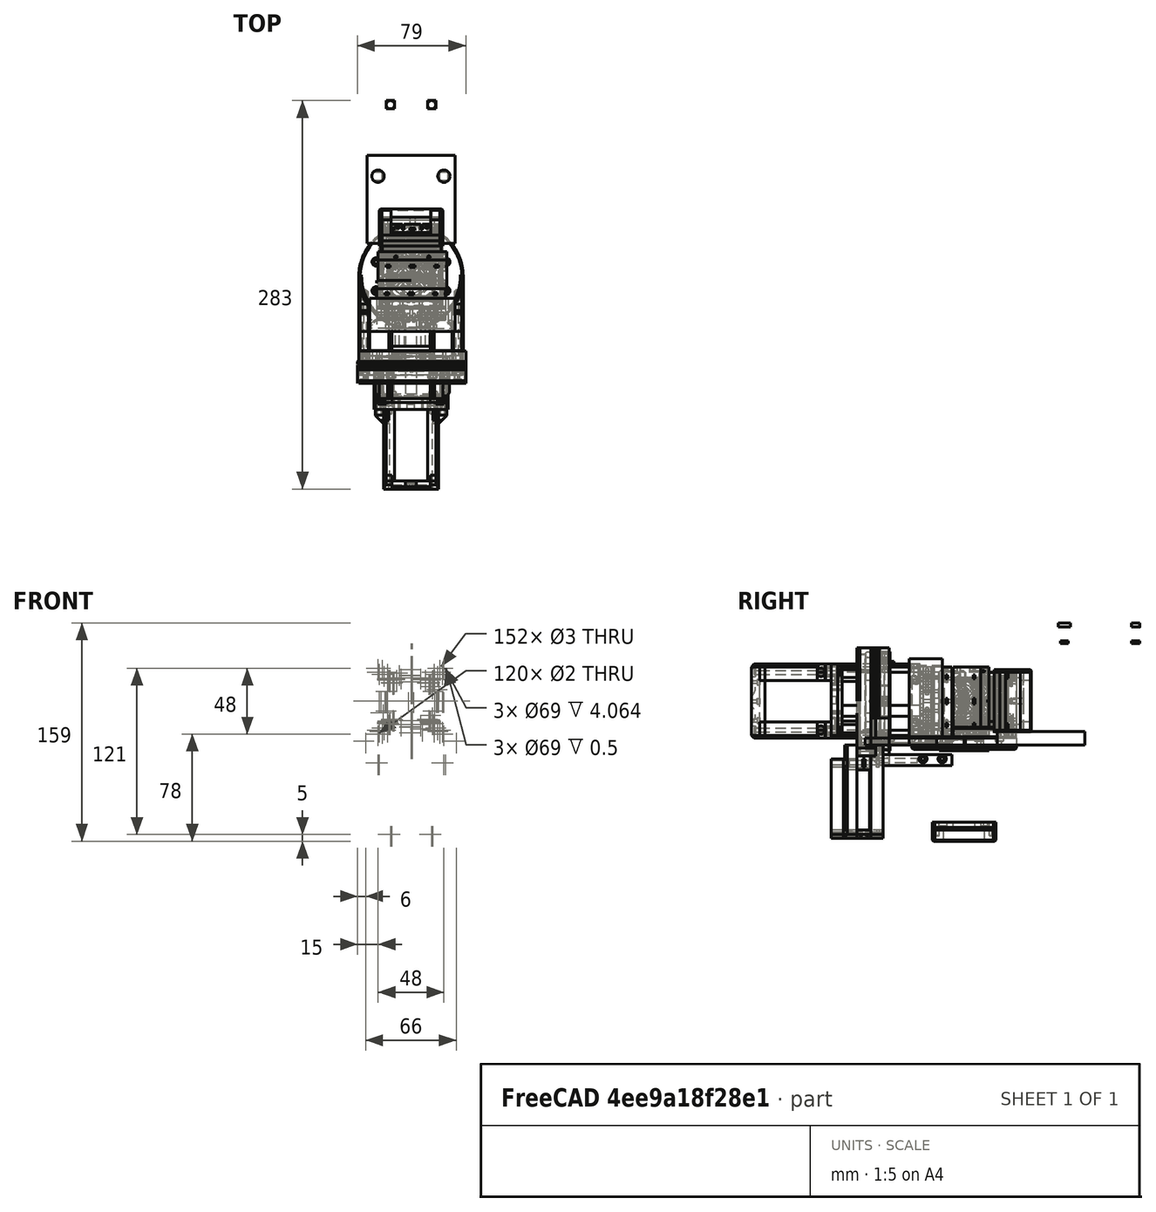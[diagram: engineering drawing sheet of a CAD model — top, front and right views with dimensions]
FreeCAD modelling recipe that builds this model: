
FCSTD DOCUMENT  (FreeCAD 0.19R24276 (Git))
Label: G-mini_056
License: All rights reserved
LicenseURL: http://en.wikipedia.org/wiki/All_rights_reserved
objects: Part::Cylinder×670, Part::Box×316, Part::Compound×305, Part::Cut×299, Part::Chamfer×105, Part::FeaturePython×44, Mesh::Feature×28, Part::Torus×9, Part::Common×4
note: 1752 computed .brp shape members not serialized (recipe doc carries the construction recipe); baked Part::Feature solids carry a one-line shape summary decoded from their .brp

FEATURE [Part::Cylinder] Cylinder2608  label="Válec2578"
  Angle = 360
  AttacherType = Attacher::AttachEngine3D
  Height = 3
  Placement = pos=(1.1e-14,-27.5,19) rot=(0,0,1;3.14159rad)
  Radius = 3
FEATURE [Part::Cylinder] Cylinder2607  label="Válec2577"
  Angle = 360
  AttacherType = Attacher::AttachEngine3D
  Height = 3
  Placement = pos=(-19.4454,-19.4454,19) rot=(0,0,1;2.35619rad)
  Radius = 3
FEATURE [Part::Cylinder] Cylinder2613  label="Válec2583"
  Angle = 360
  AttacherType = Attacher::AttachEngine3D
  Height = 20
  Placement = pos=(-19.4454,19.4454,19) rot=(0,0,1;0.785398rad)
  Radius = 1.5
FEATURE [Part::Cylinder] Cylinder2615  label="Válec2585"
  Angle = 360
  AttacherType = Attacher::AttachEngine3D
  Height = 20
  Placement = pos=(-19.4454,-19.4454,19) rot=(0,0,1;2.35619rad)
  Radius = 1.5
FEATURE [Part::Cylinder] Cylinder2617  label="Válec2587"
  Angle = 360
  AttacherType = Attacher::AttachEngine3D
  Height = 20
  Placement = pos=(19.4454,-19.4454,19) rot=(0,0,1;3.92699rad)
  Radius = 1.5
FEATURE [Part::Cylinder] Cylinder2605  label="Válec2575"
  Angle = 360
  AttacherType = Attacher::AttachEngine3D
  Height = 3
  Placement = pos=(-19.4454,19.4454,19) rot=(0,0,1;0.785398rad)
  Radius = 3
FEATURE [Part::Cylinder] Cylinder2606  label="Válec2576"
  Angle = 360
  AttacherType = Attacher::AttachEngine3D
  Height = 3
  Placement = pos=(-27.5,-4e-15,19) rot=(0,0,1;1.5708rad)
  Radius = 3
FEATURE [Part::Cylinder] Cylinder2609  label="Válec2579"
  Angle = 360
  AttacherType = Attacher::AttachEngine3D
  Height = 3
  Placement = pos=(19.4454,-19.4454,19) rot=(0,0,1;3.92699rad)
  Radius = 3
FEATURE [Part::Cylinder] Cylinder2610  label="Válec2580"
  Angle = 360
  AttacherType = Attacher::AttachEngine3D
  Height = 3
  Placement = pos=(27.5,1.2e-14,19) rot=(0,0,-1;1.5708rad)
  Radius = 3
FEATURE [Part::Cylinder] Cylinder2611  label="Válec2581"
  Angle = 360
  AttacherType = Attacher::AttachEngine3D
  Height = 3
  Placement = pos=(19.4454,19.4454,19) rot=(0,0,-1;0.785398rad)
  Radius = 3
FEATURE [Part::Cylinder] Cylinder2614  label="Válec2584"
  Angle = 360
  AttacherType = Attacher::AttachEngine3D
  Height = 20
  Placement = pos=(-27.5,-4e-15,19) rot=(0,0,1;1.5708rad)
  Radius = 1.5
FEATURE [Part::Cylinder] Cylinder2616  label="Válec2586"
  Angle = 360
  AttacherType = Attacher::AttachEngine3D
  Height = 20
  Placement = pos=(1.1e-14,-27.5,19) rot=(0,0,1;3.14159rad)
  Radius = 1.5
FEATURE [Part::Cylinder] Cylinder2031  label="Válec2031"
  Angle = 360
  AttacherType = Attacher::AttachEngine3D
  Height = 30
  Placement = pos=(51,-30,0) rot=(0,0,1;0rad)
  Radius = 1.5
FEATURE [Part::Cylinder] Cylinder2014  label="Válec2014"
  Angle = 360
  AttacherType = Attacher::AttachEngine3D
  Height = 3
  Placement = pos=(0,27.5,19) rot=(0,0,1;0rad)
  Radius = 3
FEATURE [Part::Compound] Compound901
  Links = -> [Cylinder2014,Cylinder2605,Cylinder2606,Cylinder2607,Cylinder2608,Cylinder2609,Cylinder2610,Cylinder2611]
  Placement = pos=(0,0,-19) rot=(0,0,1;0rad)
FEATURE [Part::Cylinder] Cylinder2619  label="Válec2589"
  Angle = 360
  AttacherType = Attacher::AttachEngine3D
  Height = 20
  Placement = pos=(19.4454,19.4454,19) rot=(0,0,-1;0.785398rad)
  Radius = 1.5
FEATURE [Part::Cylinder] Cylinder2618  label="Válec2588"
  Angle = 360
  AttacherType = Attacher::AttachEngine3D
  Height = 20
  Placement = pos=(27.5,1.2e-14,19) rot=(0,0,-1;1.5708rad)
  Radius = 1.5
FEATURE [Part::Cylinder] Cylinder2016  label="Válec2016"
  Angle = 360
  AttacherType = Attacher::AttachEngine3D
  Height = 6
  Radius = 38
FEATURE [Part::Cut] Cut623
  Base = -> Cylinder2016
  Tool = -> Compound901
FEATURE [Part::Cylinder] Cylinder2023  label="Válec2023"
  Angle = 360
  AttacherType = Attacher::AttachEngine3D
  Height = 20
  Placement = pos=(0,27.5,19) rot=(0,0,1;0rad)
  Radius = 1.5
FEATURE [Part::Compound] Compound902
  Links = -> [Cylinder2023,Cylinder2613,Cylinder2614,Cylinder2615,Cylinder2616,Cylinder2617,Cylinder2618,Cylinder2619]
  Placement = pos=(0,0,-23) rot=(0,0,1;0rad)
FEATURE [Part::Cut] Cut624
  Base = -> Cut623
  Tool = -> Compound902
FEATURE [Part::Box] Box790  label="Krychle789"
  AttacherType = Attacher::AttachEngine3D
  Height = 80
  Length = 12
  Placement = pos=(-6,26,-48) rot=(0,0,1;0rad)
  Width = 7
FEATURE [Part::Compound] Compound1160
  Links = -> [Box790]
  Placement = pos=(80,-8,10) rot=(0.57735,-0.57735,0.57735;2.0944rad)
FEATURE [Part::Cylinder] Cylinder2035  label="Válec2035"
  Angle = 360
  AttacherType = Attacher::AttachEngine3D
  Height = 30
  Placement = pos=(51,16,0) rot=(0,0,1;0rad)
  Radius = 1.5
FEATURE [Part::Cylinder] Cylinder2033  label="Válec2033"
  Angle = 360
  AttacherType = Attacher::AttachEngine3D
  Height = 11
  Placement = pos=(44,0,10) rot=(0,1,0;1.5708rad)
  Radius = 38
FEATURE [Part::Common] Common005
  Base = -> Compound1160
  Tool = -> Cylinder2033
FEATURE [Part::Box] Box796  label="Krychle795"
  AttacherType = Attacher::AttachEngine3D
  Height = 2
  Length = 8
  Placement = pos=(48,-33,7) rot=(0,0,1;0rad)
  Width = 6
FEATURE [Part::Box] Box793  label="Krychle792"
  AttacherType = Attacher::AttachEngine3D
  Height = 2
  Length = 8
  Placement = pos=(48,-3,11) rot=(0,0,1;0rad)
  Width = 6
FEATURE [Part::Cylinder] Cylinder2030  label="Válec2030"
  Angle = 360
  AttacherType = Attacher::AttachEngine3D
  Height = 5
  Placement = pos=(0,0,1) rot=(0,0,1;0rad)
  Radius = 14
FEATURE [Part::Cut] Cut625
  Base = -> Cut624
  Tool = -> Cylinder2030
FEATURE [Part::Chamfer] Chamfer117
  Base = -> Cut625
  Edges = 1 edges r=1: [Edge3]
FEATURE [Part::Box] Box792  label="Krychle791"
  AttacherType = Attacher::AttachEngine3D
  Height = 2
  Length = 8
  Placement = pos=(48,-3,7) rot=(0,0,1;0rad)
  Width = 6
FEATURE [Part::Box] Box794  label="Krychle793"
  AttacherType = Attacher::AttachEngine3D
  Height = 2
  Length = 8
  Placement = pos=(48,27,11) rot=(0,0,1;0rad)
  Width = 6
FEATURE [Part::Cylinder] Cylinder2034  label="Válec2034"
  Angle = 360
  AttacherType = Attacher::AttachEngine3D
  Height = 30
  Placement = pos=(51,30,0) rot=(0,0,1;0rad)
  Radius = 1.5
FEATURE [Part::Box] Box795  label="Krychle794"
  AttacherType = Attacher::AttachEngine3D
  Height = 2
  Length = 8
  Placement = pos=(48,-33,11) rot=(0,0,1;0rad)
  Width = 6
FEATURE [Part::Box] Box798  label="Krychle797"
  AttacherType = Attacher::AttachEngine3D
  Height = 2
  Length = 8
  Placement = pos=(48,27,7) rot=(0,0,1;0rad)
  Width = 6
FEATURE [Part::Box] Box797  label="Krychle796"
  AttacherType = Attacher::AttachEngine3D
  Height = 2
  Length = 8
  Placement = pos=(48,27,11) rot=(0,0,1;0rad)
  Width = 6
FEATURE [Part::Compound] Compound1159
  Links = -> [Box797,Box798]
  Placement = pos=(0,-14,0) rot=(0,0,1;0rad)
FEATURE [Part::Cylinder] Cylinder2032  label="Válec2032"
  Angle = 360
  AttacherType = Attacher::AttachEngine3D
  Height = 30
  Placement = pos=(51,0,0) rot=(0,0,1;0rad)
  Radius = 1.5
FEATURE [Part::Compound] Compound905
  Links = -> [Cylinder2031,Cylinder2032,Cylinder2034,Cylinder2035]
FEATURE [Part::Box] Box789  label="Krychle788"
  AttacherType = Attacher::AttachEngine3D
  Height = 2
  Length = 8
  Placement = pos=(48,27,7) rot=(0,0,1;0rad)
  Width = 6
FEATURE [Part::Compound] Compound903
  Links = -> [Box792,Box793,Box795,Box796,Box794,Box789,Compound1159]
FEATURE [Part::Cut] Cut626
  Base = -> Common005
  Tool = -> Compound903
FEATURE [Part::Cut] Cut627
  Base = -> Cut626
  Placement = pos=(-9.24,-3.83,48) rot=(-0.19148,0.962637,0.19148;1.60885rad)
  Tool = -> Compound905
FEATURE [Part::FeaturePython] Tube114  # WARN: FeaturePython — macro-defined, semantics opaque (R4)
  AttacherType = Attacher::AttachEngine3D
  Height = 1
  InnerRadius = 12
  OuterRadius = 14
  Placement = pos=(0,0,1) rot=(0,0,1;0rad)
FEATURE [Part::Compound] Compound907  label="J-mini_wrist-side-rotator"
  Links = -> [Tube114,Cut627,Chamfer117]
  Placement = pos=(0,0,11) rot=(0.980785,0.19509,0;3.14159rad)
FEATURE [Part::Torus] Torus002  label="Anuloid002"
  Angle1 = -180
  Angle2 = 180
  Angle3 = 360
  AttacherType = Attacher::AttachEngine3D
  Placement = pos=(17,-98,10) rot=(1,0,0;1.5708rad)
  Radius1 = 34
  Radius2 = 2
FEATURE [Part::FeaturePython] Tube018  # WARN: FeaturePython — macro-defined, semantics opaque (R4)
  AttacherType = Attacher::AttachEngine3D
  Height = 11.5
  InnerRadius = 34.5
  OuterRadius = 39
  Placement = pos=(17,-92,10) rot=(1,0,0;1.5708rad)
FEATURE [Part::Cut] Cut317
  Base = -> Tube018
  Tool = -> Torus002
FEATURE [Part::Cylinder] Cylinder2201  label="Válec2201"
  Angle = 360
  AttacherType = Attacher::AttachEngine3D
  Height = 10
  Placement = pos=(17,-98,44) rot=(1,0,0;1.5708rad)
  Radius = 2
FEATURE [Part::Cut] Cut804
  Base = -> Cut317
  Placement = pos=(0,-2,0) rot=(0,0,1;0rad)
  Tool = -> Cylinder2201
FEATURE [Part::Box] Box846  label="Krychle845"
  AttacherType = Attacher::AttachEngine3D
  Height = 10
  Length = 8
  Placement = pos=(56,-151,-6) rot=(0,0,1;0rad)
  Width = 59
FEATURE [Part::Box] Box847  label="Krychle846"
  AttacherType = Attacher::AttachEngine3D
  Height = 9
  Length = 8
  Placement = pos=(56,-151,16) rot=(0,0,1;0rad)
  Width = 59
FEATURE [Part::Cylinder] Cylinder2207  label="Válec2207"
  Angle = 360
  AttacherType = Attacher::AttachEngine3D
  Height = 32
  Placement = pos=(59,-130,-6) rot=(0,0,1;0rad)
  Radius = 1.5
FEATURE [Part::Cylinder] Cylinder2208  label="Válec2208"
  Angle = 360
  AttacherType = Attacher::AttachEngine3D
  Height = 32
  Placement = pos=(59,-144,-6) rot=(0,0,1;0rad)
  Radius = 1.5
FEATURE [Part::Cylinder] Cylinder2209  label="Válec2209"
  Angle = 360
  AttacherType = Attacher::AttachEngine3D
  Height = 4
  Placement = pos=(59,-130,-8) rot=(0,0,1;0rad)
  Radius = 3
FEATURE [Part::Cylinder] Cylinder2210  label="Válec2210"
  Angle = 360
  AttacherType = Attacher::AttachEngine3D
  Height = 4
  Placement = pos=(59,-144,-8) rot=(0,0,1;0rad)
  Radius = 3
FEATURE [Part::Cylinder] Cylinder2211  label="Válec2211"
  Angle = 360
  AttacherType = Attacher::AttachEngine3D
  Height = 4
  Placement = pos=(59,-144,24) rot=(0,0,1;0rad)
  Radius = 3
FEATURE [Part::Cylinder] Cylinder2212  label="Válec2212"
  Angle = 360
  AttacherType = Attacher::AttachEngine3D
  Height = 4
  Placement = pos=(59,-130,24) rot=(0,0,1;0rad)
  Radius = 3
FEATURE [Part::Cylinder] Cylinder2213  label="Válec2213"
  Angle = 360
  AttacherType = Attacher::AttachEngine3D
  Height = 40
  Placement = pos=(60,-86,21) rot=(1,0,0;1.5708rad)
  Radius = 1.5
FEATURE [Part::Cylinder] Cylinder2221  label="Válec2221"
  Angle = 360
  AttacherType = Attacher::AttachEngine3D
  Height = 40
  Placement = pos=(60,-86,-1) rot=(1,0,0;1.5708rad)
  Radius = 1.5
FEATURE [Part::Cylinder] Cylinder2222  label="Válec2222"
  Angle = 360
  AttacherType = Attacher::AttachEngine3D
  Height = 6
  Placement = pos=(60,-86,21) rot=(1,0,0;1.5708rad)
  Radius = 3
FEATURE [Part::Cylinder] Cylinder2223  label="Válec2223"
  Angle = 360
  AttacherType = Attacher::AttachEngine3D
  Height = 6
  Placement = pos=(60,-86,-1) rot=(1,0,0;1.5708rad)
  Radius = 3
FEATURE [Part::Box] Box860  label="Krychle859"
  AttacherType = Attacher::AttachEngine3D
  Height = 10
  Length = 6
  Placement = pos=(50,-105.5,-6) rot=(0,0,1;0rad)
  Width = 13.5
FEATURE [Part::Box] Box861  label="Krychle860"
  AttacherType = Attacher::AttachEngine3D
  Height = 9
  Length = 6
  Placement = pos=(50,-105.5,16) rot=(0,0,1;0rad)
  Width = 13.5
FEATURE [Part::Box] Box866  label="Krychle865"
  AttacherType = Attacher::AttachEngine3D
  Height = 12
  Length = 11
  Placement = pos=(53,-105.5,4) rot=(0,0,1;0rad)
  Width = 13.5
FEATURE [Part::Cylinder] Cylinder2236  label="Válec2236"
  Angle = 360
  AttacherType = Attacher::AttachEngine3D
  Height = 16
  Placement = pos=(64,-92,10) rot=(1,0,0;1.5708rad)
  Radius = 6
FEATURE [Part::FeaturePython] Tube037  # WARN: FeaturePython — macro-defined, semantics opaque (R4)
  AttacherType = Attacher::AttachEngine3D
  Height = 0.5
  InnerRadius = 34.5
  OuterRadius = 39
  Placement = pos=(17,-93.5,10) rot=(1,0,0;1.5708rad)
FEATURE [Part::FeaturePython] Tube038  # WARN: FeaturePython — macro-defined, semantics opaque (R4)
  AttacherType = Attacher::AttachEngine3D
  Height = 1.5
  InnerRadius = 31
  OuterRadius = 39
  Placement = pos=(17,-92,10) rot=(1,0,0;1.5708rad)
FEATURE [Part::FeaturePython] Tube040  # WARN: FeaturePython — macro-defined, semantics opaque (R4)
  AttacherType = Attacher::AttachEngine3D
  Height = 13.5
  InnerRadius = 31
  OuterRadius = 39
  Placement = pos=(17,-92,10) rot=(1,0,0;1.5708rad)
FEATURE [Part::FeaturePython] Tube041  # WARN: FeaturePython — macro-defined, semantics opaque (R4)
  AttacherType = Attacher::AttachEngine3D
  Height = 13.5
  InnerRadius = 31
  OuterRadius = 39
  Placement = pos=(17,-92,10) rot=(1,0,0;1.5708rad)
FEATURE [Part::Compound] Compound991
  Links = -> [Cylinder2211,Cylinder2212]
FEATURE [Part::Compound] Compound992
  Links = -> [Cylinder2209,Cylinder2210]
FEATURE [Part::Compound] Compound993
  Links = -> [Cylinder2207,Cylinder2208]
FEATURE [Part::Compound] Compound996
  Links = -> [Tube038,Tube037]
FEATURE [Part::Compound] Compound1001
  Links = -> [Box861,Box860]
FEATURE [Part::Cut] Cut824
  Base = -> Compound1001
  Tool = -> Tube040
FEATURE [Part::Chamfer] Chamfer077
  Base = -> Box846
  Edges = 1 edges r=6: [Edge7]
FEATURE [Part::Chamfer] Chamfer078
  Base = -> Box847
  Edges = 1 edges r=6: [Edge7]
FEATURE [Part::Compound] Compound1002
  Links = -> [Cylinder2223,Cylinder2222]
  Placement = pos=(0,-6,0) rot=(0,0,1;0rad)
FEATURE [Part::Compound] Compound1003
  Links = -> [Chamfer078,Chamfer077]
FEATURE [Part::Cut] Cut825
  Base = -> Compound1003
  Tool = -> Compound1002
FEATURE [Part::Compound] Compound1004
  Links = -> [Cylinder2221,Cylinder2213]
FEATURE [Part::Cut] Cut826
  Base = -> Cut825
  Tool = -> Compound1004
FEATURE [Part::Cut] Cut827
  Base = -> Cut826
  Tool = -> Compound993
FEATURE [Part::Cut] Cut828
  Base = -> Cut827
  Tool = -> Compound992
FEATURE [Part::Cut] Cut829
  Base = -> Cut828
  Tool = -> Compound991
FEATURE [Part::Compound] Compound1005
  Links = -> [Cut804,Compound996]
FEATURE [Part::Compound] Compound1006  label="wrist_halo_outer3"
  Links = -> [Cut824,Cut829,Compound1005]
FEATURE [Part::Cut] Cut833
  Base = -> Box866
  Tool = -> Tube041
FEATURE [Part::Chamfer] Chamfer079
  Base = -> Cut833
  Edges = 1 edges r=6: [Edge10]
FEATURE [Part::Cut] Cut834
  Base = -> Chamfer079
  Tool = -> Cylinder2236
FEATURE [Part::Compound] Compound1017  label="Wrist_outer-halo"
  Links = -> [Compound1006,Cut834]
  Placement = pos=(11,-160,54) rot=(0.707107,0,-0.707107;3.14159rad)
FEATURE [Part::Cylinder] Cylinder2594  label="Válec2564"
  Angle = 360
  AttacherType = Attacher::AttachEngine3D
  Height = 20
  Placement = pos=(-19.4454,19.4454,10) rot=(0,0,1;0.785398rad)
  Radius = 1.5
FEATURE [Part::Cylinder] Cylinder2595  label="Válec2565"
  Angle = 360
  AttacherType = Attacher::AttachEngine3D
  Height = 3
  Radius = 38
FEATURE [Part::Cylinder] Cylinder2596  label="Válec2566"
  Angle = 360
  AttacherType = Attacher::AttachEngine3D
  Height = 34
  Placement = pos=(0,0,-21) rot=(0,0,1;0rad)
  Radius = 14
FEATURE [Part::Cut] Cut967
  Base = -> Cylinder2595
  Placement = pos=(0,0,10) rot=(0,0,1;0rad)
  Tool = -> Cylinder2596
FEATURE [Part::Chamfer] Chamfer116  label="J-mini_encoder-belt-ring_front004"
  Base = -> Cut967
  Edges = 1 edges r=1: [Edge3]
  Placement = pos=(0,0,-8) rot=(0,0,1;0rad)
FEATURE [Part::Cylinder] Cylinder2597  label="Válec2567"
  Angle = 360
  AttacherType = Attacher::AttachEngine3D
  Height = 20
  Placement = pos=(19.4454,19.4454,10) rot=(0,0,-1;0.785398rad)
  Radius = 1.5
FEATURE [Part::Cylinder] Cylinder2598  label="Válec2568"
  Angle = 360
  AttacherType = Attacher::AttachEngine3D
  Height = 20
  Placement = pos=(27.5,1.2e-14,10) rot=(0,0,-1;1.5708rad)
  Radius = 1.5
FEATURE [Part::Cylinder] Cylinder2599  label="Válec2569"
  Angle = 360
  AttacherType = Attacher::AttachEngine3D
  Height = 20
  Placement = pos=(1.1e-14,-27.5,10) rot=(0,0,1;3.14159rad)
  Radius = 1.5
FEATURE [Part::Cylinder] Cylinder2600  label="Válec2570"
  Angle = 360
  AttacherType = Attacher::AttachEngine3D
  Height = 20
  Placement = pos=(19.4454,-19.4454,10) rot=(0,0,1;3.92699rad)
  Radius = 1.5
FEATURE [Part::Cylinder] Cylinder2601  label="Válec2571"
  Angle = 360
  AttacherType = Attacher::AttachEngine3D
  Height = 20
  Placement = pos=(-19.4454,-19.4454,10) rot=(0,0,1;2.35619rad)
  Radius = 1.5
FEATURE [Part::Cylinder] Cylinder2602  label="Válec2572"
  Angle = 360
  AttacherType = Attacher::AttachEngine3D
  Height = 20
  Placement = pos=(-27.5,-4e-15,10) rot=(0,0,1;1.5708rad)
  Radius = 1.5
FEATURE [Part::Cylinder] Cylinder2603  label="Válec2573"
  Angle = 360
  AttacherType = Attacher::AttachEngine3D
  Height = 20
  Placement = pos=(0,27.5,10) rot=(0,0,1;0rad)
  Radius = 1.5
FEATURE [Part::Compound] Compound1158
  Links = -> [Cylinder2603,Cylinder2594,Cylinder2602,Cylinder2601,Cylinder2599,Cylinder2598,Cylinder2600,Cylinder2597]
  Placement = pos=(0,0,-16) rot=(0,0,1;0.392699rad)
FEATURE [Part::Cut] Cut968  label="J-mini_encoder-belt-ring_front003"
  Base = -> Chamfer116
  Tool = -> Compound1158
FEATURE [Part::FeaturePython] Tube113  # WARN: FeaturePython — macro-defined, semantics opaque (R4)
  AttacherType = Attacher::AttachEngine3D
  Height = 4
  InnerRadius = 14
  OuterRadius = 18
  Placement = pos=(0,0,1) rot=(0,0,1;0rad)
FEATURE [Part::Chamfer] Chamfer115
  Base = -> Tube113
  Edges = 1 edges r=1: [Edge5]
FEATURE [Part::Compound] Compound1157  label="J-mini_encoder-belt-ring_front"
  Links = -> [Cut968,Chamfer115]
FEATURE [Part::Box] Box868  label="Krychle867"
  AttacherType = Attacher::AttachEngine3D
  Height = 6
  Length = 2
  Placement = pos=(-1,-138,-2) rot=(0,0,1;0rad)
  Width = 6
FEATURE [Part::Box] Box869  label="Krychle868"
  AttacherType = Attacher::AttachEngine3D
  Height = 6
  Length = 2
  Placement = pos=(-1,-138,16) rot=(0,0,1;0rad)
  Width = 6
FEATURE [Part::Box] Box870  label="Krychle869"
  AttacherType = Attacher::AttachEngine3D
  Height = 6
  Length = 2
  Placement = pos=(33,-138,-2) rot=(0,0,1;0rad)
  Width = 6
FEATURE [Part::Box] Box871  label="Krychle870"
  AttacherType = Attacher::AttachEngine3D
  Height = 6
  Length = 2
  Placement = pos=(33,-138,16) rot=(0,0,1;0rad)
  Width = 6
FEATURE [Part::Cylinder] Cylinder2237  label="Válec2237"
  Angle = 360
  AttacherType = Attacher::AttachEngine3D
  Height = 3
  Placement = pos=(8.41904,-20.3253,34) rot=(0,0,1;3.53429rad)
  Radius = 3
FEATURE [Part::Cylinder] Cylinder2238  label="Válec2238"
  Angle = 360
  AttacherType = Attacher::AttachEngine3D
  Height = 60
  Placement = pos=(20.3253,8.41904,34) rot=(0,0,-1;1.1781rad)
  Radius = 1.5
FEATURE [Part::Cylinder] Cylinder2239  label="Válec2239"
  Angle = 360
  AttacherType = Attacher::AttachEngine3D
  Height = 6
  Placement = pos=(0,0,39) rot=(0,0,1;0rad)
  Radius = 30
FEATURE [Part::Cylinder] Cylinder2240  label="Válec2240"
  Angle = 360
  AttacherType = Attacher::AttachEngine3D
  Height = 60
  Placement = pos=(-8.41904,20.3253,34) rot=(0,0,1;0.392699rad)
  Radius = 1.5
FEATURE [Part::Cylinder] Cylinder2241  label="Válec2241"
  Angle = 360
  AttacherType = Attacher::AttachEngine3D
  Height = 3
  Placement = pos=(-20.3253,-8.41904,34) rot=(0,0,1;1.96349rad)
  Radius = 3
FEATURE [Part::Cylinder] Cylinder2242  label="Válec2242"
  Angle = 360
  AttacherType = Attacher::AttachEngine3D
  Height = 60
  Placement = pos=(-20.3253,-8.41904,34) rot=(0,0,1;1.96349rad)
  Radius = 1.5
FEATURE [Part::Cylinder] Cylinder2243  label="Válec2243"
  Angle = 360
  AttacherType = Attacher::AttachEngine3D
  Height = 3
  Placement = pos=(-8.41904,20.3253,34) rot=(0,0,1;0.392699rad)
  Radius = 3
FEATURE [Part::Cylinder] Cylinder2244  label="Válec2244"
  Angle = 360
  AttacherType = Attacher::AttachEngine3D
  Height = 60
  Placement = pos=(8.41904,-20.3253,34) rot=(0,0,1;3.53429rad)
  Radius = 1.5
FEATURE [Part::Box] Box872  label="Krychle871"
  AttacherType = Attacher::AttachEngine3D
  Height = 20
  Length = 10
  Placement = pos=(-35,-38.15,45) rot=(0,0,1;0rad)
  Width = 80
FEATURE [Part::Cylinder] Cylinder2245  label="Válec2245"
  Angle = 360
  AttacherType = Attacher::AttachEngine3D
  Height = 3
  Placement = pos=(20.3253,8.41904,34) rot=(0,0,-1;1.1781rad)
  Radius = 3
FEATURE [Part::Box] Box873  label="Krychle872"
  AttacherType = Attacher::AttachEngine3D
  Height = 20
  Length = 10
  Placement = pos=(25,-38.15,45) rot=(0,0,1;0rad)
  Width = 80
FEATURE [Part::Cylinder] Cylinder2246  label="Válec2246"
  Angle = 360
  AttacherType = Attacher::AttachEngine3D
  Height = 20
  Placement = pos=(0,0,37) rot=(0,0,1;0rad)
  Radius = 16
FEATURE [Part::Box] Box874  label="Krychle873"
  AttacherType = Attacher::AttachEngine3D
  Height = 32.2
  Length = 5.85
  Placement = pos=(-10,-138,-6.1) rot=(0,0,1;0rad)
  Width = 60
FEATURE [Part::Box] Box875  label="Krychle874"
  AttacherType = Attacher::AttachEngine3D
  Height = 32.2
  Length = 5.85
  Placement = pos=(38.15,-138,-6.1) rot=(0,0,1;0rad)
  Width = 60
FEATURE [Part::Cylinder] Cylinder2247  label="Válec2247"
  Angle = 360
  AttacherType = Attacher::AttachEngine3D
  Height = 16
  Placement = pos=(14,9,64) rot=(0,1,0;1.5708rad)
  Radius = 1.5
FEATURE [Part::Cylinder] Cylinder2248  label="Válec2248"
  Angle = 360
  AttacherType = Attacher::AttachEngine3D
  Height = 16
  Placement = pos=(14,-9,64) rot=(0,1,0;1.5708rad)
  Radius = 1.5
FEATURE [Part::Cylinder] Cylinder2249  label="Válec2249"
  Angle = 360
  AttacherType = Attacher::AttachEngine3D
  Height = 16
  Placement = pos=(-24,9,64) rot=(0,1,0;1.5708rad)
  Radius = 1.5
FEATURE [Part::Cylinder] Cylinder2250  label="Válec2250"
  Angle = 360
  AttacherType = Attacher::AttachEngine3D
  Height = 16
  Placement = pos=(-24,-9,64) rot=(0,1,0;1.5708rad)
  Radius = 1.5
FEATURE [Part::Compound] Compound1019
  Links = -> [Cylinder2240,Cylinder2242,Cylinder2244,Cylinder2238]
  Placement = pos=(0,0,0) rot=(0,0,1;0.392699rad)
FEATURE [Part::Compound] Compound1020
  Links = -> [Cylinder2243,Cylinder2241,Cylinder2237,Cylinder2245]
  Placement = pos=(0,0,8) rot=(0,0,1;0.392699rad)
FEATURE [Part::Compound] Compound1021
  Links = -> [Box872,Box873]
  Placement = pos=(0,0,-8) rot=(0,0,1;0rad)
FEATURE [Part::Compound] Compound1022
  Links = -> [Box874,Box875]
FEATURE [Part::Compound] Compound1023
  Links = -> [Box868,Box869,Box870,Box871]
FEATURE [Part::Compound] Compound1024
  Links = -> [Cylinder2249,Cylinder2250,Cylinder2247,Cylinder2248]
  Placement = pos=(14,-71,10) rot=(1,0,0;1.5708rad)
FEATURE [Part::Cut] Cut836
  Base = -> Cylinder2239
  Placement = pos=(0,0,3) rot=(0,0,1;0rad)
  Tool = -> Compound1020
FEATURE [Part::Cut] Cut837
  Base = -> Cut836
  Tool = -> Compound1019
FEATURE [Part::Cut] Cut835
  Base = -> Cut837
  Tool = -> Compound1021
FEATURE [Part::Cut] Cut838
  Base = -> Cut835
  Placement = pos=(17,-180,10) rot=(-1,0,0;1.5708rad)
  Tool = -> Cylinder2246
FEATURE [Part::Cut] Cut839
  Base = -> Cut838
  Tool = -> Compound1022
FEATURE [Part::Cut] Cut840  label="wrist_actuator_ring2"
  Base = -> Cut839
  Tool = -> Compound1023
FEATURE [Part::Cut] Cut841  label="Wrist_actuator-ring"
  Base = -> Cut840
  Placement = pos=(-10,-170,20) rot=(0.707107,0,0.707107;3.14159rad)
  Tool = -> Compound1024
FEATURE [Part::Cylinder] Cylinder473  label="Válec473"
  Angle = 360
  AttacherType = Attacher::AttachEngine3D
  Height = 3
  Placement = pos=(15.5,15.5,-54) rot=(0,0,1;0rad)
  Radius = 3
FEATURE [Part::Box] Box302  label="Krychle302"
  AttacherType = Attacher::AttachEngine3D
  Height = 8
  Length = 54
  Placement = pos=(-27,-26,-24) rot=(0,0,1;0rad)
  Width = 52
FEATURE [Part::Box] Box303  label="Krychle303"
  AttacherType = Attacher::AttachEngine3D
  Height = 2
  Length = 8
  Placement = pos=(-24.5,-22.5,-55) rot=(0,0,1;0rad)
  Width = 6
FEATURE [Part::Cylinder] Cylinder476  label="Válec476"
  Angle = 360
  AttacherType = Attacher::AttachEngine3D
  Height = 20
  Placement = pos=(21,23,-28) rot=(0,0,1;0rad)
  Radius = 1.5
FEATURE [Part::Cylinder] Cylinder477  label="Válec477"
  Angle = 360
  AttacherType = Attacher::AttachEngine3D
  Height = 3
  Placement = pos=(-15.5,15.5,-54) rot=(0,0,1;0rad)
  Radius = 3
FEATURE [Part::Cylinder] Cylinder478  label="Válec478"
  Angle = 360
  AttacherType = Attacher::AttachEngine3D
  Height = 3
  Placement = pos=(-15.5,-15.5,-54) rot=(0,0,1;0rad)
  Radius = 3
FEATURE [Part::Cylinder] Cylinder479  label="Válec479"
  Angle = 360
  AttacherType = Attacher::AttachEngine3D
  Height = 20
  Placement = pos=(15.5,-15.5,-68) rot=(0,0,1;0rad)
  Radius = 1.5
FEATURE [Part::Cylinder] Cylinder480  label="Válec480"
  Angle = 360
  AttacherType = Attacher::AttachEngine3D
  Height = 20
  Placement = pos=(10.48,15.75,-50) rot=(0,0,1;0rad)
  Radius = 1.5
FEATURE [Part::Cylinder] Cylinder481  label="Válec481"
  Angle = 360
  AttacherType = Attacher::AttachEngine3D
  Height = 20
  Placement = pos=(15.5,15.5,-68) rot=(0,0,1;0rad)
  Radius = 1.5
FEATURE [Part::Cylinder] Cylinder482  label="Válec482"
  Angle = 360
  AttacherType = Attacher::AttachEngine3D
  Height = 3
  Placement = pos=(15.5,-15.5,-54) rot=(0,0,1;0rad)
  Radius = 3
FEATURE [Part::Compound] Compound230
  Links = -> [Cylinder478,Cylinder482,Cylinder477,Cylinder473]
FEATURE [Part::Cylinder] Cylinder483  label="Válec483"
  Angle = 360
  AttacherType = Attacher::AttachEngine3D
  Height = 20
  Placement = pos=(-10.48,15.75,-50) rot=(0,0,1;0rad)
  Radius = 1.5
FEATURE [Part::Compound] Compound228
  Links = -> [Cylinder483,Cylinder480]
  Placement = pos=(0,0,-10) rot=(0,0,1;0rad)
FEATURE [Part::Box] Box307  label="Krychle307"
  AttacherType = Attacher::AttachEngine3D
  Height = 2
  Length = 8
  Placement = pos=(16.5,-22.5,-55) rot=(0,0,1;0rad)
  Width = 6
FEATURE [Part::Cylinder] Cylinder485  label="Válec485"
  Angle = 360
  AttacherType = Attacher::AttachEngine3D
  Height = 20
  Placement = pos=(-21,23,-28) rot=(0,0,1;0rad)
  Radius = 1.5
FEATURE [Part::Box] Box309  label="Krychle309"
  AttacherType = Attacher::AttachEngine3D
  Height = 2
  Length = 8
  Placement = pos=(16.5,16.5,-55) rot=(0,0,1;0rad)
  Width = 6
FEATURE [Part::Box] Box310  label="Krychle310"
  AttacherType = Attacher::AttachEngine3D
  Height = 2
  Length = 8
  Placement = pos=(-24.5,16.5,-55) rot=(0,0,1;0rad)
  Width = 6
FEATURE [Part::Compound] Compound227
  Links = -> [Box309,Box310,Box307,Box303]
  Placement = pos=(0,0,10) rot=(0,0,1;0rad)
FEATURE [Part::Cylinder] Cylinder486  label="Válec486"
  Angle = 360
  AttacherType = Attacher::AttachEngine3D
  Height = 20
  Placement = pos=(-15.5,-15.5,-68) rot=(0,0,1;0rad)
  Radius = 1.5
FEATURE [Part::Cylinder] Cylinder487  label="Válec487"
  Angle = 360
  AttacherType = Attacher::AttachEngine3D
  Height = 20
  Placement = pos=(21,-23,-28) rot=(0,0,1;0rad)
  Radius = 1.5
FEATURE [Part::Cylinder] Cylinder489  label="Válec489"
  Angle = 360
  AttacherType = Attacher::AttachEngine3D
  Height = 20
  Placement = pos=(-15.5,15.5,-68) rot=(0,0,1;0rad)
  Radius = 1.5
FEATURE [Part::Compound] Compound237
  Links = -> [Cylinder481,Cylinder489,Cylinder479,Cylinder486]
  Placement = pos=(0,0,4) rot=(0,0,1;0rad)
FEATURE [Part::Cylinder] Cylinder495  label="Válec495"
  Angle = 360
  AttacherType = Attacher::AttachEngine3D
  Height = 50
  Placement = pos=(0,0,-29) rot=(0,0,1;0rad)
  Radius = 8
FEATURE [Part::Cut] Cut280
  Base = -> Box302
  Tool = -> Cylinder495
FEATURE [Part::Cylinder] Cylinder496  label="Válec496"
  Angle = 360
  AttacherType = Attacher::AttachEngine3D
  Height = 20
  Placement = pos=(-21,-23,-28) rot=(0,0,1;0rad)
  Radius = 1.5
FEATURE [Part::Compound] Compound236
  Links = -> [Cylinder496,Cylinder476,Cylinder485,Cylinder487]
FEATURE [Part::Box] Box312  label="Krychle312"
  AttacherType = Attacher::AttachEngine3D
  Height = 2
  Length = 6
  Placement = pos=(25,19,-55) rot=(0,0,1;0rad)
  Width = 8
FEATURE [Part::Box] Box313  label="Krychle313"
  AttacherType = Attacher::AttachEngine3D
  Height = 2
  Length = 6
  Placement = pos=(-17,-25,-55) rot=(0,0,1;0rad)
  Width = 8
FEATURE [Part::Box] Box314  label="Krychle314"
  AttacherType = Attacher::AttachEngine3D
  Height = 2
  Length = 6
  Placement = pos=(-17,19,-55) rot=(0,0,1;0rad)
  Width = 8
FEATURE [Part::Box] Box315  label="Krychle315"
  AttacherType = Attacher::AttachEngine3D
  Height = 2
  Length = 6
  Placement = pos=(25,-25,-55) rot=(0,0,1;0rad)
  Width = 8
FEATURE [Part::Compound] Compound238
  Links = -> [Box312,Box314,Box315,Box313]
  Placement = pos=(10,-24,11) rot=(-1,0,0;1.5708rad)
FEATURE [Part::Cylinder] Cylinder501  label="Válec501"
  Angle = 360
  AttacherType = Attacher::AttachEngine3D
  Height = 20
  Placement = pos=(39.5,-17,10) rot=(1,0,0;1.5708rad)
  Radius = 2.65
FEATURE [Part::Cylinder] Cylinder502  label="Válec502"
  Angle = 360
  AttacherType = Attacher::AttachEngine3D
  Height = 20
  Placement = pos=(-5.5,-17,10) rot=(1,0,0;1.5708rad)
  Radius = 2.65
FEATURE [Part::Compound] Compound241
  Links = -> [Cylinder502,Cylinder501]
  Placement = pos=(0,-40,0) rot=(0,0,1;0rad)
FEATURE [Part::Box] Box324  label="Krychle324"
  AttacherType = Attacher::AttachEngine3D
  Height = 32
  Length = 5.85
  Placement = pos=(-10,-138,-6) rot=(0,0,1;0rad)
  Width = 60
FEATURE [Part::Box] Box325  label="Krychle325"
  AttacherType = Attacher::AttachEngine3D
  Height = 32
  Length = 5.85
  Placement = pos=(38.15,-138,-6) rot=(0,0,1;0rad)
  Width = 60
FEATURE [Part::Compound] Compound247
  Links = -> [Box324,Box325]
FEATURE [Part::Cylinder] Cylinder507  label="Válec507"
  Angle = 360
  AttacherType = Attacher::AttachEngine3D
  Height = 16
  Placement = pos=(18,-9,64) rot=(0,1,0;1.5708rad)
  Radius = 1.5
FEATURE [Part::Cylinder] Cylinder508  label="Válec508"
  Angle = 360
  AttacherType = Attacher::AttachEngine3D
  Height = 16
  Placement = pos=(18,9,64) rot=(0,1,0;1.5708rad)
  Radius = 1.5
FEATURE [Part::Cylinder] Cylinder509  label="Válec509"
  Angle = 360
  AttacherType = Attacher::AttachEngine3D
  Height = 16
  Placement = pos=(-28,9,64) rot=(0,1,0;1.5708rad)
  Radius = 1.5
FEATURE [Part::Cylinder] Cylinder510  label="Válec510"
  Angle = 360
  AttacherType = Attacher::AttachEngine3D
  Height = 16
  Placement = pos=(-28,-9,64) rot=(0,1,0;1.5708rad)
  Radius = 1.5
FEATURE [Part::Compound] Compound246
  Links = -> [Cylinder509,Cylinder510,Cylinder508,Cylinder507]
  Placement = pos=(14,-71,10) rot=(1,0,0;1.5708rad)
FEATURE [Part::Cut] Cut287
  Base = -> Cut280
  Tool = -> Compound236
FEATURE [Part::Compound] Compound231
  Links = -> [Cut287]
  Placement = pos=(0,0,-30) rot=(0,0,1;0rad)
FEATURE [Part::Cut] Cut289
  Base = -> Compound231
  Tool = -> Compound227
FEATURE [Part::Cut] Cut285
  Base = -> Cut289
  Tool = -> Compound228
FEATURE [Part::Cut] Cut281
  Base = -> Cut285
  Tool = -> Compound237
FEATURE [Part::Cut] Cut290
  Base = -> Cut281
  Placement = pos=(17,-127,10) rot=(1,0,0;1.5708rad)
  Tool = -> Compound230
FEATURE [Part::Cut] Cut291
  Base = -> Cut290
  Tool = -> Compound238
FEATURE [Part::Chamfer] Chamfer043
  Base = -> Cut291
  Edges = 1 edges r=3: [Edge17]
FEATURE [Part::Chamfer] Chamfer048
  Base = -> Chamfer043
  Edges = 1 edges r=3: [Edge33]
FEATURE [Part::Cut] Cut297
  Base = -> Chamfer048
  Placement = pos=(8,0,27) rot=(0,1,0;1.5708rad)
  Tool = -> Compound241
FEATURE [Part::Cut] Cut300
  Base = -> Compound247
  Tool = -> Compound246
FEATURE [Part::Chamfer] Chamfer049
  Base = -> Cut300
  Edges = 2 edges r=2: [Edge29,Edge31]
FEATURE [Part::Chamfer] Chamfer050
  Base = -> Chamfer049
  Edges = 2 edges r=2: [Edge26,Edge28]
FEATURE [Part::Cylinder] Cylinder2228  label="Válec2228"
  Angle = 360
  AttacherType = Attacher::AttachEngine3D
  Height = 20
  Placement = pos=(32,-108,18) rot=(0,1,0;1.5708rad)
  Radius = 1
FEATURE [Part::Cylinder] Cylinder2229  label="Válec2229"
  Angle = 360
  AttacherType = Attacher::AttachEngine3D
  Height = 20
  Placement = pos=(-17,-108,18) rot=(0,1,0;1.5708rad)
  Radius = 1
FEATURE [Part::Cylinder] Cylinder2230  label="Válec2230"
  Angle = 360
  AttacherType = Attacher::AttachEngine3D
  Height = 20
  Placement = pos=(32,-108,2) rot=(0,1,0;1.5708rad)
  Radius = 1
FEATURE [Part::Cylinder] Cylinder2231  label="Válec2231"
  Angle = 360
  AttacherType = Attacher::AttachEngine3D
  Height = 20
  Placement = pos=(-17,-108,2) rot=(0,1,0;1.5708rad)
  Radius = 1
FEATURE [Part::Box] Box862  label="Krychle861"
  AttacherType = Attacher::AttachEngine3D
  Height = 4
  Length = 4
  Placement = pos=(-7,-113,16) rot=(0,0,1;0rad)
  Width = 4
FEATURE [Part::Box] Box863  label="Krychle862"
  AttacherType = Attacher::AttachEngine3D
  Height = 4
  Length = 4
  Placement = pos=(-7,-113,0) rot=(0,0,1;0rad)
  Width = 4
FEATURE [Part::Box] Box864  label="Krychle863"
  AttacherType = Attacher::AttachEngine3D
  Height = 4
  Length = 4
  Placement = pos=(37,-113,16) rot=(0,0,1;0rad)
  Width = 4
FEATURE [Part::Box] Box865  label="Krychle864"
  AttacherType = Attacher::AttachEngine3D
  Height = 4
  Length = 4
  Placement = pos=(37,-113,0) rot=(0,0,1;0rad)
  Width = 4
FEATURE [Part::Compound] Compound1009
  Links = -> [Cylinder2230,Cylinder2228]
  Placement = pos=(0,-3,0) rot=(0,0,1;0rad)
FEATURE [Part::Compound] Compound1010
  Links = -> [Cylinder2231,Cylinder2229]
  Placement = pos=(0,-3,0) rot=(0,0,1;0rad)
FEATURE [Part::Compound] Compound1012
  Links = -> [Compound1009,Compound1010]
  Placement = pos=(0,-1.5,0) rot=(0,0,1;0rad)
FEATURE [Part::Compound] Compound1016
  Links = -> [Box862,Box863,Box864,Box865]
  Placement = pos=(0,-1.5,0) rot=(0,0,1;0rad)
FEATURE [Part::Cut] Cut831
  Base = -> Chamfer050
  Tool = -> Compound1012
FEATURE [Part::Cut] Cut832
  Base = -> Cut831
  Tool = -> Compound1016
FEATURE [Part::Compound] Compound1018  label="Wrist_moto-hold"
  Links = -> [Cut832,Cut297]
  Placement = pos=(-10,-170,20) rot=(0.707107,0,0.707107;3.14159rad)
FEATURE [Part::Torus] Torus001  label="Anuloid001"
  Angle1 = -180
  Angle2 = 180
  Angle3 = 360
  AttacherType = Attacher::AttachEngine3D
  Placement = pos=(17,-98,10) rot=(1,0,0;1.5708rad)
  Radius1 = 33.8
  Radius2 = 2
FEATURE [Part::Torus] Torus  label="Anuloid"
  Angle1 = -180
  Angle2 = 180
  Angle3 = 360
  AttacherType = Attacher::AttachEngine3D
  Placement = pos=(17,-98,10) rot=(1,0,0;1.5708rad)
  Radius1 = 33.8
  Radius2 = 2
FEATURE [Part::FeaturePython] Tube017  # WARN: FeaturePython — macro-defined, semantics opaque (R4)
  AttacherType = Attacher::AttachEngine3D
  Height = 12
  InnerRadius = 27
  OuterRadius = 34
  Placement = pos=(17,-92,10) rot=(1,0,0;1.5708rad)
FEATURE [Part::Box] Box326  label="Krychle326"
  AttacherType = Attacher::AttachEngine3D
  Height = 32
  Length = 5.85
  Placement = pos=(-10,-134,-6) rot=(0,0,1;0rad)
  Width = 56
FEATURE [Part::Box] Box327  label="Krychle327"
  AttacherType = Attacher::AttachEngine3D
  Height = 32
  Length = 5.85
  Placement = pos=(38.15,-134,-6) rot=(0,0,1;0rad)
  Width = 56
FEATURE [Part::Compound] Compound248
  Links = -> [Box326,Box327]
FEATURE [Part::Box] Box332  label="Krychle332"
  AttacherType = Attacher::AttachEngine3D
  Height = 12
  Length = 46.3
  Placement = pos=(-23.15,-23.15,-70) rot=(0,0,1;0rad)
  Width = 46.3
FEATURE [Part::Box] Box333  label="Krychle333"
  AttacherType = Attacher::AttachEngine3D
  Height = 12
  Length = 42.3
  Placement = pos=(-21.15,-21.15,-70) rot=(0,0,1;0rad)
  Width = 42.3
FEATURE [Part::Box] Box334  label="Krychle334"
  AttacherType = Attacher::AttachEngine3D
  Height = 12
  Length = 7
  Placement = pos=(-22,15,-74) rot=(0,0,1;0rad)
  Width = 7
FEATURE [Part::Cylinder] Cylinder512  label="Válec512"
  Angle = 360
  AttacherType = Attacher::AttachEngine3D
  Height = 12
  Placement = pos=(-15.15,15.15,-74) rot=(0,0,1;0rad)
  Radius = 6
FEATURE [Part::Box] Box335  label="Krychle335"
  AttacherType = Attacher::AttachEngine3D
  Height = 36
  Length = 7.85
  Placement = pos=(-10,-134,-8) rot=(0,0,1;0rad)
  Width = 56
FEATURE [Part::Box] Box336  label="Krychle336"
  AttacherType = Attacher::AttachEngine3D
  Height = 36
  Length = 7.85
  Placement = pos=(36.15,-134,-8) rot=(0,0,1;0rad)
  Width = 56
FEATURE [Part::Chamfer] Chamfer051
  Base = -> Compound248
  Edges = 2 edges r=2: [Edge2,Edge4]
FEATURE [Part::Chamfer] Chamfer052
  Base = -> Chamfer051
  Edges = 2 edges r=2: [Edge24,Edge26]
FEATURE [Part::Cut] Cut301
  Base = -> Tube017
  Tool = -> Chamfer052
FEATURE [Part::Compound] Compound253
  Links = -> [Box335,Box336]
FEATURE [Part::Cut] Cut308
  Base = -> Box332
  Placement = pos=(17,-32,10) rot=(-1,0,0;1.5708rad)
  Tool = -> Box333
FEATURE [Part::Cut] Cut309
  Base = -> Box334
  Placement = pos=(0,0,0) rot=(0,0,1;1.5708rad)
  Tool = -> Cylinder512
FEATURE [Part::Cut] Cut310
  Base = -> Box334
  Placement = pos=(0,0,0) rot=(0,0,-1;1.5708rad)
  Tool = -> Cylinder512
FEATURE [Part::Cut] Cut311
  Base = -> Box334
  Tool = -> Cylinder512
FEATURE [Part::Cut] Cut312
  Base = -> Box334
  Placement = pos=(0,0,0) rot=(0,0,1;3.14159rad)
  Tool = -> Cylinder512
FEATURE [Part::Compound] Compound251
  Links = -> [Cut311,Cut309,Cut312,Cut310]
  Placement = pos=(17,-28,10) rot=(-1,0,0;1.5708rad)
FEATURE [Part::Cut] Cut313
  Base = -> Compound251
  Tool = -> Compound253
FEATURE [Part::Cut] Cut315
  Base = -> Cut301
  Tool = -> Torus
FEATURE [Part::Box] Box337  label="Krychle337"
  AttacherType = Attacher::AttachEngine3D
  Height = 36
  Length = 7.85
  Placement = pos=(36.15,-134,-8) rot=(0,0,1;0rad)
  Width = 56
FEATURE [Part::Box] Box338  label="Krychle338"
  AttacherType = Attacher::AttachEngine3D
  Height = 36
  Length = 7.85
  Placement = pos=(-10,-134,-8) rot=(0,0,1;0rad)
  Width = 56
FEATURE [Part::Compound] Compound254
  Links = -> [Box338,Box337]
FEATURE [Part::Cut] Cut314
  Base = -> Cut308
  Tool = -> Compound254
FEATURE [Part::Compound] Compound255
  Links = -> [Cut313,Cut314]
  Placement = pos=(0,-2,0) rot=(0,0,1;0rad)
FEATURE [Part::Cut] Cut316
  Base = -> Compound255
  Placement = pos=(0,-2,0) rot=(0,0,1;0rad)
  Tool = -> Torus001
FEATURE [Part::Cylinder] Cylinder2200  label="Válec2200"
  Angle = 360
  AttacherType = Attacher::AttachEngine3D
  Height = 10
  Placement = pos=(17,-98,44) rot=(1,0,0;1.5708rad)
  Radius = 2
FEATURE [Part::Cut] Cut803
  Base = -> Cut315
  Tool = -> Cylinder2200
FEATURE [Part::Box] Box849  label="Krychle848"
  AttacherType = Attacher::AttachEngine3D
  Height = 28
  Length = 2
  Placement = pos=(-12,-112,-4) rot=(0,0,1;0rad)
  Width = 8
FEATURE [Part::Box] Box857  label="Krychle856"
  AttacherType = Attacher::AttachEngine3D
  Height = 28
  Length = 2
  Placement = pos=(44,-112,-4) rot=(0,0,1;0rad)
  Width = 8
FEATURE [Part::Cylinder] Cylinder2224  label="Válec2224"
  Angle = 360
  AttacherType = Attacher::AttachEngine3D
  Height = 20
  Placement = pos=(-17,-108,2) rot=(0,1,0;1.5708rad)
  Radius = 1
FEATURE [Part::Cylinder] Cylinder2225  label="Válec2225"
  Angle = 360
  AttacherType = Attacher::AttachEngine3D
  Height = 20
  Placement = pos=(-17,-108,18) rot=(0,1,0;1.5708rad)
  Radius = 1
FEATURE [Part::Cylinder] Cylinder2226  label="Válec2226"
  Angle = 360
  AttacherType = Attacher::AttachEngine3D
  Height = 20
  Placement = pos=(32,-108,2) rot=(0,1,0;1.5708rad)
  Radius = 1
FEATURE [Part::Cylinder] Cylinder2227  label="Válec2227"
  Angle = 360
  AttacherType = Attacher::AttachEngine3D
  Height = 20
  Placement = pos=(32,-108,18) rot=(0,1,0;1.5708rad)
  Radius = 1
FEATURE [Part::Compound] Compound994  label="wrist_halo_inner2"
  Links = -> [Box849,Box857,Cut803]
  Placement = pos=(0,-2,0) rot=(0,0,1;0rad)
FEATURE [Part::Compound] Compound995  label="wrist_halo_inner003"
  Links = -> [Cut316,Compound994]
FEATURE [Part::Compound] Compound1007
  Links = -> [Cylinder2226,Cylinder2227]
  Placement = pos=(0,-3,0) rot=(0,0,1;0rad)
FEATURE [Part::Compound] Compound1008
  Links = -> [Cylinder2224,Cylinder2225]
  Placement = pos=(0,-3,0) rot=(0,0,1;0rad)
FEATURE [Part::Compound] Compound1011
  Links = -> [Compound1007,Compound1008]
FEATURE [Part::Cut] Cut830  label="Wrist_inner-halo-old"
  Base = -> Compound995
  Placement = pos=(-9,-170,20) rot=(0.707107,0,0.707107;3.14159rad)
  Tool = -> Compound1011
FEATURE [Part::FeaturePython] Tube035  # WARN: FeaturePython — macro-defined, semantics opaque (R4)
  AttacherType = Attacher::AttachEngine3D
  Height = 2
  InnerRadius = 31
  OuterRadius = 39
  Placement = pos=(17,-103,10) rot=(1,0,0;1.5708rad)
FEATURE [Part::Box] Box850  label="Krychle849"
  AttacherType = Attacher::AttachEngine3D
  Height = 28
  Length = 2
  Placement = pos=(-14.1,-111,-4) rot=(0,0,1;0rad)
  Width = 7
FEATURE [Part::Box] Box851  label="Krychle850"
  AttacherType = Attacher::AttachEngine3D
  Height = 30
  Length = 4
  Placement = pos=(-16.1,-105,-5) rot=(0,0,1;0rad)
  Width = 2
FEATURE [Part::Box] Box852  label="Krychle851"
  AttacherType = Attacher::AttachEngine3D
  Height = 28.2
  Length = 2.2
  Placement = pos=(-12.1,-111,-4.1) rot=(0,0,1;0rad)
  Width = 10
FEATURE [Part::Cut] Cut807
  Base = -> Tube035
  Tool = -> Box852
FEATURE [Part::Compound] Compound985
  Links = -> [Box851,Cut807]
FEATURE [Part::Cylinder] Cylinder2203  label="Válec2203"
  Angle = 360
  AttacherType = Attacher::AttachEngine3D
  Height = 20
  Placement = pos=(-17,-108,2) rot=(0,1,0;1.5708rad)
  Radius = 1
FEATURE [Part::Cylinder] Cylinder2204  label="Válec2204"
  Angle = 360
  AttacherType = Attacher::AttachEngine3D
  Height = 20
  Placement = pos=(-17,-108,18) rot=(0,1,0;1.5708rad)
  Radius = 1
FEATURE [Part::Compound] Compound986
  Links = -> [Cylinder2203,Cylinder2204]
FEATURE [Part::Cut] Cut811
  Base = -> Box850
  Tool = -> Compound986
FEATURE [Part::Box] Box853  label="Krychle852"
  AttacherType = Attacher::AttachEngine3D
  Height = 28.2
  Length = 2.2
  Placement = pos=(43.9,-111,-4.1) rot=(0,0,1;0rad)
  Width = 10
FEATURE [Part::Cut] Cut810
  Base = -> Compound985
  Tool = -> Box853
FEATURE [Part::Box] Box855  label="Krychle854"
  AttacherType = Attacher::AttachEngine3D
  Height = 28
  Length = 2
  Placement = pos=(46.1,-111,-4) rot=(0,0,1;0rad)
  Width = 7
FEATURE [Part::Box] Box856  label="Krychle855"
  AttacherType = Attacher::AttachEngine3D
  Height = 30
  Length = 4
  Placement = pos=(46.1,-105,-5) rot=(0,0,1;0rad)
  Width = 2
FEATURE [Part::Cylinder] Cylinder2205  label="Válec2205"
  Angle = 360
  AttacherType = Attacher::AttachEngine3D
  Height = 20
  Placement = pos=(32,-108,2) rot=(0,1,0;1.5708rad)
  Radius = 1
FEATURE [Part::Cylinder] Cylinder2206  label="Válec2206"
  Angle = 360
  AttacherType = Attacher::AttachEngine3D
  Height = 20
  Placement = pos=(32,-108,18) rot=(0,1,0;1.5708rad)
  Radius = 1
FEATURE [Part::Compound] Compound988
  Links = -> [Cylinder2205,Cylinder2206]
FEATURE [Part::Cut] Cut809
  Base = -> Box855
  Tool = -> Compound988
FEATURE [Part::Chamfer] Chamfer068
  Base = -> Cut809
  Edges = 2 edges r=1.5: [Edge11,Edge13]
FEATURE [Part::Chamfer] Chamfer069
  Base = -> Cut811
  Edges = 2 edges r=1.5: [Edge2,Edge3]
FEATURE [Part::Compound] Compound989
  Links = -> [Chamfer069,Chamfer068,Cut810]
FEATURE [Part::Compound] Compound990  label="Wrist_halo-cover"
  Links = -> [Box856,Compound989]
  Placement = pos=(11,-167,54) rot=(0.707107,0,-0.707107;3.14159rad)
FEATURE [Part::Cylinder] Cylinder201  label="Válec201"
  Angle = 360
  AttacherType = Attacher::AttachEngine3D
  Height = 20
  Placement = pos=(13.08,-13.08,26) rot=(0,0,1;3.92699rad)
  Radius = 1
FEATURE [Part::Cylinder] Cylinder202  label="Válec202"
  Angle = 360
  AttacherType = Attacher::AttachEngine3D
  Height = 20
  Placement = pos=(0,18.5,26) rot=(0,0,1;0rad)
  Radius = 1
FEATURE [Part::Cylinder] Cylinder203  label="Válec203"
  Angle = 360
  AttacherType = Attacher::AttachEngine3D
  Height = 20
  Placement = pos=(-13.08,13.08,26) rot=(0,0,1;0.785398rad)
  Radius = 1
FEATURE [Part::Cylinder] Cylinder204  label="Válec204"
  Angle = 360
  AttacherType = Attacher::AttachEngine3D
  Height = 20
  Placement = pos=(-18.5,0,26) rot=(0,0,1;1.5708rad)
  Radius = 1
FEATURE [Part::Cylinder] Cylinder205  label="Válec205"
  Angle = 360
  AttacherType = Attacher::AttachEngine3D
  Height = 20
  Placement = pos=(-13.08,-13.08,26) rot=(0,0,1;2.35619rad)
  Radius = 1
FEATURE [Part::Cylinder] Cylinder206  label="Válec206"
  Angle = 360
  AttacherType = Attacher::AttachEngine3D
  Height = 20
  Placement = pos=(6e-15,-18.5,26) rot=(0,0,1;3.14159rad)
  Radius = 1
FEATURE [Part::Cylinder] Cylinder207  label="Válec207"
  Angle = 360
  AttacherType = Attacher::AttachEngine3D
  Height = 20
  Placement = pos=(18.5,8e-15,26) rot=(0,0,-1;1.5708rad)
  Radius = 1
FEATURE [Part::Cylinder] Cylinder208  label="Válec208"
  Angle = 360
  AttacherType = Attacher::AttachEngine3D
  Height = 20
  Placement = pos=(13.08,13.08,26) rot=(0,0,-1;0.785398rad)
  Radius = 1
FEATURE [Part::Compound] Compound070
  Links = -> [Cylinder202,Cylinder203,Cylinder204,Cylinder205,Cylinder206,Cylinder201,Cylinder207,Cylinder208]
FEATURE [Part::Cylinder] Cylinder209  label="Válec209"
  Angle = 360
  AttacherType = Attacher::AttachEngine3D
  Height = 20
  Placement = pos=(6e-15,-18.5,26) rot=(0,0,1;3.14159rad)
  Radius = 1
FEATURE [Part::Cylinder] Cylinder210  label="Válec210"
  Angle = 360
  AttacherType = Attacher::AttachEngine3D
  Height = 20
  Placement = pos=(13.08,-13.08,26) rot=(0,0,1;3.92699rad)
  Radius = 1
FEATURE [Part::Cylinder] Cylinder211  label="Válec211"
  Angle = 360
  AttacherType = Attacher::AttachEngine3D
  Height = 20
  Placement = pos=(-18.5,0,26) rot=(0,0,1;1.5708rad)
  Radius = 1
FEATURE [Part::Cylinder] Cylinder212  label="Válec212"
  Angle = 360
  AttacherType = Attacher::AttachEngine3D
  Height = 20
  Placement = pos=(-13.08,-13.08,26) rot=(0,0,1;2.35619rad)
  Radius = 1
FEATURE [Part::Cylinder] Cylinder213  label="Válec213"
  Angle = 360
  AttacherType = Attacher::AttachEngine3D
  Height = 20
  Placement = pos=(0,18.5,26) rot=(0,0,1;0rad)
  Radius = 1
FEATURE [Part::Cylinder] Cylinder214  label="Válec214"
  Angle = 360
  AttacherType = Attacher::AttachEngine3D
  Height = 20
  Placement = pos=(13.08,13.08,26) rot=(0,0,-1;0.785398rad)
  Radius = 1
FEATURE [Part::Cylinder] Cylinder215  label="Válec215"
  Angle = 360
  AttacherType = Attacher::AttachEngine3D
  Height = 20
  Placement = pos=(-13.08,13.08,26) rot=(0,0,1;0.785398rad)
  Radius = 1
FEATURE [Part::Cylinder] Cylinder216  label="Válec216"
  Angle = 360
  AttacherType = Attacher::AttachEngine3D
  Height = 20
  Placement = pos=(18.5,8e-15,26) rot=(0,0,-1;1.5708rad)
  Radius = 1
FEATURE [Part::Compound] Compound071
  Links = -> [Cylinder213,Cylinder215,Cylinder211,Cylinder212,Cylinder209,Cylinder210,Cylinder216,Cylinder214]
FEATURE [Part::Cylinder] Cylinder217  label="Válec217"
  Angle = 360
  AttacherType = Attacher::AttachEngine3D
  Height = 2
  Placement = pos=(-13.08,13.08,26) rot=(0,0,1;0.785398rad)
  Radius = 2
FEATURE [Part::Cylinder] Cylinder218  label="Válec218"
  Angle = 360
  AttacherType = Attacher::AttachEngine3D
  Height = 2
  Placement = pos=(0,18.5,26) rot=(0,0,1;0rad)
  Radius = 2
FEATURE [Part::Cylinder] Cylinder219  label="Válec219"
  Angle = 360
  AttacherType = Attacher::AttachEngine3D
  Height = 2
  Placement = pos=(-13.08,-13.08,26) rot=(0,0,1;2.35619rad)
  Radius = 2
FEATURE [Part::Cylinder] Cylinder220  label="Válec220"
  Angle = 360
  AttacherType = Attacher::AttachEngine3D
  Height = 2
  Placement = pos=(6e-15,-18.5,26) rot=(0,0,1;3.14159rad)
  Radius = 2
FEATURE [Part::Cylinder] Cylinder221  label="Válec221"
  Angle = 360
  AttacherType = Attacher::AttachEngine3D
  Height = 2
  Placement = pos=(13.08,-13.08,26) rot=(0,0,1;3.92699rad)
  Radius = 2
FEATURE [Part::Cylinder] Cylinder222  label="Válec222"
  Angle = 360
  AttacherType = Attacher::AttachEngine3D
  Height = 2
  Placement = pos=(-18.5,0,26) rot=(0,0,1;1.5708rad)
  Radius = 2
FEATURE [Part::Cylinder] Cylinder223  label="Válec223"
  Angle = 360
  AttacherType = Attacher::AttachEngine3D
  Height = 2
  Placement = pos=(13.08,13.08,26) rot=(0,0,-1;0.785398rad)
  Radius = 2
FEATURE [Part::Cylinder] Cylinder224  label="Válec224"
  Angle = 360
  AttacherType = Attacher::AttachEngine3D
  Height = 2
  Placement = pos=(18.5,8e-15,26) rot=(0,0,-1;1.5708rad)
  Radius = 2
FEATURE [Part::Compound] Compound072
  Links = -> [Cylinder218,Cylinder217,Cylinder222,Cylinder219,Cylinder220,Cylinder221,Cylinder224,Cylinder223]
  Placement = pos=(0,0,14) rot=(0,0,1;0rad)
FEATURE [Part::Cylinder] Cylinder225  label="Válec225"
  Angle = 360
  AttacherType = Attacher::AttachEngine3D
  Height = 2
  Placement = pos=(0,0,40) rot=(0,0,1;0rad)
  Radius = 25
FEATURE [Part::Cylinder] Cylinder226  label="Válec226"
  Angle = 360
  AttacherType = Attacher::AttachEngine3D
  Height = 2
  Placement = pos=(-13.08,-13.08,26) rot=(0,0,1;2.35619rad)
  Radius = 2
FEATURE [Part::Cylinder] Cylinder227  label="Válec227"
  Angle = 360
  AttacherType = Attacher::AttachEngine3D
  Height = 2
  Placement = pos=(-13.08,13.08,26) rot=(0,0,1;0.785398rad)
  Radius = 2
FEATURE [Part::Cylinder] Cylinder228  label="Válec228"
  Angle = 360
  AttacherType = Attacher::AttachEngine3D
  Height = 2
  Placement = pos=(0,18.5,26) rot=(0,0,1;0rad)
  Radius = 2
FEATURE [Part::Cylinder] Cylinder229  label="Válec229"
  Angle = 360
  AttacherType = Attacher::AttachEngine3D
  Height = 2
  Placement = pos=(13.08,13.08,26) rot=(0,0,-1;0.785398rad)
  Radius = 2
FEATURE [Part::Cylinder] Cylinder230  label="Válec230"
  Angle = 360
  AttacherType = Attacher::AttachEngine3D
  Height = 2
  Placement = pos=(18.5,8e-15,26) rot=(0,0,-1;1.5708rad)
  Radius = 2
FEATURE [Part::Cylinder] Cylinder231  label="Válec231"
  Angle = 360
  AttacherType = Attacher::AttachEngine3D
  Height = 2
  Placement = pos=(13.08,-13.08,26) rot=(0,0,1;3.92699rad)
  Radius = 2
FEATURE [Part::FeaturePython] Tube033  # WARN: FeaturePython — macro-defined, semantics opaque (R4)
  AttacherType = Attacher::AttachEngine3D
  Height = 4
  InnerRadius = 17
  OuterRadius = 21
  Placement = pos=(0,0,28) rot=(0,0,1;0rad)
FEATURE [Part::FeaturePython] Tube034  # WARN: FeaturePython — macro-defined, semantics opaque (R4)
  AttacherType = Attacher::AttachEngine3D
  Height = 8
  InnerRadius = 17
  OuterRadius = 25
  Placement = pos=(0,0,32) rot=(0,0,1;0rad)
FEATURE [Part::Cut] Cut068
  Base = -> Tube034
  Tool = -> Compound072
FEATURE [Part::Cut] Cut069
  Base = -> Cut068
  Tool = -> Compound071
FEATURE [Part::Cut] Cut070
  Base = -> Tube033
  Tool = -> Compound070
FEATURE [Part::Cylinder] Cylinder232  label="Válec232"
  Angle = 360
  AttacherType = Attacher::AttachEngine3D
  Height = 2
  Placement = pos=(6e-15,-18.5,26) rot=(0,0,1;3.14159rad)
  Radius = 2
FEATURE [Part::Cylinder] Cylinder233  label="Válec233"
  Angle = 360
  AttacherType = Attacher::AttachEngine3D
  Height = 2
  Placement = pos=(-18.5,0,26) rot=(0,0,1;1.5708rad)
  Radius = 2
FEATURE [Part::Compound] Compound073
  Links = -> [Cylinder228,Cylinder227,Cylinder233,Cylinder226,Cylinder232,Cylinder231,Cylinder230,Cylinder229]
  Placement = pos=(0,0,14) rot=(0,0,1;0rad)
FEATURE [Part::Cut] Cut071
  Base = -> Cylinder225
  Tool = -> Compound073
FEATURE [Part::Cylinder] Cylinder235  label="Válec235"
  Angle = 360
  AttacherType = Attacher::AttachEngine3D
  Height = 60
  Placement = pos=(-8.41904,20.3253,34) rot=(0,0,1;0.392699rad)
  Radius = 1.5
FEATURE [Part::Cylinder] Cylinder236  label="Válec236"
  Angle = 360
  AttacherType = Attacher::AttachEngine3D
  Height = 60
  Placement = pos=(-20.3253,-8.41904,34) rot=(0,0,1;1.96349rad)
  Radius = 1.5
FEATURE [Part::Cylinder] Cylinder237  label="Válec237"
  Angle = 360
  AttacherType = Attacher::AttachEngine3D
  Height = 60
  Placement = pos=(8.41904,-20.3253,34) rot=(0,0,1;3.53429rad)
  Radius = 1.5
FEATURE [Part::Cylinder] Cylinder238  label="Válec238"
  Angle = 360
  AttacherType = Attacher::AttachEngine3D
  Height = 60
  Placement = pos=(20.3253,8.41904,34) rot=(0,0,-1;1.1781rad)
  Radius = 1.5
FEATURE [Part::Compound] Compound074
  Links = -> [Cylinder235,Cylinder236,Cylinder237,Cylinder238]
FEATURE [Part::Cut] Cut072
  Base = -> Cut071
  Tool = -> Compound074
FEATURE [Part::Box] Box066  label="Krychle066"
  AttacherType = Attacher::AttachEngine3D
  Height = 2
  Length = 6
  Placement = pos=(-10.0426,16.4057,36) rot=(0,0,1;0.392699rad)
  Width = 6
FEATURE [Part::Box] Box067  label="Krychle067"
  AttacherType = Attacher::AttachEngine3D
  Height = 2
  Length = 6
  Placement = pos=(-16.4057,-10.0426,36) rot=(0,0,1;1.96349rad)
  Width = 6
FEATURE [Part::Box] Box068  label="Krychle068"
  AttacherType = Attacher::AttachEngine3D
  Height = 2
  Length = 6
  Placement = pos=(10.0426,-16.4057,36) rot=(0,0,1;3.53429rad)
  Width = 6
FEATURE [Part::Box] Box069  label="Krychle069"
  AttacherType = Attacher::AttachEngine3D
  Height = 2
  Length = 6
  Placement = pos=(16.4057,10.0426,36) rot=(0,0,-1;1.1781rad)
  Width = 6
FEATURE [Part::Cylinder] Cylinder239  label="Válec239"
  Angle = 360
  AttacherType = Attacher::AttachEngine3D
  Height = 60
  Placement = pos=(-8.41904,20.3253,34) rot=(0,0,1;0.392699rad)
  Radius = 1.5
FEATURE [Part::Cylinder] Cylinder240  label="Válec240"
  Angle = 360
  AttacherType = Attacher::AttachEngine3D
  Height = 60
  Placement = pos=(20.3253,8.41904,34) rot=(0,0,-1;1.1781rad)
  Radius = 1.5
FEATURE [Part::Cylinder] Cylinder241  label="Válec241"
  Angle = 360
  AttacherType = Attacher::AttachEngine3D
  Height = 60
  Placement = pos=(-20.3253,-8.41904,34) rot=(0,0,1;1.96349rad)
  Radius = 1.5
FEATURE [Part::Cylinder] Cylinder242  label="Válec242"
  Angle = 360
  AttacherType = Attacher::AttachEngine3D
  Height = 60
  Placement = pos=(8.41904,-20.3253,34) rot=(0,0,1;3.53429rad)
  Radius = 1.5
FEATURE [Part::Compound] Compound075
  Links = -> [Box069,Box068,Box067,Box066]
FEATURE [Part::Compound] Compound076
  Links = -> [Cylinder239,Cylinder241,Cylinder242,Cylinder240]
FEATURE [Part::Cut] Cut073
  Base = -> Cut069
  Tool = -> Compound076
FEATURE [Part::Cut] Cut074
  Base = -> Cut073
  Tool = -> Compound075
FEATURE [Part::Compound] Compound077  label="G-mini_actuator-drum-old"
  Links = -> [Cut070,Cut072,Cut074]
  Placement = pos=(0,10,37) rot=(0.962637,-0.19148,0.19148;1.60885rad)
FEATURE [Part::Torus] Torus003  label="Anuloid003"
  Angle1 = -180
  Angle2 = 180
  Angle3 = 360
  AttacherType = Attacher::AttachEngine3D
  Placement = pos=(0,0,23.5) rot=(0,0,1;0rad)
  Radius1 = 20
  Radius2 = 2.2
FEATURE [Part::FeaturePython] Tube004  # WARN: FeaturePython — macro-defined, semantics opaque (R4)
  AttacherType = Attacher::AttachEngine3D
  Height = 20
  InnerRadius = 21
  OuterRadius = 25
  Placement = pos=(0,0,10) rot=(0,0,1;0rad)
FEATURE [Part::Cut] Cut018
  Base = -> Tube004
  Tool = -> Torus003
FEATURE [Part::Cylinder] Cylinder061  label="Válec061"
  Angle = 360
  AttacherType = Attacher::AttachEngine3D
  Height = 10
  Placement = pos=(20,0,23.5) rot=(0,0,1;0rad)
  Radius = 2.2
FEATURE [Part::Cylinder] Cylinder062  label="Válec062"
  Angle = 360
  AttacherType = Attacher::AttachEngine3D
  Height = 10
  Placement = pos=(0,23,8) rot=(0,0,1;0rad)
  Radius = 1
FEATURE [Part::Cylinder] Cylinder063  label="Válec063"
  Angle = 360
  AttacherType = Attacher::AttachEngine3D
  Height = 10
  Placement = pos=(-16.26,16.26,8) rot=(0,0,1;0.785398rad)
  Radius = 1
FEATURE [Part::Cylinder] Cylinder064  label="Válec064"
  Angle = 360
  AttacherType = Attacher::AttachEngine3D
  Height = 10
  Placement = pos=(-23,0,8) rot=(0,0,1;1.5708rad)
  Radius = 1
FEATURE [Part::Cylinder] Cylinder065  label="Válec065"
  Angle = 360
  AttacherType = Attacher::AttachEngine3D
  Height = 10
  Placement = pos=(-16.26,-16.26,8) rot=(0,0,1;2.35619rad)
  Radius = 1
FEATURE [Part::Cylinder] Cylinder066  label="Válec066"
  Angle = 360
  AttacherType = Attacher::AttachEngine3D
  Height = 10
  Placement = pos=(4e-15,-23,8) rot=(0,0,1;3.14159rad)
  Radius = 1
FEATURE [Part::Cylinder] Cylinder067  label="Válec067"
  Angle = 360
  AttacherType = Attacher::AttachEngine3D
  Height = 10
  Placement = pos=(16.26,-16.26,8) rot=(0,0,1;3.92699rad)
  Radius = 1
FEATURE [Part::Cylinder] Cylinder068  label="Válec068"
  Angle = 360
  AttacherType = Attacher::AttachEngine3D
  Height = 10
  Placement = pos=(23,1.1e-14,8) rot=(0,0,-1;1.5708rad)
  Radius = 1
FEATURE [Part::Cylinder] Cylinder069  label="Válec069"
  Angle = 360
  AttacherType = Attacher::AttachEngine3D
  Height = 10
  Placement = pos=(16.26,16.26,8) rot=(0,0,-1;0.785398rad)
  Radius = 1
FEATURE [Part::Box] Box016  label="Krychle016"
  AttacherType = Attacher::AttachEngine3D
  Height = 1.4
  Length = 4
  Placement = pos=(-2,21,14) rot=(0,0,1;0rad)
  Width = 4
FEATURE [Part::Box] Box017  label="Krychle017"
  AttacherType = Attacher::AttachEngine3D
  Height = 1.4
  Length = 4
  Placement = pos=(-16.2635,13.435,14) rot=(0,0,1;0.785398rad)
  Width = 4
FEATURE [Part::Box] Box018  label="Krychle018"
  AttacherType = Attacher::AttachEngine3D
  Height = 1.4
  Length = 4
  Placement = pos=(-21,-2,14) rot=(0,0,1;1.5708rad)
  Width = 4
FEATURE [Part::Box] Box019  label="Krychle019"
  AttacherType = Attacher::AttachEngine3D
  Height = 1.4
  Length = 4
  Placement = pos=(-13.435,-16.2635,14) rot=(0,0,1;2.35619rad)
  Width = 4
FEATURE [Part::Box] Box020  label="Krychle020"
  AttacherType = Attacher::AttachEngine3D
  Height = 1.4
  Length = 4
  Placement = pos=(2,-21,14) rot=(0,0,1;3.14159rad)
  Width = 4
FEATURE [Part::Box] Box021  label="Krychle021"
  AttacherType = Attacher::AttachEngine3D
  Height = 1.4
  Length = 4
  Placement = pos=(16.2635,-13.435,14) rot=(0,0,1;3.92699rad)
  Width = 4
FEATURE [Part::Box] Box022  label="Krychle022"
  AttacherType = Attacher::AttachEngine3D
  Height = 1.4
  Length = 4
  Placement = pos=(21,2,14) rot=(0,0,-1;1.5708rad)
  Width = 4
FEATURE [Part::Box] Box023  label="Krychle023"
  AttacherType = Attacher::AttachEngine3D
  Height = 1.4
  Length = 4
  Placement = pos=(13.435,16.2635,14) rot=(0,0,-1;0.785398rad)
  Width = 4
FEATURE [Part::Compound] Compound019
  Links = -> [Cylinder062,Cylinder069,Cylinder068,Cylinder066,Cylinder067,Cylinder065,Cylinder063,Cylinder064]
FEATURE [Part::Compound] Compound020
  Links = -> [Box016,Box017,Box018,Box019,Box020,Box021,Box022,Box023]
FEATURE [Part::Cut] Cut019
  Base = -> Cut018
  Tool = -> Compound020
FEATURE [Part::Cut] Cut020
  Base = -> Cut019
  Tool = -> Compound019
FEATURE [Part::Cut] Cut021  label="G-mini_bearing-ring"
  Base = -> Cut020
  Placement = pos=(1,22,37) rot=(1,0,0;1.5708rad)
  Tool = -> Cylinder061
FEATURE [Part::FeaturePython] Tube005  # WARN: FeaturePython — macro-defined, semantics opaque (R4)
  AttacherType = Attacher::AttachEngine3D
  Height = 6
  InnerRadius = 20
  OuterRadius = 25
  Placement = pos=(0,0,4) rot=(0,0,1;0rad)
FEATURE [Part::FeaturePython] Tube006  # WARN: FeaturePython — macro-defined, semantics opaque (R4)
  AttacherType = Attacher::AttachEngine3D
  Height = 6
  InnerRadius = 17
  OuterRadius = 21
  Placement = pos=(0,0,-16) rot=(0,0,1;0rad)
FEATURE [Part::Cylinder] Cylinder084  label="Válec084"
  Angle = 360
  AttacherType = Attacher::AttachEngine3D
  Height = 10
  Placement = pos=(0,23,4) rot=(0,0,1;0rad)
  Radius = 1
FEATURE [Part::Box] Box033  label="Krychle033"
  AttacherType = Attacher::AttachEngine3D
  Height = 6
  Length = 4
  Placement = pos=(10,17,5) rot=(0,0,1;0rad)
  Width = 1.4
FEATURE [Part::Box] Box034  label="Krychle034"
  AttacherType = Attacher::AttachEngine3D
  Height = 6
  Length = 4
  Placement = pos=(-14,17,5) rot=(0,0,1;0rad)
  Width = 1.4
FEATURE [Part::Cylinder] Cylinder077  label="Válec077"
  Angle = 360
  AttacherType = Attacher::AttachEngine3D
  Height = 10
  Placement = pos=(12,25,8) rot=(1,0,0;1.5708rad)
  Radius = 1
FEATURE [Part::Cylinder] Cylinder078  label="Válec078"
  Angle = 360
  AttacherType = Attacher::AttachEngine3D
  Height = 10
  Placement = pos=(-12,25,8) rot=(1,0,0;1.5708rad)
  Radius = 1
FEATURE [Part::Cylinder] Cylinder079  label="Válec079"
  Angle = 360
  AttacherType = Attacher::AttachEngine3D
  Height = 10
  Placement = pos=(16.2635,16.2635,4) rot=(0,0,-1;0.785398rad)
  Radius = 1
FEATURE [Part::Cylinder] Cylinder080  label="Válec080"
  Angle = 360
  AttacherType = Attacher::AttachEngine3D
  Height = 10
  Placement = pos=(16.2635,-16.2635,4) rot=(0,0,1;3.92699rad)
  Radius = 1
FEATURE [Part::Cylinder] Cylinder081  label="Válec081"
  Angle = 360
  AttacherType = Attacher::AttachEngine3D
  Height = 10
  Placement = pos=(-16.2635,16.2635,4) rot=(0,0,1;0.785398rad)
  Radius = 1
FEATURE [Part::Cylinder] Cylinder082  label="Válec082"
  Angle = 360
  AttacherType = Attacher::AttachEngine3D
  Height = 2
  Placement = pos=(-16.2635,-16.2635,4) rot=(0,0,1;2.35619rad)
  Radius = 2
FEATURE [Part::Cylinder] Cylinder083  label="Válec083"
  Angle = 360
  AttacherType = Attacher::AttachEngine3D
  Height = 10
  Placement = pos=(-23,-1e-15,4) rot=(0,0,1;1.5708rad)
  Radius = 1
FEATURE [Part::Compound] Compound026
  Links = -> [Box033,Box034]
FEATURE [Part::Compound] Compound033
  Links = -> [Cylinder077,Cylinder078]
FEATURE [Part::Cylinder] Cylinder085  label="Válec085"
  Angle = 360
  AttacherType = Attacher::AttachEngine3D
  Height = 10
  Placement = pos=(-16.2635,-16.2635,4) rot=(0,0,1;2.35619rad)
  Radius = 1
FEATURE [Part::Cylinder] Cylinder086  label="Válec086"
  Angle = 360
  AttacherType = Attacher::AttachEngine3D
  Height = 2
  Placement = pos=(0,23,4) rot=(0,0,1;0rad)
  Radius = 2
FEATURE [Part::Cylinder] Cylinder087  label="Válec087"
  Angle = 360
  AttacherType = Attacher::AttachEngine3D
  Height = 10
  Placement = pos=(23,1.1e-14,4) rot=(0,0,-1;1.5708rad)
  Radius = 1
FEATURE [Part::Cylinder] Cylinder088  label="Válec088"
  Angle = 360
  AttacherType = Attacher::AttachEngine3D
  Height = 2
  Placement = pos=(-23,-1e-15,4) rot=(0,0,1;1.5708rad)
  Radius = 2
FEATURE [Part::Cylinder] Cylinder089  label="Válec089"
  Angle = 360
  AttacherType = Attacher::AttachEngine3D
  Height = 10
  Placement = pos=(4e-15,-23,4) rot=(0,0,1;3.14159rad)
  Radius = 1
FEATURE [Part::Compound] Compound027
  Links = -> [Cylinder084,Cylinder081,Cylinder083,Cylinder085,Cylinder089,Cylinder080,Cylinder087,Cylinder079]
FEATURE [Part::Cylinder] Cylinder090  label="Válec090"
  Angle = 360
  AttacherType = Attacher::AttachEngine3D
  Height = 2
  Placement = pos=(16.2635,-16.2635,4) rot=(0,0,1;3.92699rad)
  Radius = 2
FEATURE [Part::Cylinder] Cylinder091  label="Válec091"
  Angle = 360
  AttacherType = Attacher::AttachEngine3D
  Height = 2
  Placement = pos=(23,1.1e-14,4) rot=(0,0,-1;1.5708rad)
  Radius = 2
FEATURE [Part::Cylinder] Cylinder092  label="Válec092"
  Angle = 360
  AttacherType = Attacher::AttachEngine3D
  Height = 2
  Placement = pos=(16.2635,16.2635,4) rot=(0,0,-1;0.785398rad)
  Radius = 2
FEATURE [Part::Cylinder] Cylinder093  label="Válec093"
  Angle = 360
  AttacherType = Attacher::AttachEngine3D
  Height = 2
  Placement = pos=(-16.2635,16.2635,4) rot=(0,0,1;0.785398rad)
  Radius = 2
FEATURE [Part::Cylinder] Cylinder094  label="Válec094"
  Angle = 360
  AttacherType = Attacher::AttachEngine3D
  Height = 2
  Placement = pos=(4e-15,-23,4) rot=(0,0,1;3.14159rad)
  Radius = 2
FEATURE [Part::Compound] Compound028
  Links = -> [Cylinder086,Cylinder093,Cylinder088,Cylinder082,Cylinder094,Cylinder090,Cylinder091,Cylinder092]
FEATURE [Part::Cut] Cut026
  Base = -> Tube005
  Tool = -> Compound028
FEATURE [Part::Cut] Cut027
  Base = -> Cut026
  Tool = -> Compound027
FEATURE [Part::Cut] Cut032
  Base = -> Cut027
  Tool = -> Compound026
FEATURE [Part::Box] Box035  label="Krychle035"
  AttacherType = Attacher::AttachEngine3D
  Height = 1.4
  Length = 4
  Placement = pos=(-2,17,-13) rot=(0,0,1;0rad)
  Width = 4
FEATURE [Part::Box] Box036  label="Krychle036"
  AttacherType = Attacher::AttachEngine3D
  Height = 1.4
  Length = 4
  Placement = pos=(-13.435,10.6066,-13) rot=(0,0,1;0.785398rad)
  Width = 4
FEATURE [Part::Box] Box037  label="Krychle037"
  AttacherType = Attacher::AttachEngine3D
  Height = 1.4
  Length = 4
  Placement = pos=(-10.6066,-13.435,-13) rot=(0,0,1;2.35619rad)
  Width = 4
FEATURE [Part::Box] Box038  label="Krychle038"
  AttacherType = Attacher::AttachEngine3D
  Height = 1.4
  Length = 4
  Placement = pos=(2,-17,-13) rot=(0,0,1;3.14159rad)
  Width = 4
FEATURE [Part::Cylinder] Cylinder095  label="Válec095"
  Angle = 360
  AttacherType = Attacher::AttachEngine3D
  Height = 10
  Placement = pos=(0,19,-20) rot=(0,0,1;0rad)
  Radius = 1
FEATURE [Part::Box] Box039  label="Krychle039"
  AttacherType = Attacher::AttachEngine3D
  Height = 1.4
  Length = 4
  Placement = pos=(-17,-2,-13) rot=(0,0,1;1.5708rad)
  Width = 4
FEATURE [Part::Box] Box040  label="Krychle040"
  AttacherType = Attacher::AttachEngine3D
  Height = 1.4
  Length = 4
  Placement = pos=(13.435,-10.6066,-13) rot=(0,0,1;3.92699rad)
  Width = 4
FEATURE [Part::Box] Box041  label="Krychle041"
  AttacherType = Attacher::AttachEngine3D
  Height = 1.4
  Length = 4
  Placement = pos=(10.6066,13.435,-13) rot=(0,0,-1;0.785398rad)
  Width = 4
FEATURE [Part::Cylinder] Cylinder096  label="Válec096"
  Angle = 360
  AttacherType = Attacher::AttachEngine3D
  Height = 10
  Placement = pos=(-13.435,13.435,-20) rot=(0,0,1;0.785398rad)
  Radius = 1
FEATURE [Part::Cylinder] Cylinder097  label="Válec097"
  Angle = 360
  AttacherType = Attacher::AttachEngine3D
  Height = 10
  Placement = pos=(-19,-1e-15,-20) rot=(0,0,1;1.5708rad)
  Radius = 1
FEATURE [Part::Cylinder] Cylinder098  label="Válec098"
  Angle = 360
  AttacherType = Attacher::AttachEngine3D
  Height = 10
  Placement = pos=(-13.435,-13.435,-20) rot=(0,0,1;2.35619rad)
  Radius = 1
FEATURE [Part::Cylinder] Cylinder099  label="Válec099"
  Angle = 360
  AttacherType = Attacher::AttachEngine3D
  Height = 10
  Placement = pos=(6e-15,-19,-20) rot=(0,0,1;3.14159rad)
  Radius = 1
FEATURE [Part::Cylinder] Cylinder100  label="Válec100"
  Angle = 360
  AttacherType = Attacher::AttachEngine3D
  Height = 10
  Placement = pos=(13.435,-13.435,-20) rot=(0,0,1;3.92699rad)
  Radius = 1
FEATURE [Part::Box] Box042  label="Krychle042"
  AttacherType = Attacher::AttachEngine3D
  Height = 1.4
  Length = 4
  Placement = pos=(17,2,-13) rot=(0,0,-1;1.5708rad)
  Width = 4
FEATURE [Part::Compound] Compound029
  Links = -> [Box035,Box036,Box039,Box037,Box038,Box040,Box042,Box041]
FEATURE [Part::Cut] Cut028
  Base = -> Tube006
  Tool = -> Compound029
FEATURE [Part::Cylinder] Cylinder101  label="Válec101"
  Angle = 360
  AttacherType = Attacher::AttachEngine3D
  Height = 10
  Placement = pos=(19,8e-15,-20) rot=(0,0,-1;1.5708rad)
  Radius = 1
FEATURE [Part::Cylinder] Cylinder102  label="Válec102"
  Angle = 360
  AttacherType = Attacher::AttachEngine3D
  Height = 10
  Placement = pos=(13.435,13.435,-20) rot=(0,0,-1;0.785398rad)
  Radius = 1
FEATURE [Part::Compound] Compound030
  Links = -> [Cylinder095,Cylinder096,Cylinder097,Cylinder098,Cylinder099,Cylinder100,Cylinder101,Cylinder102]
FEATURE [Part::Cut] Cut029
  Base = -> Cut028
  Tool = -> Compound030
FEATURE [Part::Cylinder] Cylinder103  label="Válec103"
  Angle = 360
  AttacherType = Attacher::AttachEngine3D
  Height = 10
  Radius = 21
FEATURE [Part::Cylinder] Cylinder104  label="Válec104"
  Angle = 360
  AttacherType = Attacher::AttachEngine3D
  Height = 10
  Radius = 21
FEATURE [Part::Box] Box043  label="Krychle043"
  AttacherType = Attacher::AttachEngine3D
  Height = 6
  Length = 4
  Placement = pos=(10,17,5) rot=(0,0,1;0rad)
  Width = 1.4
FEATURE [Part::Box] Box044  label="Krychle044"
  AttacherType = Attacher::AttachEngine3D
  Height = 6
  Length = 4
  Placement = pos=(-14,17,5) rot=(0,0,1;0rad)
  Width = 1.4
FEATURE [Part::Compound] Compound032
  Links = -> [Box043,Box044]
FEATURE [Part::Cylinder] Cylinder105  label="Válec105"
  Angle = 360
  AttacherType = Attacher::AttachEngine3D
  Height = 10
  Placement = pos=(-12,25,8) rot=(1,0,0;1.5708rad)
  Radius = 1
FEATURE [Part::Cylinder] Cylinder106  label="Válec106"
  Angle = 360
  AttacherType = Attacher::AttachEngine3D
  Height = 10
  Placement = pos=(12,25,8) rot=(1,0,0;1.5708rad)
  Radius = 1
FEATURE [Part::Compound] Compound034
  Links = -> [Cylinder106,Cylinder105]
FEATURE [Part::Cut] Cut035
  Base = -> Cut032
  Tool = -> Compound034
FEATURE [Part::Box] Box045  label="Krychle045"
  AttacherType = Attacher::AttachEngine3D
  Height = 4
  Length = 1.4
  Placement = pos=(-7.4,15,-16) rot=(0,0,1;0rad)
  Width = 6
FEATURE [Part::Cylinder] Cylinder107  label="Válec107"
  Angle = 360
  AttacherType = Attacher::AttachEngine3D
  Height = 16
  Placement = pos=(4,18,-14) rot=(0,1,0;1.5708rad)
  Radius = 1
FEATURE [Part::Cylinder] Cylinder108  label="Válec108"
  Angle = 360
  AttacherType = Attacher::AttachEngine3D
  Height = 16
  Placement = pos=(-20,18,-14) rot=(0,1,0;1.5708rad)
  Radius = 1
FEATURE [Part::Compound] Compound036
  Links = -> [Cylinder108,Cylinder107]
FEATURE [Part::Box] Box046  label="Krychle046"
  AttacherType = Attacher::AttachEngine3D
  Height = 4
  Length = 1.4
  Placement = pos=(6,15,-16) rot=(0,0,1;0rad)
  Width = 6
FEATURE [Part::Compound] Compound035
  Links = -> [Box045,Box046]
FEATURE [Part::Cut] Cut036
  Base = -> Cut029
  Tool = -> Compound035
FEATURE [Part::Cut] Cut037
  Base = -> Cut036
  Tool = -> Compound036
FEATURE [Part::FeaturePython] wormgear039  # WARN: FeaturePython — macro-defined, semantics opaque (R4)
  AttacherType = Attacher::AttachEngine3D
  Placement = pos=(0,0,0) rot=(0,0,1;1.13796rad)
  beta = 36.4444
  clearance = 0.25
  diameter = 32.5
  head = 0
  height = 12
  module = 0.8
  pressure_angle = 20
  reverse_pitch = false
  teeth = 30
  version = 0.0.3
FEATURE [Part::Cut] Cut030
  Base = -> Cylinder104
  Placement = pos=(0,0,-10) rot=(0,0,1;0rad)
  Tool = -> wormgear039
FEATURE [Part::FeaturePython] wormgear040  # WARN: FeaturePython — macro-defined, semantics opaque (R4)
  AttacherType = Attacher::AttachEngine3D
  Placement = pos=(0,0,0) rot=(0,0,1;1.13446rad)
  beta = 36.4444
  clearance = 0.25
  diameter = 32.5
  head = 0
  height = 12
  module = 0.8
  pressure_angle = 20
  reverse_pitch = true
  teeth = 30
  version = 0.0.3
FEATURE [Part::Cut] Cut031
  Base = -> Cylinder103
  Tool = -> wormgear040
FEATURE [Part::Compound] Compound031  label="gearovina-mini_okruh001"
  Links = -> [Cut030,Cut031]
FEATURE [Part::Cut] Cut033
  Base = -> Compound031
  Tool = -> Compound032
FEATURE [Part::Cut] Cut034
  Base = -> Cut033
  Tool = -> Compound033
FEATURE [Part::Compound] Compound037  label="G-mini_monoblock"
  Links = -> [Cut035,Cut037,Cut034]
  Placement = pos=(1,22,37) rot=(1,0,0;1.5708rad)
FEATURE [Part::FeaturePython] Tube032  # WARN: FeaturePython — macro-defined, semantics opaque (R4)
  AttacherType = Attacher::AttachEngine3D
  Height = 6
  InnerRadius = 17
  OuterRadius = 21
  Placement = pos=(0,0,-22) rot=(0,0,1;0rad)
FEATURE [Part::Box] Box055  label="Krychle055"
  AttacherType = Attacher::AttachEngine3D
  Height = 4
  Length = 46.3
  Placement = pos=(-23.15,-23.15,-25) rot=(0,0,1;0rad)
  Width = 46.3
FEATURE [Part::Cylinder] Cylinder168  label="Válec168"
  Angle = 360
  AttacherType = Attacher::AttachEngine3D
  Height = 10
  Placement = pos=(-13.44,13.44,-24) rot=(0,0,1;0.785398rad)
  Radius = 1
FEATURE [Part::Cylinder] Cylinder169  label="Válec169"
  Angle = 360
  AttacherType = Attacher::AttachEngine3D
  Height = 10
  Placement = pos=(-19,0,-24) rot=(0,0,1;1.5708rad)
  Radius = 1
FEATURE [Part::Cylinder] Cylinder170  label="Válec170"
  Angle = 360
  AttacherType = Attacher::AttachEngine3D
  Height = 10
  Placement = pos=(0,19,-24) rot=(0,0,1;0rad)
  Radius = 1
FEATURE [Part::Cylinder] Cylinder171  label="Válec171"
  Angle = 360
  AttacherType = Attacher::AttachEngine3D
  Height = 10
  Placement = pos=(-13.44,-13.44,-24) rot=(0,0,1;2.35619rad)
  Radius = 1
FEATURE [Part::Cylinder] Cylinder172  label="Válec172"
  Angle = 360
  AttacherType = Attacher::AttachEngine3D
  Height = 10
  Placement = pos=(6e-15,-19,-24) rot=(0,0,1;3.14159rad)
  Radius = 1
FEATURE [Part::Cylinder] Cylinder173  label="Válec173"
  Angle = 360
  AttacherType = Attacher::AttachEngine3D
  Height = 10
  Placement = pos=(13.44,-13.44,-24) rot=(0,0,1;3.92699rad)
  Radius = 1
FEATURE [Part::Cylinder] Cylinder174  label="Válec174"
  Angle = 360
  AttacherType = Attacher::AttachEngine3D
  Height = 10
  Placement = pos=(19,8e-15,-24) rot=(0,0,-1;1.5708rad)
  Radius = 1
FEATURE [Part::Cylinder] Cylinder175  label="Válec175"
  Angle = 360
  AttacherType = Attacher::AttachEngine3D
  Height = 10
  Placement = pos=(13.44,13.44,-24) rot=(0,0,-1;0.785398rad)
  Radius = 1
FEATURE [Part::Compound] Compound062
  Links = -> [Cylinder170,Cylinder168,Cylinder169,Cylinder171,Cylinder172,Cylinder173,Cylinder174,Cylinder175]
FEATURE [Part::Cylinder] Cylinder176  label="Válec176"
  Angle = 360
  AttacherType = Attacher::AttachEngine3D
  Height = 2
  Placement = pos=(-19,0,-22) rot=(0,0,1;1.5708rad)
  Radius = 2
FEATURE [Part::Cylinder] Cylinder177  label="Válec177"
  Angle = 360
  AttacherType = Attacher::AttachEngine3D
  Height = 2
  Placement = pos=(6e-15,-19,-22) rot=(0,0,1;3.14159rad)
  Radius = 2
FEATURE [Part::Cylinder] Cylinder178  label="Válec178"
  Angle = 360
  AttacherType = Attacher::AttachEngine3D
  Height = 2
  Placement = pos=(0,19,-22) rot=(0,0,1;0rad)
  Radius = 2
FEATURE [Part::Cylinder] Cylinder179  label="Válec179"
  Angle = 360
  AttacherType = Attacher::AttachEngine3D
  Height = 2
  Placement = pos=(-13.44,13.44,-22) rot=(0,0,1;0.785398rad)
  Radius = 2
FEATURE [Part::Cylinder] Cylinder180  label="Válec180"
  Angle = 360
  AttacherType = Attacher::AttachEngine3D
  Height = 2
  Placement = pos=(-13.44,-13.44,-22) rot=(0,0,1;2.35619rad)
  Radius = 2
FEATURE [Part::Cylinder] Cylinder181  label="Válec181"
  Angle = 360
  AttacherType = Attacher::AttachEngine3D
  Height = 2
  Placement = pos=(19,8e-15,-22) rot=(0,0,-1;1.5708rad)
  Radius = 2
FEATURE [Part::Cylinder] Cylinder182  label="Válec182"
  Angle = 360
  AttacherType = Attacher::AttachEngine3D
  Height = 2
  Placement = pos=(13.44,-13.44,-22) rot=(0,0,1;3.92699rad)
  Radius = 2
FEATURE [Part::Cylinder] Cylinder183  label="Válec183"
  Angle = 360
  AttacherType = Attacher::AttachEngine3D
  Height = 2
  Placement = pos=(13.44,13.44,-22) rot=(0,0,-1;0.785398rad)
  Radius = 2
FEATURE [Part::Compound] Compound063
  Links = -> [Cylinder178,Cylinder179,Cylinder176,Cylinder180,Cylinder177,Cylinder182,Cylinder181,Cylinder183]
  Placement = pos=(0,0,-3) rot=(0,0,1;0rad)
FEATURE [Part::Cut] Cut062
  Base = -> Box055
  Tool = -> Compound063
FEATURE [Part::Cylinder] Cylinder184  label="Válec184"
  Angle = 360
  AttacherType = Attacher::AttachEngine3D
  Height = 10
  Placement = pos=(-19,0,-24) rot=(0,0,1;1.5708rad)
  Radius = 1
FEATURE [Part::Cylinder] Cylinder185  label="Válec185"
  Angle = 360
  AttacherType = Attacher::AttachEngine3D
  Height = 10
  Placement = pos=(6e-15,-19,-24) rot=(0,0,1;3.14159rad)
  Radius = 1
FEATURE [Part::Cylinder] Cylinder186  label="Válec186"
  Angle = 360
  AttacherType = Attacher::AttachEngine3D
  Height = 10
  Placement = pos=(0,19,-24) rot=(0,0,1;0rad)
  Radius = 1
FEATURE [Part::Cylinder] Cylinder187  label="Válec187"
  Angle = 360
  AttacherType = Attacher::AttachEngine3D
  Height = 10
  Placement = pos=(-13.44,13.44,-24) rot=(0,0,1;0.785398rad)
  Radius = 1
FEATURE [Part::Cylinder] Cylinder188  label="Válec188"
  Angle = 360
  AttacherType = Attacher::AttachEngine3D
  Height = 10
  Placement = pos=(-13.44,-13.44,-24) rot=(0,0,1;2.35619rad)
  Radius = 1
FEATURE [Part::Cut] Cut064
  Base = -> Cut062
  Tool = -> Compound062
FEATURE [Part::Cylinder] Cylinder189  label="Válec189"
  Angle = 360
  AttacherType = Attacher::AttachEngine3D
  Height = 10
  Placement = pos=(19,8e-15,-24) rot=(0,0,-1;1.5708rad)
  Radius = 1
FEATURE [Part::Cylinder] Cylinder190  label="Válec190"
  Angle = 360
  AttacherType = Attacher::AttachEngine3D
  Height = 10
  Placement = pos=(13.44,-13.44,-24) rot=(0,0,1;3.92699rad)
  Radius = 1
FEATURE [Part::Cylinder] Cylinder191  label="Válec191"
  Angle = 360
  AttacherType = Attacher::AttachEngine3D
  Height = 10
  Placement = pos=(13.44,13.44,-24) rot=(0,0,-1;0.785398rad)
  Radius = 1
FEATURE [Part::Compound] Compound066
  Links = -> [Cylinder186,Cylinder187,Cylinder184,Cylinder188,Cylinder185,Cylinder190,Cylinder189,Cylinder191]
FEATURE [Part::Cut] Cut063
  Base = -> Tube032
  Tool = -> Compound066
FEATURE [Part::Cylinder] Cylinder192  label="Válec192"
  Angle = 360
  AttacherType = Attacher::AttachEngine3D
  Height = 50
  Placement = pos=(0,0,-29) rot=(0,0,1;0rad)
  Radius = 8
FEATURE [Part::Cut] Cut065
  Base = -> Cut064
  Tool = -> Cylinder192
FEATURE [Part::Cylinder] Cylinder193  label="Válec193"
  Angle = 360
  AttacherType = Attacher::AttachEngine3D
  Height = 3
  Placement = pos=(-19,-19,-24) rot=(0,0,1;0rad)
  Radius = 3
FEATURE [Part::Cylinder] Cylinder194  label="Válec194"
  Angle = 360
  AttacherType = Attacher::AttachEngine3D
  Height = 10
  Placement = pos=(-19.5,-19.5,-28) rot=(0,0,1;0rad)
  Radius = 1.5
FEATURE [Part::Cylinder] Cylinder195  label="Válec195"
  Angle = 360
  AttacherType = Attacher::AttachEngine3D
  Height = 10
  Placement = pos=(-19.5,19.5,-28) rot=(0,0,1;0rad)
  Radius = 1.5
FEATURE [Part::Cylinder] Cylinder196  label="Válec196"
  Angle = 360
  AttacherType = Attacher::AttachEngine3D
  Height = 10
  Placement = pos=(19.5,-19.5,-28) rot=(0,0,1;0rad)
  Radius = 1.5
FEATURE [Part::Cylinder] Cylinder197  label="Válec197"
  Angle = 360
  AttacherType = Attacher::AttachEngine3D
  Height = 10
  Placement = pos=(19.5,19.5,-28) rot=(0,0,1;0rad)
  Radius = 1.5
FEATURE [Part::Compound] Compound067
  Links = -> [Cylinder194,Cylinder195,Cylinder196,Cylinder197]
FEATURE [Part::Cut] Cut066
  Base = -> Cut065
  Tool = -> Compound067
FEATURE [Part::Cylinder] Cylinder198  label="Válec198"
  Angle = 360
  AttacherType = Attacher::AttachEngine3D
  Height = 3
  Placement = pos=(19,-19,-24) rot=(0,0,1;0rad)
  Radius = 3
FEATURE [Part::Cylinder] Cylinder199  label="Válec199"
  Angle = 360
  AttacherType = Attacher::AttachEngine3D
  Height = 3
  Placement = pos=(-19,19,-24) rot=(0,0,1;0rad)
  Radius = 3
FEATURE [Part::Cylinder] Cylinder200  label="Válec200"
  Angle = 360
  AttacherType = Attacher::AttachEngine3D
  Height = 3
  Placement = pos=(19,19,-24) rot=(0,0,1;0rad)
  Radius = 3
FEATURE [Part::Compound] Compound068
  Links = -> [Cylinder193,Cylinder198,Cylinder199,Cylinder200]
  Placement = pos=(0,0,4) rot=(0,0,1;0rad)
FEATURE [Part::Cut] Cut067
  Base = -> Cut066
  Tool = -> Compound068
FEATURE [Part::Compound] Compound069
  Links = -> [Cut067,Cut063]
FEATURE [Part::Chamfer] Chamfer
  Base = -> Compound069
  Edges = 2 edges r=2: [Edge1,Edge3]
FEATURE [Part::Chamfer] Chamfer001  label="G-mini_moto-holder-A"
  Base = -> Chamfer
  Edges = 2 edges r=2: [Edge43,Edge44]
  Placement = pos=(0,1,37) rot=(1,0,0;1.5708rad)
FEATURE [Part::Box] Box081  label="Krychle081"
  AttacherType = Attacher::AttachEngine3D
  Height = 2
  Length = 8
  Placement = pos=(-24.5,-22.5,-55) rot=(0,0,1;0rad)
  Width = 6
FEATURE [Part::Box] Box082  label="Krychle082"
  AttacherType = Attacher::AttachEngine3D
  Height = 2
  Length = 8
  Placement = pos=(16.5,-22.5,-55) rot=(0,0,1;0rad)
  Width = 6
FEATURE [Part::Box] Box083  label="Krychle083"
  AttacherType = Attacher::AttachEngine3D
  Height = 2
  Length = 8
  Placement = pos=(-24.5,16.5,-55) rot=(0,0,1;0rad)
  Width = 6
FEATURE [Part::Box] Box084  label="Krychle084"
  AttacherType = Attacher::AttachEngine3D
  Height = 2
  Length = 8
  Placement = pos=(16.5,16.5,-55) rot=(0,0,1;0rad)
  Width = 6
FEATURE [Part::Cylinder] Cylinder294  label="Válec294"
  Angle = 360
  AttacherType = Attacher::AttachEngine3D
  Height = 20
  Placement = pos=(-10.48,15.75,-50) rot=(0,0,1;0rad)
  Radius = 1.5
FEATURE [Part::Cylinder] Cylinder295  label="Válec295"
  Angle = 360
  AttacherType = Attacher::AttachEngine3D
  Height = 20
  Placement = pos=(10.48,15.75,-50) rot=(0,0,1;0rad)
  Radius = 1.5
FEATURE [Part::Compound] Compound088
  Links = -> [Box084,Box083,Box082,Box081]
  Placement = pos=(0,0,-2) rot=(0,0,1;0rad)
FEATURE [Part::Box] Box085  label="Krychle085"
  AttacherType = Attacher::AttachEngine3D
  Height = 11
  Length = 34
  Placement = pos=(-17,-17,-73) rot=(0,0,1;0rad)
  Width = 34
FEATURE [Part::Box] Box086  label="Krychle086"
  AttacherType = Attacher::AttachEngine3D
  Height = 11
  Length = 46.3
  Placement = pos=(-23.15,-23.15,-73) rot=(0,0,1;0rad)
  Width = 46.3
FEATURE [Part::Cut] Cut087
  Base = -> Box086
  Placement = pos=(0,0,7) rot=(0,0,1;0rad)
  Tool = -> Box085
FEATURE [Part::Cylinder] Cylinder296  label="Válec296"
  Angle = 360
  AttacherType = Attacher::AttachEngine3D
  Height = 3
  Placement = pos=(15.5,-15.5,-54) rot=(0,0,1;0rad)
  Radius = 3
FEATURE [Part::Cylinder] Cylinder297  label="Válec297"
  Angle = 360
  AttacherType = Attacher::AttachEngine3D
  Height = 20
  Placement = pos=(15.5,-15.5,-68) rot=(0,0,1;0rad)
  Radius = 1.5
FEATURE [Part::Box] Box087  label="Krychle087"
  AttacherType = Attacher::AttachEngine3D
  Height = 8
  Length = 42.3
  Placement = pos=(-21.15,-21.15,-70) rot=(0,0,1;0rad)
  Width = 42.3
FEATURE [Part::Cylinder] Cylinder298  label="Válec298"
  Angle = 360
  AttacherType = Attacher::AttachEngine3D
  Height = 3
  Placement = pos=(15.5,15.5,-54) rot=(0,0,1;0rad)
  Radius = 3
FEATURE [Part::Cylinder] Cylinder299  label="Válec299"
  Angle = 360
  AttacherType = Attacher::AttachEngine3D
  Height = 20
  Placement = pos=(15.5,-15.5,-68) rot=(0,0,1;0rad)
  Radius = 1.5
FEATURE [Part::Cylinder] Cylinder300  label="Válec300"
  Angle = 360
  AttacherType = Attacher::AttachEngine3D
  Height = 3
  Placement = pos=(-15.5,15.5,-54) rot=(0,0,1;0rad)
  Radius = 3
FEATURE [Part::Box] Box088  label="Krychle088"
  AttacherType = Attacher::AttachEngine3D
  Height = 2
  Length = 8
  Placement = pos=(-24.5,-22.5,-55) rot=(0,0,1;0rad)
  Width = 6
FEATURE [Part::Box] Box089  label="Krychle089"
  AttacherType = Attacher::AttachEngine3D
  Height = 4
  Length = 46.3
  Placement = pos=(-23.15,-23.15,-25) rot=(0,0,1;0rad)
  Width = 46.3
FEATURE [Part::Cylinder] Cylinder301  label="Válec301"
  Angle = 360
  AttacherType = Attacher::AttachEngine3D
  Height = 20
  Placement = pos=(15.5,15.5,-68) rot=(0,0,1;0rad)
  Radius = 1.5
FEATURE [Part::Cylinder] Cylinder302  label="Válec302"
  Angle = 360
  AttacherType = Attacher::AttachEngine3D
  Height = 20
  Placement = pos=(-15.5,-15.5,-68) rot=(0,0,1;0rad)
  Radius = 1.5
FEATURE [Part::Box] Box090  label="Krychle090"
  AttacherType = Attacher::AttachEngine3D
  Height = 2
  Length = 8
  Placement = pos=(16.5,-22.5,-55) rot=(0,0,1;0rad)
  Width = 6
FEATURE [Part::Box] Box091  label="Krychle091"
  AttacherType = Attacher::AttachEngine3D
  Height = 2
  Length = 8
  Placement = pos=(-24.5,16.5,-55) rot=(0,0,1;0rad)
  Width = 6
FEATURE [Part::Box] Box092  label="Krychle092"
  AttacherType = Attacher::AttachEngine3D
  Height = 8
  Length = 46.3
  Placement = pos=(-23.15,-23.15,-70) rot=(0,0,1;0rad)
  Width = 46.3
FEATURE [Part::Cylinder] Cylinder303  label="Válec303"
  Angle = 360
  AttacherType = Attacher::AttachEngine3D
  Height = 20
  Placement = pos=(-15.5,15.5,-68) rot=(0,0,1;0rad)
  Radius = 1.5
FEATURE [Part::Compound] Compound090
  Links = -> [Cylinder301,Cylinder303,Cylinder299,Cylinder302]
FEATURE [Part::Box] Box093  label="Krychle093"
  AttacherType = Attacher::AttachEngine3D
  Height = 20
  Length = 29
  Placement = pos=(-14.5,0,-75) rot=(0,0,1;0rad)
  Width = 45.5
FEATURE [Part::Cylinder] Cylinder304  label="Válec304"
  Angle = 360
  AttacherType = Attacher::AttachEngine3D
  Height = 3
  Placement = pos=(-15.5,-15.5,-54) rot=(0,0,1;0rad)
  Radius = 3
FEATURE [Part::Cylinder] Cylinder305  label="Válec305"
  Angle = 360
  AttacherType = Attacher::AttachEngine3D
  Height = 10
  Placement = pos=(19.5,-19.5,-28) rot=(0,0,1;0rad)
  Radius = 1.5
FEATURE [Part::Cylinder] Cylinder306  label="Válec306"
  Angle = 360
  AttacherType = Attacher::AttachEngine3D
  Height = 20
  Placement = pos=(15.5,15.5,-68) rot=(0,0,1;0rad)
  Radius = 1.5
FEATURE [Part::Cylinder] Cylinder307  label="Válec307"
  Angle = 360
  AttacherType = Attacher::AttachEngine3D
  Height = 10
  Placement = pos=(-19.5,19.5,-28) rot=(0,0,1;0rad)
  Radius = 1.5
FEATURE [Part::Box] Box094  label="Krychle094"
  AttacherType = Attacher::AttachEngine3D
  Height = 2
  Length = 8
  Placement = pos=(16.5,16.5,-55) rot=(0,0,1;0rad)
  Width = 6
FEATURE [Part::Cylinder] Cylinder308  label="Válec308"
  Angle = 360
  AttacherType = Attacher::AttachEngine3D
  Height = 20
  Placement = pos=(-15.5,-15.5,-68) rot=(0,0,1;0rad)
  Radius = 1.5
FEATURE [Part::Box] Box095  label="Krychle095"
  AttacherType = Attacher::AttachEngine3D
  Height = 20
  Length = 29
  Placement = pos=(-14.5,0,-75) rot=(0,0,1;0rad)
  Width = 45.5
FEATURE [Part::Cylinder] Cylinder309  label="Válec309"
  Angle = 360
  AttacherType = Attacher::AttachEngine3D
  Height = 20
  Placement = pos=(-15.5,15.5,-68) rot=(0,0,1;0rad)
  Radius = 1.5
FEATURE [Part::Cylinder] Cylinder310  label="Válec310"
  Angle = 360
  AttacherType = Attacher::AttachEngine3D
  Height = 50
  Placement = pos=(0,0,-29) rot=(0,0,1;0rad)
  Radius = 8
FEATURE [Part::Cylinder] Cylinder311  label="Válec311"
  Angle = 360
  AttacherType = Attacher::AttachEngine3D
  Height = 10
  Placement = pos=(19.5,19.5,-28) rot=(0,0,1;0rad)
  Radius = 1.5
FEATURE [Part::Cylinder] Cylinder312  label="Válec312"
  Angle = 360
  AttacherType = Attacher::AttachEngine3D
  Height = 10
  Placement = pos=(-19.5,-19.5,-28) rot=(0,0,1;0rad)
  Radius = 1.5
FEATURE [Part::Compound] Compound091
  Links = -> [Cylinder312,Cylinder307,Cylinder305,Cylinder311]
FEATURE [Part::Cylinder] Cylinder313  label="Válec313"
  Angle = 360
  AttacherType = Attacher::AttachEngine3D
  Height = 20
  Placement = pos=(19.5,19.5,-28) rot=(0,0,1;0rad)
  Radius = 1.5
FEATURE [Part::Cylinder] Cylinder314  label="Válec314"
  Angle = 360
  AttacherType = Attacher::AttachEngine3D
  Height = 20
  Placement = pos=(-19.5,-19.5,-28) rot=(0,0,1;0rad)
  Radius = 1.5
FEATURE [Part::Cylinder] Cylinder315  label="Válec315"
  Angle = 360
  AttacherType = Attacher::AttachEngine3D
  Height = 20
  Placement = pos=(-19.5,19.5,-28) rot=(0,0,1;0rad)
  Radius = 1.5
FEATURE [Part::Cylinder] Cylinder316  label="Válec316"
  Angle = 360
  AttacherType = Attacher::AttachEngine3D
  Height = 20
  Placement = pos=(19.5,-19.5,-28) rot=(0,0,1;0rad)
  Radius = 1.5
FEATURE [Part::Box] Box096  label="Krychle096"
  AttacherType = Attacher::AttachEngine3D
  Height = 8
  Length = 7
  Placement = pos=(-22,15,-74) rot=(0,0,1;0rad)
  Width = 7
FEATURE [Part::Cut] Cut090
  Base = -> Box089
  Tool = -> Cylinder310
FEATURE [Part::Cut] Cut089
  Base = -> Cut090
  Tool = -> Compound091
FEATURE [Part::Cut] Cut093
  Base = -> Box092
  Placement = pos=(0,0,-4) rot=(0,0,1;0rad)
  Tool = -> Box087
FEATURE [Part::Cut] Cut088
  Base = -> Cut093
  Tool = -> Box095
FEATURE [Part::Compound] Compound092
  Links = -> [Box094,Box091,Box090,Box088]
  Placement = pos=(0,0,10) rot=(0,0,1;0rad)
FEATURE [Part::Compound] Compound093
  Links = -> [Cut089]
  Placement = pos=(0,0,-30) rot=(0,0,1;0rad)
FEATURE [Part::Cut] Cut092
  Base = -> Compound093
  Tool = -> Compound092
FEATURE [Part::Compound] Compound094
  Links = -> [Cylinder294,Cylinder295]
  Placement = pos=(0,0,-10) rot=(0,0,1;0rad)
FEATURE [Part::Compound] Compound095
  Links = -> [Cylinder306,Cylinder309,Cylinder297,Cylinder308]
FEATURE [Part::Compound] Compound097
  Links = -> [Cylinder304,Cylinder296,Cylinder300,Cylinder298]
FEATURE [Part::Cut] Cut094
  Base = -> Cut087
  Tool = -> Compound090
FEATURE [Part::Cut] Cut095
  Base = -> Cut094
  Tool = -> Box093
FEATURE [Part::Cut] Cut096
  Base = -> Cut092
  Tool = -> Compound094
FEATURE [Part::Cut] Cut091
  Base = -> Cut096
  Tool = -> Compound095
FEATURE [Part::Cut] Cut097
  Base = -> Cut091
  Tool = -> Compound097
FEATURE [Part::Cut] Cut098
  Base = -> Cut095
  Tool = -> Compound088
FEATURE [Part::Compound] Compound098
  Links = -> [Cylinder314,Cylinder315,Cylinder316,Cylinder313]
  Placement = pos=(0,0,-33) rot=(0,0,1;0rad)
FEATURE [Part::Cut] Cut099
  Base = -> Cut098
  Tool = -> Compound098
FEATURE [Part::Cylinder] Cylinder317  label="Válec317"
  Angle = 360
  AttacherType = Attacher::AttachEngine3D
  Height = 8
  Placement = pos=(-15.15,15.15,-74) rot=(0,0,1;0rad)
  Radius = 6
FEATURE [Part::Cut] Cut100
  Base = -> Box096
  Tool = -> Cylinder317
FEATURE [Part::Cut] Cut101
  Base = -> Box096
  Placement = pos=(0,0,0) rot=(0,0,1;1.5708rad)
  Tool = -> Cylinder317
FEATURE [Part::Cut] Cut102
  Base = -> Box096
  Placement = pos=(0,0,0) rot=(0,0,1;3.14159rad)
  Tool = -> Cylinder317
FEATURE [Part::Cut] Cut103
  Base = -> Box096
  Placement = pos=(0,0,0) rot=(0,0,-1;1.5708rad)
  Tool = -> Cylinder317
FEATURE [Part::Compound] Compound100
  Links = -> [Cut100,Cut101,Cut102,Cut103]
FEATURE [Part::Compound] Compound101
  Links = -> [Cut088,Cut097,Cut099,Compound100]
FEATURE [Part::Chamfer] Chamfer006
  Base = -> Compound101
  Edges = 9 edges r=2: [Edge1,Edge6,Edge29,Edge37,Edge42,Edge58,Edge105,Edge162,Edge181]
FEATURE [Part::Chamfer] Chamfer007
  Base = -> Chamfer006
  Edges = 3 edges r=2: [Edge4,Edge49,Edge115]
FEATURE [Part::Chamfer] Chamfer008  label="G-mini_moto-holder-B"
  Base = -> Chamfer007
  Edges = 5 edges r=0.9: [Edge3,Edge24,Edge25,Edge27,Edge29]
  Placement = pos=(0,-25,37) rot=(1,0,0;1.5708rad)
FEATURE [Part::Box] Box  label="Krychle"
  AttacherType = Attacher::AttachEngine3D
  Height = 8
  Length = 6
  Placement = pos=(16,-8,10) rot=(0,0,1;0rad)
  Width = 44
FEATURE [Part::Box] Box876  label="Krychle875"
  AttacherType = Attacher::AttachEngine3D
  Height = 6
  Length = 6
  Placement = pos=(10,-8,11) rot=(0,0,1;0rad)
  Width = 20
FEATURE [Part::Box] Box877  label="Krychle876"
  AttacherType = Attacher::AttachEngine3D
  Height = 8
  Length = 6
  Placement = pos=(-22,-8,10) rot=(0,0,1;0rad)
  Width = 44
FEATURE [Part::Box] Box878  label="Krychle877"
  AttacherType = Attacher::AttachEngine3D
  Height = 10
  Length = 64
  Placement = pos=(-32,24,5) rot=(0,0,1;0rad)
  Width = 64
FEATURE [Part::Compound] Compound
  Links = -> [Box,Box877]
FEATURE [Part::Cylinder] Cylinder  label="Válec"
  Angle = 360
  AttacherType = Attacher::AttachEngine3D
  Height = 20
  Radius = 38
FEATURE [Part::Common] Common
  Base = -> Compound
  Tool = -> Cylinder
FEATURE [Part::FeaturePython] Tube  # WARN: FeaturePython — macro-defined, semantics opaque (R4)
  AttacherType = Attacher::AttachEngine3D
  Height = 24
  InnerRadius = 26
  OuterRadius = 31
  Placement = pos=(1,-16,37) rot=(1,0,0;1.5708rad)
FEATURE [Part::Cylinder] Cylinder2620  label="Válec2590"
  Angle = 360
  AttacherType = Attacher::AttachEngine3D
  Height = 10
  Placement = pos=(17,-98,44) rot=(1,0,0;1.5708rad)
  Radius = 2
FEATURE [Part::FeaturePython] Tube115  # WARN: FeaturePython — macro-defined, semantics opaque (R4)
  AttacherType = Attacher::AttachEngine3D
  Height = 11.5
  InnerRadius = 34.5
  OuterRadius = 39
  Placement = pos=(17,-92,10) rot=(1,0,0;1.5708rad)
FEATURE [Part::FeaturePython] Tube116  # WARN: FeaturePython — macro-defined, semantics opaque (R4)
  AttacherType = Attacher::AttachEngine3D
  Height = 0.5
  InnerRadius = 34.5
  OuterRadius = 39
  Placement = pos=(17,-93.5,10) rot=(1,0,0;1.5708rad)
FEATURE [Part::FeaturePython] Tube117  # WARN: FeaturePython — macro-defined, semantics opaque (R4)
  AttacherType = Attacher::AttachEngine3D
  Height = 1.5
  InnerRadius = 31
  OuterRadius = 39
  Placement = pos=(17,-92,10) rot=(1,0,0;1.5708rad)
FEATURE [Part::Compound] Compound1161
  Links = -> [Tube117,Tube116]
FEATURE [Part::Torus] Torus004  label="Anuloid004"
  Angle1 = -180
  Angle2 = 180
  Angle3 = 360
  AttacherType = Attacher::AttachEngine3D
  Placement = pos=(17,-98,10) rot=(1,0,0;1.5708rad)
  Radius1 = 34
  Radius2 = 2
FEATURE [Part::Cut] Cut969
  Base = -> Tube115
  Tool = -> Torus004
FEATURE [Part::Cut] Cut970
  Base = -> Cut969
  Placement = pos=(0,-2,0) rot=(0,0,1;0rad)
  Tool = -> Cylinder2620
FEATURE [Part::Compound] Compound1162  label="Wrist_outer-halo-ring"
  Links = -> [Cut970,Compound1161]
  Placement = pos=(-16,-170,47) rot=(1,0,0;3.14159rad)
FEATURE [Part::Box] Box879  label="Krychle878"
  AttacherType = Attacher::AttachEngine3D
  Height = 6
  Length = 8
  Placement = pos=(-38,-68,5) rot=(0,0,1;0rad)
  Width = 69
FEATURE [Part::Box] Box880  label="Krychle879"
  AttacherType = Attacher::AttachEngine3D
  Height = 6
  Length = 12
  Placement = pos=(-30,-68,5) rot=(0,0,1;0rad)
  Width = 13.5
FEATURE [Part::Box] Box881  label="Krychle880"
  AttacherType = Attacher::AttachEngine3D
  Height = 6
  Length = 8
  Placement = pos=(30,-68,5) rot=(0,0,1;0rad)
  Width = 69
FEATURE [Part::Box] Box882  label="Krychle881"
  AttacherType = Attacher::AttachEngine3D
  Height = 6
  Length = 12
  Placement = pos=(18,-68,5) rot=(0,0,1;0rad)
  Width = 13.5
FEATURE [Part::Compound] Compound1163
  Links = -> [Box882,Box880]
FEATURE [Part::FeaturePython] Tube118  # WARN: FeaturePython — macro-defined, semantics opaque (R4)
  AttacherType = Attacher::AttachEngine3D
  Height = 24
  InnerRadius = 26
  OuterRadius = 39
  Placement = pos=(1,-45,37) rot=(1,0,0;1.5708rad)
FEATURE [Part::Cut] Cut
  Base = -> Compound1163
  Tool = -> Tube118
FEATURE [Part::Box] Box883  label="Krychle882"
  AttacherType = Attacher::AttachEngine3D
  Height = 32
  Length = 15
  Placement = pos=(-38,-68,5) rot=(0,0,1;0rad)
  Width = 13.5
FEATURE [Part::Box] Box884  label="Krychle883"
  AttacherType = Attacher::AttachEngine3D
  Height = 32
  Length = 15
  Placement = pos=(23,-68,5) rot=(0,0,1;0rad)
  Width = 13.5
FEATURE [Part::Compound] Compound1164
  Links = -> [Box883,Box884]
FEATURE [Part::FeaturePython] Tube119  # WARN: FeaturePython — macro-defined, semantics opaque (R4)
  AttacherType = Attacher::AttachEngine3D
  Height = 24
  InnerRadius = 20
  OuterRadius = 39
  Placement = pos=(1,-45,37) rot=(1,0,0;1.5708rad)
FEATURE [Part::Cut] Cut971
  Base = -> Compound1164
  Tool = -> Tube119
FEATURE [Part::Chamfer] Chamfer118
  Base = -> Box879
  Edges = 1 edges r=1: [Edge2]
FEATURE [Part::Chamfer] Chamfer119
  Base = -> Box881
  Edges = 1 edges r=1: [Edge6]
FEATURE [Part::Cylinder] Cylinder2621  label="Válec2591"
  Angle = 360
  AttacherType = Attacher::AttachEngine3D
  Height = 60
  Placement = pos=(-34,-10,8) rot=(1,0,0;1.5708rad)
  Radius = 1.5
FEATURE [Part::Cylinder] Cylinder2622  label="Válec2592"
  Angle = 360
  AttacherType = Attacher::AttachEngine3D
  Height = 8
  Placement = pos=(-34,-61,8) rot=(1,0,0;1.5708rad)
  Radius = 3
FEATURE [Part::Cylinder] Cylinder2623  label="Válec2593"
  Angle = 360
  AttacherType = Attacher::AttachEngine3D
  Height = 60
  Placement = pos=(34,-10,8) rot=(1,0,0;1.5708rad)
  Radius = 1.5
FEATURE [Part::Cylinder] Cylinder2624  label="Válec2594"
  Angle = 360
  AttacherType = Attacher::AttachEngine3D
  Height = 8
  Placement = pos=(34,-61,8) rot=(1,0,0;1.5708rad)
  Radius = 3
FEATURE [Part::Box] Box885  label="Krychle884"
  AttacherType = Attacher::AttachEngine3D
  Height = 6
  Length = 20
  Placement = pos=(-38,-40,5) rot=(0,0,1;0rad)
  Width = 20
FEATURE [Part::Cylinder] Cylinder2625  label="Válec2595"
  Angle = 360
  AttacherType = Attacher::AttachEngine3D
  Height = 16
  Placement = pos=(-22,-40,0) rot=(0,0,1;0rad)
  Radius = 8
FEATURE [Part::Cylinder] Cylinder2626  label="Válec2596"
  Angle = 360
  AttacherType = Attacher::AttachEngine3D
  Height = 16
  Placement = pos=(22,-40,0) rot=(0,0,1;0rad)
  Radius = 8
FEATURE [Part::Box] Box886  label="Krychle885"
  AttacherType = Attacher::AttachEngine3D
  Height = 6
  Length = 20
  Placement = pos=(18,-40,5) rot=(0,0,1;0rad)
  Width = 20
FEATURE [Part::Compound] Compound1165
  Links = -> [Box886,Box885]
FEATURE [Part::Compound] Compound1166
  Links = -> [Cylinder2626,Cylinder2625]
FEATURE [Part::Cut] Cut972
  Base = -> Compound1165
  Tool = -> Compound1166
FEATURE [Part::Chamfer] Chamfer120
  Base = -> Cut972
  Edges = 1 edges r=1: [Edge8]
FEATURE [Part::Chamfer] Chamfer121
  Base = -> Chamfer119
  Edges = 1 edges r=1: [Edge15]
FEATURE [Part::Chamfer] Chamfer122
  Base = -> Chamfer120
  Edges = 1 edges r=1: [Edge8]
FEATURE [Part::Chamfer] Chamfer123
  Base = -> Chamfer122
  Edges = 1 edges r=1: [Edge23]
FEATURE [Part::Chamfer] Chamfer124
  Base = -> Chamfer123
  Edges = 1 edges r=1: [Edge16]
FEATURE [Part::Chamfer] Chamfer125
  Base = -> Chamfer118
  Edges = 1 edges r=1: [Edge15]
FEATURE [Part::Cylinder] Cylinder2627  label="Válec2597"
  Angle = 360
  AttacherType = Attacher::AttachEngine3D
  Height = 16
  Radius = 38
FEATURE [Part::Cylinder] Cylinder2628  label="Válec2598"
  Angle = 360
  AttacherType = Attacher::AttachEngine3D
  Height = 16
  Radius = 38
FEATURE [Part::Cut] Cut973
  Base = -> Chamfer125
  Tool = -> Cylinder2627
FEATURE [Part::Cylinder] Cylinder2629  label="Válec2599"
  Angle = 360
  AttacherType = Attacher::AttachEngine3D
  Height = 16
  Radius = 38
FEATURE [Part::Cut] Cut974
  Base = -> Chamfer124
  Tool = -> Cylinder2628
FEATURE [Part::Cut] Cut975
  Base = -> Chamfer121
  Tool = -> Cylinder2629
FEATURE [Part::Compound] Compound1167
  Links = -> [Cut973,Cut974,Cut975]
FEATURE [Part::Compound] Compound1168
  Links = -> [Cut971,Cut]
FEATURE [Part::Box] Box887  label="Krychle886"
  AttacherType = Attacher::AttachEngine3D
  Height = 7
  Length = 6
  Placement = pos=(16,-8,10) rot=(0,0,1;0rad)
  Width = 44
FEATURE [Part::Box] Box888  label="Krychle887"
  AttacherType = Attacher::AttachEngine3D
  Height = 7
  Length = 6
  Placement = pos=(-21,-8,10) rot=(0,0,1;0rad)
  Width = 44
FEATURE [Part::Compound] Compound1171
  Links = -> [Box887,Box888]
FEATURE [Part::Cylinder] Cylinder2630  label="Válec2600"
  Angle = 360
  AttacherType = Attacher::AttachEngine3D
  Height = 3
  Placement = pos=(-19.4454,-19.4454,19) rot=(0,0,1;2.35619rad)
  Radius = 3
FEATURE [Part::Cylinder] Cylinder2631  label="Válec2601"
  Angle = 360
  AttacherType = Attacher::AttachEngine3D
  Height = 3
  Placement = pos=(1.1e-14,-27.5,19.5) rot=(0,0,1;3.14159rad)
  Radius = 3
FEATURE [Part::Cylinder] Cylinder2632  label="Válec2602"
  Angle = 360
  AttacherType = Attacher::AttachEngine3D
  Height = 20
  Placement = pos=(-19.4454,19.4454,19) rot=(0,0,1;0.785398rad)
  Radius = 1.5
FEATURE [Part::Cylinder] Cylinder2633  label="Válec2603"
  Angle = 360
  AttacherType = Attacher::AttachEngine3D
  Height = 20
  Placement = pos=(-19.4454,-19.4454,19) rot=(0,0,1;2.35619rad)
  Radius = 1.5
FEATURE [Part::Cylinder] Cylinder2634  label="Válec2604"
  Angle = 360
  AttacherType = Attacher::AttachEngine3D
  Height = 20
  Placement = pos=(19.4454,-19.4454,19) rot=(0,0,1;3.92699rad)
  Radius = 1.5
FEATURE [Part::Cylinder] Cylinder2635  label="Válec2605"
  Angle = 360
  AttacherType = Attacher::AttachEngine3D
  Height = 3
  Placement = pos=(-19.4454,19.4454,19) rot=(0,0,1;0.785398rad)
  Radius = 3
FEATURE [Part::Cylinder] Cylinder2636  label="Válec2606"
  Angle = 360
  AttacherType = Attacher::AttachEngine3D
  Height = 3
  Placement = pos=(-27.5,-4e-15,19) rot=(0,0,1;1.5708rad)
  Radius = 3
FEATURE [Part::Cylinder] Cylinder2637  label="Válec2607"
  Angle = 360
  AttacherType = Attacher::AttachEngine3D
  Height = 3
  Placement = pos=(19.4454,-19.4454,19) rot=(0,0,1;3.92699rad)
  Radius = 3
FEATURE [Part::Cylinder] Cylinder2638  label="Válec2608"
  Angle = 360
  AttacherType = Attacher::AttachEngine3D
  Height = 3
  Placement = pos=(27.5,1.2e-14,19) rot=(0,0,-1;1.5708rad)
  Radius = 3
FEATURE [Part::Cylinder] Cylinder2639  label="Válec2609"
  Angle = 360
  AttacherType = Attacher::AttachEngine3D
  Height = 3
  Placement = pos=(19.4454,19.4454,19) rot=(0,0,-1;0.785398rad)
  Radius = 3
FEATURE [Part::Cylinder] Cylinder2640  label="Válec2610"
  Angle = 360
  AttacherType = Attacher::AttachEngine3D
  Height = 20
  Placement = pos=(-27.5,-4e-15,19) rot=(0,0,1;1.5708rad)
  Radius = 1.5
FEATURE [Part::Cylinder] Cylinder2641  label="Válec2611"
  Angle = 360
  AttacherType = Attacher::AttachEngine3D
  Height = 20
  Placement = pos=(1.1e-14,-27.5,19) rot=(0,0,1;3.14159rad)
  Radius = 1.5
FEATURE [Part::Cylinder] Cylinder2642  label="Válec2612"
  Angle = 360
  AttacherType = Attacher::AttachEngine3D
  Height = 3
  Placement = pos=(0,27.5,19) rot=(0,0,1;0rad)
  Radius = 3
FEATURE [Part::Compound] Compound1170
  Links = -> [Cylinder2642,Cylinder2635,Cylinder2636,Cylinder2630,Cylinder2631,Cylinder2637,Cylinder2638,Cylinder2639]
  Placement = pos=(0,0,-19) rot=(0,0,1;0rad)
FEATURE [Part::Cylinder] Cylinder2643  label="Válec2613"
  Angle = 360
  AttacherType = Attacher::AttachEngine3D
  Height = 20
  Placement = pos=(19.4454,19.4454,19) rot=(0,0,-1;0.785398rad)
  Radius = 1.5
FEATURE [Part::Cylinder] Cylinder2644  label="Válec2614"
  Angle = 360
  AttacherType = Attacher::AttachEngine3D
  Height = 20
  Placement = pos=(27.5,1.2e-14,19) rot=(0,0,-1;1.5708rad)
  Radius = 1.5
FEATURE [Part::Cylinder] Cylinder2645  label="Válec2615"
  Angle = 360
  AttacherType = Attacher::AttachEngine3D
  Height = 6
  Radius = 38
FEATURE [Part::Cylinder] Cylinder2646  label="Válec2616"
  Angle = 360
  AttacherType = Attacher::AttachEngine3D
  Height = 20
  Placement = pos=(0,27.5,19) rot=(0,0,1;0rad)
  Radius = 1.5
FEATURE [Part::Compound] Compound1169
  Links = -> [Cylinder2646,Cylinder2632,Cylinder2640,Cylinder2633,Cylinder2641,Cylinder2634,Cylinder2644,Cylinder2643]
  Placement = pos=(0,0,-23) rot=(0,0,1;0rad)
FEATURE [Part::Cylinder] Cylinder2647  label="Válec2617"
  Angle = 360
  AttacherType = Attacher::AttachEngine3D
  Height = 5
  Placement = pos=(0,0,1) rot=(0,0,1;0rad)
  Radius = 14
FEATURE [Part::Cylinder] Cylinder2648  label="Válec2618"
  Angle = 360
  AttacherType = Attacher::AttachEngine3D
  Height = 20
  Radius = 38
FEATURE [Part::Common] Common006
  Base = -> Compound1171
  Tool = -> Cylinder2648
FEATURE [Part::Cut] Cut630
  Base = -> Cylinder2645
  Tool = -> Compound1170
FEATURE [Part::Cut] Cut628
  Base = -> Cut630
  Tool = -> Compound1169
FEATURE [Part::Cut] Cut629
  Base = -> Cut628
  Tool = -> Cylinder2647
FEATURE [Part::Chamfer] Chamfer126
  Base = -> Cut629
  Edges = 1 edges r=1: [Edge3]
  Placement = pos=(1e-15,0,11) rot=(-0.19509,0.980785,0;3.14159rad)
FEATURE [Part::FeaturePython] Tube120  # WARN: FeaturePython — macro-defined, semantics opaque (R4)
  AttacherType = Attacher::AttachEngine3D
  Height = 24
  InnerRadius = 22
  OuterRadius = 31
  Placement = pos=(1,-16,37) rot=(1,0,0;1.5708rad)
FEATURE [Part::Cut] Cut976
  Base = -> Chamfer126
  Tool = -> Tube120
FEATURE [Part::Cylinder] Cylinder2649  label="Válec2619"
  Angle = 360
  AttacherType = Attacher::AttachEngine3D
  Height = 57
  Placement = pos=(0,-32,30) rot=(1,0,0;1.5708rad)
  Radius = 4
FEATURE [Part::Box] Box889  label="Krychle888"
  AttacherType = Attacher::AttachEngine3D
  Height = 18
  Length = 31
  Placement = pos=(-15,-8,10) rot=(0,0,1;0rad)
  Width = 44
FEATURE [Part::Box] Box890  label="Krychle889"
  AttacherType = Attacher::AttachEngine3D
  Height = 6
  Length = 2
  Placement = pos=(-18,-4,11) rot=(0,0,1;0rad)
  Width = 6
FEATURE [Part::FeaturePython] Tube121  # WARN: FeaturePython — macro-defined, semantics opaque (R4)
  AttacherType = Attacher::AttachEngine3D
  Height = 25
  InnerRadius = 2
  OuterRadius = 21
  Placement = pos=(1,43,37) rot=(1,0,0;1.5708rad)
FEATURE [Part::FeaturePython] Tube122  # WARN: FeaturePython — macro-defined, semantics opaque (R4)
  AttacherType = Attacher::AttachEngine3D
  Height = 26
  InnerRadius = 2
  OuterRadius = 25
  Placement = pos=(1,18,37) rot=(1,0,0;1.5708rad)
FEATURE [Part::Box] Box891  label="Krychle890"
  AttacherType = Attacher::AttachEngine3D
  Height = 18
  Length = 31
  Placement = pos=(-15,-8,10) rot=(0,0,1;0rad)
  Width = 44
FEATURE [Part::Box] Box892  label="Krychle891"
  AttacherType = Attacher::AttachEngine3D
  Height = 6
  Length = 2
  Placement = pos=(-12,-4,10) rot=(0,0,1;0rad)
  Width = 6
FEATURE [Part::FeaturePython] Tube123  # WARN: FeaturePython — macro-defined, semantics opaque (R4)
  AttacherType = Attacher::AttachEngine3D
  Height = 25
  InnerRadius = 2
  OuterRadius = 21
  Placement = pos=(1,43,37) rot=(1,0,0;1.5708rad)
FEATURE [Part::FeaturePython] Tube124  # WARN: FeaturePython — macro-defined, semantics opaque (R4)
  AttacherType = Attacher::AttachEngine3D
  Height = 26
  InnerRadius = 2
  OuterRadius = 25
  Placement = pos=(1,18,37) rot=(1,0,0;1.5708rad)
FEATURE [Part::Cut] Cut977
  Base = -> Box891
  Tool = -> Tube124
FEATURE [Part::Cut] Cut001
  Base = -> Cut977
  Tool = -> Tube123
FEATURE [Part::Cut] Cut002  label="G-mini_underfix"
  Base = -> Cut001
  Tool = -> Box892
FEATURE [Part::Box] Box709  label="Krychle709"
  AttacherType = Attacher::AttachEngine3D
  Height = 9
  Length = 54
  Placement = pos=(-27.0044,59.998,75) rot=(0,0,1;0rad)
  Width = 68
FEATURE [Part::Box] Box710  label="Krychle710"
  AttacherType = Attacher::AttachEngine3D
  Height = 50
  Length = 42
  Placement = pos=(-21,58,38) rot=(0,0,1;0rad)
  Width = 64
FEATURE [Part::Cylinder] Cylinder1784  label="Válec1784"
  Angle = 360
  AttacherType = Attacher::AttachEngine3D
  Height = 60
  Placement = pos=(24,73,-80) rot=(0,0,1;0rad)
  Radius = 1.5
FEATURE [Part::Cylinder] Cylinder1785  label="Válec1785"
  Angle = 360
  AttacherType = Attacher::AttachEngine3D
  Height = 60
  Placement = pos=(-24,73,-80) rot=(0,0,1;0rad)
  Radius = 1.5
FEATURE [Part::Cylinder] Cylinder1786  label="Válec1786"
  Angle = 360
  AttacherType = Attacher::AttachEngine3D
  Height = 60
  Placement = pos=(-15,125,-80) rot=(0,0,1;0rad)
  Radius = 1.5
FEATURE [Part::Cylinder] Cylinder1787  label="Válec1787"
  Angle = 360
  AttacherType = Attacher::AttachEngine3D
  Height = 60
  Placement = pos=(15,125,-80) rot=(0,0,1;0rad)
  Radius = 1.5
FEATURE [Part::Cylinder] Cylinder1788  label="Válec1788"
  Angle = 360
  AttacherType = Attacher::AttachEngine3D
  Height = 3
  Placement = pos=(24,73,-80) rot=(0,0,1;0rad)
  Radius = 3
FEATURE [Part::Cylinder] Cylinder1789  label="Válec1789"
  Angle = 360
  AttacherType = Attacher::AttachEngine3D
  Height = 3
  Placement = pos=(-24,73,-80) rot=(0,0,1;0rad)
  Radius = 3
FEATURE [Part::Cylinder] Cylinder1790  label="Válec1790"
  Angle = 360
  AttacherType = Attacher::AttachEngine3D
  Height = 3
  Placement = pos=(-15,125,-80) rot=(0,0,1;0rad)
  Radius = 3
FEATURE [Part::Cylinder] Cylinder1791  label="Válec1791"
  Angle = 360
  AttacherType = Attacher::AttachEngine3D
  Height = 3
  Placement = pos=(15,125,-80) rot=(0,0,1;0rad)
  Radius = 3
FEATURE [Part::Compound] Compound887
  Links = -> [Cylinder1784,Cylinder1785,Cylinder1786,Cylinder1787]
  Placement = pos=(0,0,120) rot=(0,0,1;0rad)
FEATURE [Part::Compound] Compound888
  Links = -> [Cylinder1788,Cylinder1789,Cylinder1790,Cylinder1791]
  Placement = pos=(0,0,161) rot=(0,0,1;0rad)
FEATURE [Part::Cut] Cut519
  Base = -> Box709
  Tool = -> Box710
FEATURE [Part::Chamfer] Chamfer059
  Base = -> Cut519
  Edges = 2 edges r=3: [Edge3,Edge15]
FEATURE [Part::Chamfer] Chamfer060
  Base = -> Chamfer059
  Edges = 2 edges r=2: [Edge1,Edge12]
FEATURE [Part::Chamfer] Chamfer061
  Base = -> Chamfer060
  Edges = 1 edges r=1: [Edge27]
FEATURE [Part::Cut] Cut520
  Base = -> Chamfer061
  Tool = -> Compound887
FEATURE [Part::Cut] Cut521
  Base = -> Cut520
  Placement = pos=(1,-3,65) rot=(0,0.707107,-0.707107;3.14159rad)
  Tool = -> Compound888
FEATURE [Part::Box] Box686  label="Krychle686"
  AttacherType = Attacher::AttachEngine3D
  Height = 10
  Length = 54
  Placement = pos=(-27.0044,59.998,75) rot=(0,0,1;0rad)
  Width = 68
FEATURE [Part::Box] Box688  label="Krychle688"
  AttacherType = Attacher::AttachEngine3D
  Height = 50
  Length = 42
  Placement = pos=(-21,58,38) rot=(0,0,1;0rad)
  Width = 64
FEATURE [Part::Cut] Cut500
  Base = -> Box686
  Tool = -> Box688
FEATURE [Part::Cylinder] Cylinder1727  label="Válec1727"
  Angle = 360
  AttacherType = Attacher::AttachEngine3D
  Height = 3
  Placement = pos=(-24,128,72) rot=(1,0,0;1.5708rad)
  Radius = 3
FEATURE [Part::Cylinder] Cylinder1728  label="Válec1728"
  Angle = 360
  AttacherType = Attacher::AttachEngine3D
  Height = 3
  Placement = pos=(24,128,72) rot=(1,0,0;1.5708rad)
  Radius = 3
FEATURE [Part::Compound] Compound871
  Links = -> [Cylinder1727,Cylinder1728]
  Placement = pos=(0,0,8) rot=(0,0,1;0rad)
FEATURE [Part::Box] Box689  label="Krychle689"
  AttacherType = Attacher::AttachEngine3D
  Height = 2
  Length = 7
  Placement = pos=(-28,70,-48) rot=(0,0,1;0rad)
  Width = 6
FEATURE [Part::Box] Box690  label="Krychle690"
  AttacherType = Attacher::AttachEngine3D
  Height = 2
  Length = 6
  Placement = pos=(-18,122,-48) rot=(0,0,1;0rad)
  Width = 6
FEATURE [Part::Box] Box691  label="Krychle691"
  AttacherType = Attacher::AttachEngine3D
  Height = 2
  Length = 6
  Placement = pos=(21,70,-48) rot=(0,0,1;0rad)
  Width = 6
FEATURE [Part::Box] Box692  label="Krychle692"
  AttacherType = Attacher::AttachEngine3D
  Height = 2
  Length = 6
  Placement = pos=(12,122,-48) rot=(0,0,1;0rad)
  Width = 6
FEATURE [Part::Compound] Compound872
  Links = -> [Box689,Box690,Box691,Box692]
  Placement = pos=(0,0,127) rot=(0,0,1;0rad)
FEATURE [Part::Cylinder] Cylinder1729  label="Válec1729"
  Angle = 360
  AttacherType = Attacher::AttachEngine3D
  Height = 50
  Placement = pos=(-24,140,72) rot=(1,0,0;1.5708rad)
  Radius = 1.5
FEATURE [Part::Cylinder] Cylinder1730  label="Válec1730"
  Angle = 360
  AttacherType = Attacher::AttachEngine3D
  Height = 50
  Placement = pos=(24,140,72) rot=(1,0,0;1.5708rad)
  Radius = 1.5
FEATURE [Part::Cylinder] Cylinder1731  label="Válec1731"
  Angle = 360
  AttacherType = Attacher::AttachEngine3D
  Height = 60
  Placement = pos=(24,73,-80) rot=(0,0,1;0rad)
  Radius = 1.5
FEATURE [Part::Cylinder] Cylinder1732  label="Válec1732"
  Angle = 360
  AttacherType = Attacher::AttachEngine3D
  Height = 60
  Placement = pos=(-24,73,-80) rot=(0,0,1;0rad)
  Radius = 1.5
FEATURE [Part::Cylinder] Cylinder1733  label="Válec1733"
  Angle = 360
  AttacherType = Attacher::AttachEngine3D
  Height = 60
  Placement = pos=(-15,125,-80) rot=(0,0,1;0rad)
  Radius = 1.5
FEATURE [Part::Compound] Compound873
  Links = -> [Cylinder1729,Cylinder1730]
  Placement = pos=(0,0,8) rot=(0,0,1;0rad)
FEATURE [Part::Cylinder] Cylinder1734  label="Válec1734"
  Angle = 360
  AttacherType = Attacher::AttachEngine3D
  Height = 60
  Placement = pos=(15,125,-80) rot=(0,0,1;0rad)
  Radius = 1.5
FEATURE [Part::Compound] Compound874
  Links = -> [Cylinder1731,Cylinder1732,Cylinder1733,Cylinder1734]
  Placement = pos=(0,0,120) rot=(0,0,1;0rad)
FEATURE [Part::Box] Box693  label="Krychle693"
  AttacherType = Attacher::AttachEngine3D
  Height = 10
  Length = 56
  Placement = pos=(-28,78,75) rot=(0,0,1;0rad)
  Width = 44
FEATURE [Part::Cut] Cut501
  Base = -> Cut500
  Tool = -> Box693
FEATURE [Part::Box] Box694  label="Krychle694"
  AttacherType = Attacher::AttachEngine3D
  Height = 9
  Length = 54
  Placement = pos=(-27.0044,59.998,75) rot=(0,0,1;0rad)
  Width = 68
FEATURE [Part::Box] Box695  label="Krychle695"
  AttacherType = Attacher::AttachEngine3D
  Height = 50
  Length = 42
  Placement = pos=(-21,58,40) rot=(0,0,1;0rad)
  Width = 64
FEATURE [Part::Cut] Cut502
  Base = -> Box694
  Placement = pos=(0,0,-9) rot=(0,0,1;0rad)
  Tool = -> Box695
FEATURE [Part::Chamfer] Chamfer055
  Base = -> Cut502
  Edges = 2 edges r=3: [Edge3,Edge15]
FEATURE [Part::Cylinder] Cylinder1735  label="Válec1735"
  Angle = 360
  AttacherType = Attacher::AttachEngine3D
  Height = 60
  Placement = pos=(15,125,-80) rot=(0,0,1;0rad)
  Radius = 1.5
FEATURE [Part::Cylinder] Cylinder1736  label="Válec1736"
  Angle = 360
  AttacherType = Attacher::AttachEngine3D
  Height = 60
  Placement = pos=(24,73,-80) rot=(0,0,1;0rad)
  Radius = 1.5
FEATURE [Part::Cylinder] Cylinder1737  label="Válec1737"
  Angle = 360
  AttacherType = Attacher::AttachEngine3D
  Height = 60
  Placement = pos=(-24,73,-80) rot=(0,0,1;0rad)
  Radius = 1.5
FEATURE [Part::Cylinder] Cylinder1738  label="Válec1738"
  Angle = 360
  AttacherType = Attacher::AttachEngine3D
  Height = 60
  Placement = pos=(-15,125,-80) rot=(0,0,1;0rad)
  Radius = 1.5
FEATURE [Part::Compound] Compound875
  Links = -> [Cylinder1736,Cylinder1737,Cylinder1738,Cylinder1735]
  Placement = pos=(0,0,120) rot=(0,0,1;0rad)
FEATURE [Part::Cut] Cut503
  Base = -> Cut501
  Tool = -> Compound875
FEATURE [Part::Cut] Cut504
  Base = -> Cut503
  Tool = -> Compound872
FEATURE [Part::Chamfer] Chamfer054
  Base = -> Cut504
  Edges = 2 edges r=3: [Edge32,Edge43]
FEATURE [Part::Cut] Cut505
  Base = -> Chamfer054
  Tool = -> Compound871
FEATURE [Part::Cut] Cut506
  Base = -> Cut505
  Tool = -> Compound873
FEATURE [Part::Cut] Cut507
  Base = -> Chamfer055
  Tool = -> Compound874
FEATURE [Part::Compound] Compound876
  Links = -> [Cut506,Cut507]
  Placement = pos=(1,7,65) rot=(0,0.707107,-0.707107;3.14159rad)
FEATURE [Part::Cylinder] Cylinder2650  label="Válec2620"
  Angle = 360
  AttacherType = Attacher::AttachEngine3D
  Height = 60
  Placement = pos=(24,73,-80) rot=(0,0,1;0rad)
  Radius = 1.5
FEATURE [Part::Cylinder] Cylinder2651  label="Válec2621"
  Angle = 360
  AttacherType = Attacher::AttachEngine3D
  Height = 60
  Placement = pos=(-24,73,-80) rot=(0,0,1;0rad)
  Radius = 1.5
FEATURE [Part::Cylinder] Cylinder2652  label="Válec2622"
  Angle = 360
  AttacherType = Attacher::AttachEngine3D
  Height = 60
  Placement = pos=(-15,125,-80) rot=(0,0,1;0rad)
  Radius = 1.5
FEATURE [Part::Cylinder] Cylinder2653  label="Válec2623"
  Angle = 360
  AttacherType = Attacher::AttachEngine3D
  Height = 60
  Placement = pos=(15,125,-80) rot=(0,0,1;0rad)
  Radius = 1.5
FEATURE [Part::Compound] Compound1172
  Links = -> [Cylinder2650,Cylinder2651,Cylinder2652,Cylinder2653]
  Placement = pos=(0,0,120) rot=(0,0,1;0rad)
FEATURE [Part::Box] Box893  label="Krychle892"
  AttacherType = Attacher::AttachEngine3D
  Height = 9
  Length = 54
  Placement = pos=(-27,60,76) rot=(0,0,1;0rad)
  Width = 68
FEATURE [Part::Box] Box894  label="Krychle893"
  AttacherType = Attacher::AttachEngine3D
  Height = 50
  Length = 42
  Placement = pos=(-21,58,40) rot=(0,0,1;0rad)
  Width = 64
FEATURE [Part::Cut] Cut978
  Base = -> Box893
  Placement = pos=(0,0,-9) rot=(0,0,1;0rad)
  Tool = -> Box894
FEATURE [Part::Chamfer] Chamfer127
  Base = -> Cut978
  Edges = 2 edges r=3: [Edge3,Edge15]
FEATURE [Part::Cut] Cut979
  Base = -> Chamfer127
  Tool = -> Compound1172
FEATURE [Part::Cylinder] Cylinder2654  label="Válec2624"
  Angle = 360
  AttacherType = Attacher::AttachEngine3D
  Height = 3
  Placement = pos=(24,73,-80) rot=(0,0,1;0rad)
  Radius = 4.5
FEATURE [Part::Cylinder] Cylinder2655  label="Válec2625"
  Angle = 360
  AttacherType = Attacher::AttachEngine3D
  Height = 3
  Placement = pos=(-24,73,-80) rot=(0,0,1;0rad)
  Radius = 4.5
FEATURE [Part::Cylinder] Cylinder2656  label="Válec2626"
  Angle = 360
  AttacherType = Attacher::AttachEngine3D
  Height = 3
  Placement = pos=(-15,125,-80) rot=(0,0,1;0rad)
  Radius = 3
FEATURE [Part::Cylinder] Cylinder2657  label="Válec2627"
  Angle = 360
  AttacherType = Attacher::AttachEngine3D
  Height = 3
  Placement = pos=(15,125,-80) rot=(0,0,1;0rad)
  Radius = 3
FEATURE [Part::Compound] Compound1173
  Links = -> [Cylinder2654,Cylinder2655,Cylinder2657,Cylinder2656]
  Placement = pos=(0,0,171) rot=(0,0,1;0rad)
FEATURE [Part::Box] Box895  label="Krychle894"
  AttacherType = Attacher::AttachEngine3D
  Height = 9
  Length = 54
  Placement = pos=(-27,70,75) rot=(0,0,1;0rad)
  Width = 58
FEATURE [Part::Box] Box896  label="Krychle895"
  AttacherType = Attacher::AttachEngine3D
  Height = 50
  Length = 42
  Placement = pos=(-21,76,38) rot=(0,0,1;0rad)
  Width = 46
FEATURE [Part::Cylinder] Cylinder2658  label="Válec2628"
  Angle = 360
  AttacherType = Attacher::AttachEngine3D
  Height = 60
  Placement = pos=(24,73,-80) rot=(0,0,1;0rad)
  Radius = 1.5
FEATURE [Part::Cylinder] Cylinder2659  label="Válec2629"
  Angle = 360
  AttacherType = Attacher::AttachEngine3D
  Height = 60
  Placement = pos=(-24,73,-80) rot=(0,0,1;0rad)
  Radius = 1.5
FEATURE [Part::Cylinder] Cylinder2660  label="Válec2630"
  Angle = 360
  AttacherType = Attacher::AttachEngine3D
  Height = 60
  Placement = pos=(-15,125,-80) rot=(0,0,1;0rad)
  Radius = 1.5
FEATURE [Part::Cylinder] Cylinder2661  label="Válec2631"
  Angle = 360
  AttacherType = Attacher::AttachEngine3D
  Height = 60
  Placement = pos=(15,125,-80) rot=(0,0,1;0rad)
  Radius = 1.5
FEATURE [Part::Compound] Compound1174
  Links = -> [Cylinder2658,Cylinder2659,Cylinder2660,Cylinder2661]
  Placement = pos=(0,0,120) rot=(0,0,1;0rad)
FEATURE [Part::Cut] Cut981
  Base = -> Box895
  Placement = pos=(0,0,10) rot=(0,0,1;0rad)
  Tool = -> Box896
FEATURE [Part::Box] Box897  label="Krychle896"
  AttacherType = Attacher::AttachEngine3D
  Height = 10
  Length = 54
  Placement = pos=(-27,70,75) rot=(0,0,1;0rad)
  Width = 58
FEATURE [Part::Box] Box898  label="Krychle897"
  AttacherType = Attacher::AttachEngine3D
  Height = 50
  Length = 42
  Placement = pos=(-21,76,38) rot=(0,0,1;0rad)
  Width = 46
FEATURE [Part::Cylinder] Cylinder2662  label="Válec2632"
  Angle = 360
  AttacherType = Attacher::AttachEngine3D
  Height = 3
  Placement = pos=(-24,128,72) rot=(1,0,0;1.5708rad)
  Radius = 3
FEATURE [Part::Cylinder] Cylinder2663  label="Válec2633"
  Angle = 360
  AttacherType = Attacher::AttachEngine3D
  Height = 3
  Placement = pos=(24,128,72) rot=(1,0,0;1.5708rad)
  Radius = 3
FEATURE [Part::Box] Box899  label="Krychle898"
  AttacherType = Attacher::AttachEngine3D
  Height = 2
  Length = 7
  Placement = pos=(-28,70,-48) rot=(0,0,1;0rad)
  Width = 6
FEATURE [Part::Box] Box900  label="Krychle899"
  AttacherType = Attacher::AttachEngine3D
  Height = 2
  Length = 6
  Placement = pos=(-18,122,-48) rot=(0,0,1;0rad)
  Width = 6
FEATURE [Part::Box] Box901  label="Krychle900"
  AttacherType = Attacher::AttachEngine3D
  Height = 2
  Length = 6
  Placement = pos=(21,70,-48) rot=(0,0,1;0rad)
  Width = 6
FEATURE [Part::Box] Box902  label="Krychle901"
  AttacherType = Attacher::AttachEngine3D
  Height = 2
  Length = 6
  Placement = pos=(12,122,-48) rot=(0,0,1;0rad)
  Width = 6
FEATURE [Part::Cylinder] Cylinder2664  label="Válec2634"
  Angle = 360
  AttacherType = Attacher::AttachEngine3D
  Height = 50
  Placement = pos=(-24,140,72) rot=(1,0,0;1.5708rad)
  Radius = 1.5
FEATURE [Part::Compound] Compound1175
  Links = -> [Cylinder2662,Cylinder2663]
  Placement = pos=(0,0,8) rot=(0,0,1;0rad)
FEATURE [Part::Compound] Compound1176
  Links = -> [Box899,Box900,Box901,Box902]
  Placement = pos=(0,0,127) rot=(0,0,1;0rad)
FEATURE [Part::Cut] Cut983
  Base = -> Box897
  Tool = -> Box898
FEATURE [Part::Cylinder] Cylinder2665  label="Válec2635"
  Angle = 360
  AttacherType = Attacher::AttachEngine3D
  Height = 50
  Placement = pos=(24,140,72) rot=(1,0,0;1.5708rad)
  Radius = 1.5
FEATURE [Part::Compound] Compound1177
  Links = -> [Cylinder2664,Cylinder2665]
  Placement = pos=(0,0,8) rot=(0,0,1;0rad)
FEATURE [Part::Box] Box903  label="Krychle902"
  AttacherType = Attacher::AttachEngine3D
  Height = 10
  Length = 56
  Placement = pos=(-28,78,75) rot=(0,0,1;0rad)
  Width = 44
FEATURE [Part::Cut] Cut984
  Base = -> Cut983
  Tool = -> Box903
FEATURE [Part::Cylinder] Cylinder2666  label="Válec2636"
  Angle = 360
  AttacherType = Attacher::AttachEngine3D
  Height = 60
  Placement = pos=(15,125,-80) rot=(0,0,1;0rad)
  Radius = 1.5
FEATURE [Part::Cylinder] Cylinder2667  label="Válec2637"
  Angle = 360
  AttacherType = Attacher::AttachEngine3D
  Height = 60
  Placement = pos=(24,73,-80) rot=(0,0,1;0rad)
  Radius = 1.5
FEATURE [Part::Cylinder] Cylinder2668  label="Válec2638"
  Angle = 360
  AttacherType = Attacher::AttachEngine3D
  Height = 60
  Placement = pos=(-24,73,-80) rot=(0,0,1;0rad)
  Radius = 1.5
FEATURE [Part::Cylinder] Cylinder2669  label="Válec2639"
  Angle = 360
  AttacherType = Attacher::AttachEngine3D
  Height = 60
  Placement = pos=(-15,125,-80) rot=(0,0,1;0rad)
  Radius = 1.5
FEATURE [Part::Compound] Compound1178
  Links = -> [Cylinder2667,Cylinder2668,Cylinder2669,Cylinder2666]
  Placement = pos=(0,0,120) rot=(0,0,1;0rad)
FEATURE [Part::Cut] Cut985
  Base = -> Cut984
  Tool = -> Compound1178
FEATURE [Part::Box] Box904  label="Krychle903"
  AttacherType = Attacher::AttachEngine3D
  Height = 2
  Length = 7
  Placement = pos=(-28,70,-48) rot=(0,0,1;0rad)
  Width = 6
FEATURE [Part::Box] Box905  label="Krychle904"
  AttacherType = Attacher::AttachEngine3D
  Height = 2
  Length = 6
  Placement = pos=(-18,122,-48) rot=(0,0,1;0rad)
  Width = 6
FEATURE [Part::Box] Box906  label="Krychle905"
  AttacherType = Attacher::AttachEngine3D
  Height = 2
  Length = 6
  Placement = pos=(21,70,-48) rot=(0,0,1;0rad)
  Width = 6
FEATURE [Part::Box] Box907  label="Krychle906"
  AttacherType = Attacher::AttachEngine3D
  Height = 2
  Length = 6
  Placement = pos=(12,122,-48) rot=(0,0,1;0rad)
  Width = 6
FEATURE [Part::Compound] Compound1179
  Links = -> [Box904,Box905,Box906,Box907]
  Placement = pos=(0,0,118) rot=(0,0,1;0rad)
FEATURE [Part::Cut] Cut989
  Base = -> Cut979
  Placement = pos=(1,8,65) rot=(0,0.707107,-0.707107;3.14159rad)
  Tool = -> Compound1179
FEATURE [Part::Chamfer] Chamfer130
  Base = -> Cut981
  Edges = 2 edges r=3: [Edge3,Edge15]
FEATURE [Part::Cut] Cut990
  Base = -> Chamfer130
  Tool = -> Compound1174
FEATURE [Part::Chamfer] Chamfer131
  Base = -> Cut985
  Edges = 2 edges r=3: [Edge32,Edge43]
FEATURE [Part::Cut] Cut991
  Base = -> Chamfer131
  Tool = -> Compound1175
FEATURE [Part::Cut] Cut992
  Base = -> Cut991
  Tool = -> Compound1177
FEATURE [Part::Compound] Compound1180  label="G-mini_encoder_front-holder"
  Links = -> [Cut990,Cut992]
  Placement = pos=(0,-3,65) rot=(0,0.707107,-0.707107;3.14159rad)
FEATURE [Part::Box] Box908  label="Krychle907"
  AttacherType = Attacher::AttachEngine3D
  Height = 6
  Length = 8
  Placement = pos=(-38,-68,5) rot=(0,0,1;0rad)
  Width = 69
FEATURE [Part::Box] Box909  label="Krychle908"
  AttacherType = Attacher::AttachEngine3D
  Height = 6
  Length = 8
  Placement = pos=(30,-68,5) rot=(0,0,1;0rad)
  Width = 69
FEATURE [Part::Box] Box910  label="Krychle909"
  AttacherType = Attacher::AttachEngine3D
  Height = 6
  Length = 20
  Placement = pos=(-38,-40,5) rot=(0,0,1;0rad)
  Width = 20
FEATURE [Part::Cylinder] Cylinder2670  label="Válec2640"
  Angle = 360
  AttacherType = Attacher::AttachEngine3D
  Height = 16
  Placement = pos=(-22,-40,0) rot=(0,0,1;0rad)
  Radius = 8
FEATURE [Part::Cylinder] Cylinder2671  label="Válec2641"
  Angle = 360
  AttacherType = Attacher::AttachEngine3D
  Height = 16
  Placement = pos=(22,-40,0) rot=(0,0,1;0rad)
  Radius = 8
FEATURE [Part::Box] Box911  label="Krychle910"
  AttacherType = Attacher::AttachEngine3D
  Height = 6
  Length = 20
  Placement = pos=(18,-40,5) rot=(0,0,1;0rad)
  Width = 20
FEATURE [Part::Cylinder] Cylinder2672  label="Válec2642"
  Angle = 360
  AttacherType = Attacher::AttachEngine3D
  Height = 16
  Radius = 38
FEATURE [Part::Cylinder] Cylinder2673  label="Válec2643"
  Angle = 360
  AttacherType = Attacher::AttachEngine3D
  Height = 16
  Radius = 38
FEATURE [Part::Cylinder] Cylinder2674  label="Válec2644"
  Angle = 360
  AttacherType = Attacher::AttachEngine3D
  Height = 16
  Radius = 38
FEATURE [Part::Chamfer] Chamfer132
  Base = -> Box908
  Edges = 1 edges r=1: [Edge2]
FEATURE [Part::Chamfer] Chamfer133
  Base = -> Box909
  Edges = 1 edges r=1: [Edge6]
FEATURE [Part::Compound] Compound1181
  Links = -> [Box911,Box910]
FEATURE [Part::Compound] Compound1182
  Links = -> [Cylinder2671,Cylinder2670]
FEATURE [Part::Cut] Cut993
  Base = -> Compound1181
  Tool = -> Compound1182
FEATURE [Part::Chamfer] Chamfer134
  Base = -> Cut993
  Edges = 1 edges r=1: [Edge8]
FEATURE [Part::Chamfer] Chamfer135
  Base = -> Chamfer133
  Edges = 1 edges r=1: [Edge15]
FEATURE [Part::Cut] Cut996
  Base = -> Chamfer135
  Tool = -> Cylinder2674
FEATURE [Part::Chamfer] Chamfer136
  Base = -> Chamfer134
  Edges = 1 edges r=1: [Edge8]
FEATURE [Part::Chamfer] Chamfer137
  Base = -> Chamfer136
  Edges = 1 edges r=1: [Edge23]
FEATURE [Part::Chamfer] Chamfer138
  Base = -> Chamfer137
  Edges = 1 edges r=1: [Edge16]
FEATURE [Part::Cut] Cut995
  Base = -> Chamfer138
  Tool = -> Cylinder2673
FEATURE [Part::Chamfer] Chamfer139
  Base = -> Chamfer132
  Edges = 1 edges r=1: [Edge15]
FEATURE [Part::Cut] Cut994
  Base = -> Chamfer139
  Tool = -> Cylinder2672
FEATURE [Part::Compound] Compound1183
  Links = -> [Cut994,Cut995,Cut996]
FEATURE [Part::Box] Box912  label="Krychle911"
  AttacherType = Attacher::AttachEngine3D
  Height = 32
  Length = 15
  Placement = pos=(-38,-68,5) rot=(0,0,1;0rad)
  Width = 13.5
FEATURE [Part::FeaturePython] Tube125  # WARN: FeaturePython — macro-defined, semantics opaque (R4)
  AttacherType = Attacher::AttachEngine3D
  Height = 1
  InnerRadius = 12
  OuterRadius = 14
  Placement = pos=(0,0,1) rot=(0,0,1;0rad)
FEATURE [Part::Compound] Compound1184
  Links = -> [Cut976,Compound1183]
FEATURE [Part::Compound] Compound1185
  Links = -> [Common006,Compound1184]
FEATURE [Part::Compound] Compound1186
  Links = -> [Tube125,Compound1185]
FEATURE [Part::Box] Box913  label="Krychle912"
  AttacherType = Attacher::AttachEngine3D
  Height = 32
  Length = 15
  Placement = pos=(-38,-68,5) rot=(0,0,1;0rad)
  Width = 13.5
FEATURE [Part::Box] Box914  label="Krychle913"
  AttacherType = Attacher::AttachEngine3D
  Height = 6
  Length = 8
  Placement = pos=(-38,-79,5) rot=(0,0,1;0rad)
  Width = 80
FEATURE [Part::Box] Box915  label="Krychle914"
  AttacherType = Attacher::AttachEngine3D
  Height = 6
  Length = 8
  Placement = pos=(30,-79,5) rot=(0,0,1;0rad)
  Width = 80
FEATURE [Part::Box] Box916  label="Krychle915"
  AttacherType = Attacher::AttachEngine3D
  Height = 6
  Length = 20
  Placement = pos=(-38,-40,5) rot=(0,0,1;0rad)
  Width = 20
FEATURE [Part::Cylinder] Cylinder2675  label="Válec2645"
  Angle = 360
  AttacherType = Attacher::AttachEngine3D
  Height = 16
  Placement = pos=(-22,-40,0) rot=(0,0,1;0rad)
  Radius = 8
FEATURE [Part::Cylinder] Cylinder2676  label="Válec2646"
  Angle = 360
  AttacherType = Attacher::AttachEngine3D
  Height = 16
  Placement = pos=(22,-40,0) rot=(0,0,1;0rad)
  Radius = 8
FEATURE [Part::Box] Box917  label="Krychle916"
  AttacherType = Attacher::AttachEngine3D
  Height = 6
  Length = 20
  Placement = pos=(18,-40,5) rot=(0,0,1;0rad)
  Width = 20
FEATURE [Part::Cylinder] Cylinder2677  label="Válec2647"
  Angle = 360
  AttacherType = Attacher::AttachEngine3D
  Height = 16
  Radius = 36
FEATURE [Part::Cylinder] Cylinder2678  label="Válec2648"
  Angle = 360
  AttacherType = Attacher::AttachEngine3D
  Height = 16
  Radius = 36
FEATURE [Part::Cylinder] Cylinder2679  label="Válec2649"
  Angle = 360
  AttacherType = Attacher::AttachEngine3D
  Height = 16
  Radius = 36
FEATURE [Part::Box] Box918  label="Krychle917"
  AttacherType = Attacher::AttachEngine3D
  Height = 32
  Length = 15
  Placement = pos=(23,-68,5) rot=(0,0,1;0rad)
  Width = 13.5
FEATURE [Part::Chamfer] Chamfer140
  Base = -> Box914
  Edges = 1 edges r=1: [Edge2]
FEATURE [Part::Chamfer] Chamfer141
  Base = -> Box915
  Edges = 1 edges r=1: [Edge6]
FEATURE [Part::Compound] Compound1192
  Links = -> [Box917,Box916]
FEATURE [Part::Compound] Compound1193
  Links = -> [Cylinder2676,Cylinder2675]
FEATURE [Part::Chamfer] Chamfer143
  Base = -> Chamfer141
  Edges = 1 edges r=1: [Edge15]
FEATURE [Part::Chamfer] Chamfer147
  Base = -> Chamfer140
  Edges = 1 edges r=1: [Edge15]
FEATURE [Part::Cut] Cut1007
  Base = -> Chamfer143
  Tool = -> Cylinder2679
FEATURE [Part::Cut] Cut1009
  Base = -> Chamfer147
  Tool = -> Cylinder2677
FEATURE [Part::Cut] Cut1010
  Base = -> Compound1192
  Tool = -> Compound1193
FEATURE [Part::Chamfer] Chamfer142
  Base = -> Cut1010
  Edges = 1 edges r=1: [Edge8]
FEATURE [Part::Chamfer] Chamfer144
  Base = -> Chamfer142
  Edges = 1 edges r=1: [Edge8]
FEATURE [Part::Chamfer] Chamfer145
  Base = -> Chamfer144
  Edges = 1 edges r=1: [Edge23]
FEATURE [Part::Chamfer] Chamfer146
  Base = -> Chamfer145
  Edges = 1 edges r=1: [Edge16]
FEATURE [Part::Cut] Cut1008
  Base = -> Chamfer146
  Tool = -> Cylinder2678
FEATURE [Part::Cylinder] Cylinder2680  label="Válec2650"
  Angle = 360
  AttacherType = Attacher::AttachEngine3D
  Height = 3
  Placement = pos=(-19.4454,-19.4454,19) rot=(0,0,1;2.35619rad)
  Radius = 3
FEATURE [Part::Cylinder] Cylinder2681  label="Válec2651"
  Angle = 360
  AttacherType = Attacher::AttachEngine3D
  Height = 5
  Placement = pos=(1.1e-14,-27.5,19.5) rot=(0,0,1;3.14159rad)
  Radius = 3
FEATURE [Part::Cylinder] Cylinder2682  label="Válec2652"
  Angle = 360
  AttacherType = Attacher::AttachEngine3D
  Height = 20
  Placement = pos=(-19.4454,19.4454,19) rot=(0,0,1;0.785398rad)
  Radius = 1.5
FEATURE [Part::Cylinder] Cylinder2683  label="Válec2653"
  Angle = 360
  AttacherType = Attacher::AttachEngine3D
  Height = 20
  Placement = pos=(-19.4454,-19.4454,19) rot=(0,0,1;2.35619rad)
  Radius = 1.5
FEATURE [Part::Cylinder] Cylinder2684  label="Válec2654"
  Angle = 360
  AttacherType = Attacher::AttachEngine3D
  Height = 20
  Placement = pos=(19.4454,-19.4454,19) rot=(0,0,1;3.92699rad)
  Radius = 1.5
FEATURE [Part::Cylinder] Cylinder2685  label="Válec2655"
  Angle = 360
  AttacherType = Attacher::AttachEngine3D
  Height = 3
  Placement = pos=(-19.45,19.45,19) rot=(0,0,1;0.785398rad)
  Radius = 3
FEATURE [Part::Cylinder] Cylinder2686  label="Válec2656"
  Angle = 360
  AttacherType = Attacher::AttachEngine3D
  Height = 3
  Placement = pos=(-27.5,-4e-15,19) rot=(0,0,1;1.5708rad)
  Radius = 3
FEATURE [Part::Cylinder] Cylinder2687  label="Válec2657"
  Angle = 360
  AttacherType = Attacher::AttachEngine3D
  Height = 5
  Placement = pos=(19.45,-19.45,19.5) rot=(0,0,1;3.92699rad)
  Radius = 3
FEATURE [Part::FeaturePython] Tube126  # WARN: FeaturePython — macro-defined, semantics opaque (R4)
  AttacherType = Attacher::AttachEngine3D
  Height = 24
  InnerRadius = 22
  OuterRadius = 31
  Placement = pos=(0,-16,37) rot=(1,0,0;1.5708rad)
FEATURE [Part::Cylinder] Cylinder2688  label="Válec2658"
  Angle = 360
  AttacherType = Attacher::AttachEngine3D
  Height = 3
  Placement = pos=(27.5,1.2e-14,19) rot=(0,0,-1;1.5708rad)
  Radius = 3
FEATURE [Part::Cylinder] Cylinder2689  label="Válec2659"
  Angle = 360
  AttacherType = Attacher::AttachEngine3D
  Height = 3
  Placement = pos=(19.4454,19.4454,19) rot=(0,0,-1;0.785398rad)
  Radius = 3
FEATURE [Part::Cylinder] Cylinder2690  label="Válec2660"
  Angle = 360
  AttacherType = Attacher::AttachEngine3D
  Height = 20
  Placement = pos=(-27.5,-4e-15,19) rot=(0,0,1;1.5708rad)
  Radius = 1.5
FEATURE [Part::Cylinder] Cylinder2691  label="Válec2661"
  Angle = 360
  AttacherType = Attacher::AttachEngine3D
  Height = 20
  Placement = pos=(1.1e-14,-27.5,19) rot=(0,0,1;3.14159rad)
  Radius = 1.5
FEATURE [Part::Cylinder] Cylinder2692  label="Válec2662"
  Angle = 360
  AttacherType = Attacher::AttachEngine3D
  Height = 3
  Placement = pos=(0,27.5,19) rot=(0,0,1;0rad)
  Radius = 3
FEATURE [Part::Cylinder] Cylinder2693  label="Válec2663"
  Angle = 360
  AttacherType = Attacher::AttachEngine3D
  Height = 20
  Placement = pos=(19.4454,19.4454,19) rot=(0,0,-1;0.785398rad)
  Radius = 1.5
FEATURE [Part::Cylinder] Cylinder2694  label="Válec2664"
  Angle = 360
  AttacherType = Attacher::AttachEngine3D
  Height = 20
  Placement = pos=(27.5,1.2e-14,19) rot=(0,0,-1;1.5708rad)
  Radius = 1.5
FEATURE [Part::Cylinder] Cylinder2695  label="Válec2665"
  Angle = 360
  AttacherType = Attacher::AttachEngine3D
  Height = 6
  Radius = 38
FEATURE [Part::Compound] Compound1195
  Links = -> [Cylinder2692,Cylinder2685,Cylinder2686,Cylinder2680,Cylinder2681,Cylinder2687,Cylinder2688,Cylinder2689]
  Placement = pos=(0,0,-19) rot=(0,0,1;0rad)
FEATURE [Part::Cut] Cut1014
  Base = -> Cylinder2695
  Tool = -> Compound1195
FEATURE [Part::Cylinder] Cylinder2696  label="Válec2666"
  Angle = 360
  AttacherType = Attacher::AttachEngine3D
  Height = 20
  Placement = pos=(0,27.5,19) rot=(0,0,1;0rad)
  Radius = 1.5
FEATURE [Part::Compound] Compound1194
  Links = -> [Cylinder2696,Cylinder2682,Cylinder2690,Cylinder2683,Cylinder2691,Cylinder2684,Cylinder2694,Cylinder2693]
  Placement = pos=(0,0,-23) rot=(0,0,1;0rad)
FEATURE [Part::Cut] Cut1012
  Base = -> Cut1014
  Tool = -> Compound1194
FEATURE [Part::Cylinder] Cylinder2697  label="Válec2667"
  Angle = 360
  AttacherType = Attacher::AttachEngine3D
  Height = 5
  Placement = pos=(0,0,1) rot=(0,0,1;0rad)
  Radius = 14
FEATURE [Part::Cut] Cut1013
  Base = -> Cut1012
  Tool = -> Cylinder2697
FEATURE [Part::Chamfer] Chamfer148
  Base = -> Cut1013
  Edges = 1 edges r=1: [Edge3]
  Placement = pos=(1e-15,0,11) rot=(-0.19509,0.980785,0;3.14159rad)
FEATURE [Part::Cut] Cut1011
  Base = -> Chamfer148
  Tool = -> Tube126
FEATURE [Part::Compound] Compound1196
  Links = -> [Box918,Box913]
  Placement = pos=(0,-17.5,0) rot=(0,0,1;0rad)
FEATURE [Part::Compound] Compound1197
  Links = -> [Cut1007,Cut1009]
FEATURE [Part::Cut] Cut1002
  Base = -> Compound1197
  Tool = -> Compound1196
FEATURE [Part::Box] Box919  label="Krychle918"
  AttacherType = Attacher::AttachEngine3D
  Height = 6
  Length = 6
  Placement = pos=(30,-27,5) rot=(0,0,1;0rad)
  Width = 2
FEATURE [Part::Box] Box920  label="Krychle919"
  AttacherType = Attacher::AttachEngine3D
  Height = 6
  Length = 6
  Placement = pos=(-36,-27,5) rot=(0,0,1;0rad)
  Width = 2
FEATURE [Part::Compound] Compound1191
  Links = -> [Box919,Box920]
FEATURE [Part::Cut] Cut1003
  Base = -> Cut1002
  Tool = -> Compound1191
FEATURE [Part::Box] Box921  label="Krychle920"
  AttacherType = Attacher::AttachEngine3D
  Height = 6
  Length = 6
  Placement = pos=(30,-27,5) rot=(0,0,1;0rad)
  Width = 2
FEATURE [Part::Box] Box922  label="Krychle921"
  AttacherType = Attacher::AttachEngine3D
  Height = 6
  Length = 6
  Placement = pos=(-36,-27,5) rot=(0,0,1;0rad)
  Width = 2
FEATURE [Part::Compound] Compound1198
  Links = -> [Box921,Box922]
FEATURE [Part::Cut] Cut1004
  Base = -> Cut1008
  Tool = -> Compound1198
FEATURE [Part::Cylinder] Cylinder2698  label="Válec2668"
  Angle = 360
  AttacherType = Attacher::AttachEngine3D
  Height = 60
  Placement = pos=(-33,-10,8) rot=(1,0,0;1.5708rad)
  Radius = 1.5
FEATURE [Part::Cylinder] Cylinder2699  label="Válec2669"
  Angle = 360
  AttacherType = Attacher::AttachEngine3D
  Height = 60
  Placement = pos=(33,-10,8) rot=(1,0,0;1.5708rad)
  Radius = 1.5
FEATURE [Part::Compound] Compound1199
  Links = -> [Cylinder2698,Cylinder2699]
  Placement = pos=(0,-1,0) rot=(0,0,1;0rad)
FEATURE [Part::Cut] Cut1006
  Base = -> Cut1011
  Tool = -> Compound1199
FEATURE [Part::Cylinder] Cylinder2700  label="Válec2670"
  Angle = 360
  AttacherType = Attacher::AttachEngine3D
  Height = 100
  Placement = pos=(-33,-10,8) rot=(1,0,0;1.5708rad)
  Radius = 1.5
FEATURE [Part::Cylinder] Cylinder2701  label="Válec2671"
  Angle = 360
  AttacherType = Attacher::AttachEngine3D
  Height = 100
  Placement = pos=(33,-10,8) rot=(1,0,0;1.5708rad)
  Radius = 1.5
FEATURE [Part::Compound] Compound1200
  Links = -> [Cylinder2700,Cylinder2701]
  Placement = pos=(0,-1,0) rot=(0,0,1;0rad)
FEATURE [Part::Cut] Cut1005
  Base = -> Cut1003
  Tool = -> Compound1200
FEATURE [Part::Cylinder] Cylinder2702  label="Válec2672"
  Angle = 360
  AttacherType = Attacher::AttachEngine3D
  Height = 60
  Placement = pos=(-33,-10,8) rot=(1,0,0;1.5708rad)
  Radius = 1.5
FEATURE [Part::Cylinder] Cylinder2703  label="Válec2673"
  Angle = 360
  AttacherType = Attacher::AttachEngine3D
  Height = 60
  Placement = pos=(33,-10,8) rot=(1,0,0;1.5708rad)
  Radius = 1.5
FEATURE [Part::Compound] Compound1201
  Links = -> [Cylinder2702,Cylinder2703]
  Placement = pos=(0,-4,0) rot=(0,0,1;0rad)
FEATURE [Part::Cut] Cut1015
  Base = -> Cut1004
  Tool = -> Compound1201
FEATURE [Part::FeaturePython] Tube127  # WARN: FeaturePython — macro-defined, semantics opaque (R4)
  AttacherType = Attacher::AttachEngine3D
  Height = 1
  InnerRadius = 12
  OuterRadius = 14
  Placement = pos=(0,0,9) rot=(0,0,1;0rad)
FEATURE [Part::Cylinder] Cylinder2704  label="Válec2674"
  Angle = 360
  AttacherType = Attacher::AttachEngine3D
  Height = 20
  Radius = 38
FEATURE [Part::Box] Box923  label="Krychle922"
  AttacherType = Attacher::AttachEngine3D
  Height = 7
  Length = 6
  Placement = pos=(15,-8,10) rot=(0,0,1;0rad)
  Width = 44
FEATURE [Part::Box] Box924  label="Krychle923"
  AttacherType = Attacher::AttachEngine3D
  Height = 7
  Length = 6
  Placement = pos=(-21,-8,10) rot=(0,0,1;0rad)
  Width = 44
FEATURE [Part::Compound] Compound1204
  Links = -> [Box923,Box924]
FEATURE [Part::Common] Common007
  Base = -> Compound1204
  Tool = -> Cylinder2704
FEATURE [Part::Chamfer] Chamfer149
  Base = -> Common007
  Edges = 2 edges r=1: [Edge6,Edge13]
FEATURE [Part::Cylinder] Cylinder2705  label="Válec2675"
  Angle = 360
  AttacherType = Attacher::AttachEngine3D
  Height = 64
  Placement = pos=(-26,-1,13) rot=(0,1,0;1.5708rad)
  Radius = 1.5
FEATURE [Part::Cylinder] Cylinder2706  label="Válec2676"
  Angle = 360
  AttacherType = Attacher::AttachEngine3D
  Height = 3
  Placement = pos=(-26,-1,13) rot=(0,1,0;1.5708rad)
  Radius = 3
FEATURE [Part::Cylinder] Cylinder2707  label="Válec2677"
  Angle = 360
  AttacherType = Attacher::AttachEngine3D
  Height = 3
  Placement = pos=(-26,-1,13) rot=(0,1,0;1.5708rad)
  Radius = 3
FEATURE [Part::Cylinder] Cylinder2708  label="Válec2678"
  Angle = 360
  AttacherType = Attacher::AttachEngine3D
  Height = 3
  Placement = pos=(-26,14,13) rot=(0,1,0;1.5708rad)
  Radius = 3
FEATURE [Part::Cylinder] Cylinder2709  label="Válec2679"
  Angle = 360
  AttacherType = Attacher::AttachEngine3D
  Height = 64
  Placement = pos=(-26,14,13) rot=(0,1,0;1.5708rad)
  Radius = 1.5
FEATURE [Part::Cylinder] Cylinder2710  label="Válec2680"
  Angle = 360
  AttacherType = Attacher::AttachEngine3D
  Height = 64
  Placement = pos=(-26,29,13) rot=(0,1,0;1.5708rad)
  Radius = 1.5
FEATURE [Part::Compound] Compound1203
  Links = -> [Cylinder2709,Cylinder2705,Cylinder2710]
  Placement = pos=(0,-2,1) rot=(0,0,1;0rad)
FEATURE [Part::Cylinder] Cylinder2711  label="Válec2681"
  Angle = 360
  AttacherType = Attacher::AttachEngine3D
  Height = 3
  Placement = pos=(-26,29,13) rot=(0,1,0;1.5708rad)
  Radius = 3
FEATURE [Part::Compound] Compound1202
  Links = -> [Cylinder2708,Cylinder2706,Cylinder2711]
  Placement = pos=(5,-2,1) rot=(0,0,1;0rad)
FEATURE [Part::Cylinder] Cylinder2712  label="Válec2682"
  Angle = 360
  AttacherType = Attacher::AttachEngine3D
  Height = 3
  Placement = pos=(-26,29,13) rot=(0,1,0;1.5708rad)
  Radius = 3
FEATURE [Part::Cylinder] Cylinder2713  label="Válec2683"
  Angle = 360
  AttacherType = Attacher::AttachEngine3D
  Height = 3
  Placement = pos=(-26,14,13) rot=(0,1,0;1.5708rad)
  Radius = 3
FEATURE [Part::Compound] Compound1205
  Links = -> [Cylinder2713,Cylinder2707,Cylinder2712]
  Placement = pos=(44,-2,1) rot=(0,0,1;0rad)
FEATURE [Part::Cut] Cut988
  Base = -> Chamfer149
  Tool = -> Compound1205
FEATURE [Part::Cut] Cut1017
  Base = -> Cut988
  Tool = -> Compound1202
FEATURE [Part::Cut] Cut1016
  Base = -> Cut1017
  Tool = -> Compound1203
FEATURE [Part::Compound] Compound1206  label="Wrist_side-actuator"
  Links = -> [Cut1005,Cut1006,Cut1015,Tube127,Cut1016]
FEATURE [Part::Torus] Torus005  label="Anuloid005"
  Angle1 = -180
  Angle2 = 180
  Angle3 = 360
  AttacherType = Attacher::AttachEngine3D
  Placement = pos=(17,-98,10) rot=(1,0,0;1.5708rad)
  Radius1 = 34
  Radius2 = 2
FEATURE [Part::Box] Box925  label="Krychle924"
  AttacherType = Attacher::AttachEngine3D
  Height = 40
  Length = 17
  Placement = pos=(21,-68,-3) rot=(0,0,1;0rad)
  Width = 13.5
FEATURE [Part::Box] Box926  label="Krychle925"
  AttacherType = Attacher::AttachEngine3D
  Height = 40
  Length = 17
  Placement = pos=(-38,-68,-3) rot=(0,0,1;0rad)
  Width = 13.5
FEATURE [Part::Compound] Compound1207
  Links = -> [Box925,Box926]
  Placement = pos=(0,-6,0) rot=(0,0,1;0rad)
FEATURE [Part::Cylinder] Cylinder2714  label="Válec2684"
  Angle = 360
  AttacherType = Attacher::AttachEngine3D
  Height = 16
  Radius = 38
FEATURE [Part::Cylinder] Cylinder2715  label="Válec2685"
  Angle = 360
  AttacherType = Attacher::AttachEngine3D
  Height = 16
  Radius = 38
FEATURE [Part::Box] Box927  label="Krychle926"
  AttacherType = Attacher::AttachEngine3D
  Height = 6
  Length = 8
  Placement = pos=(-38,-68,5) rot=(0,0,1;0rad)
  Width = 69
FEATURE [Part::Chamfer] Chamfer151
  Base = -> Box927
  Edges = 1 edges r=1: [Edge2]
FEATURE [Part::Box] Box928  label="Krychle927"
  AttacherType = Attacher::AttachEngine3D
  Height = 6
  Length = 8
  Placement = pos=(30,-68,5) rot=(0,0,1;0rad)
  Width = 69
FEATURE [Part::Chamfer] Chamfer150
  Base = -> Box928
  Edges = 1 edges r=1: [Edge6]
FEATURE [Part::Chamfer] Chamfer154
  Base = -> Chamfer150
  Edges = 1 edges r=1: [Edge15]
FEATURE [Part::Chamfer] Chamfer155
  Base = -> Chamfer151
  Edges = 1 edges r=1: [Edge15]
FEATURE [Part::Cylinder] Cylinder2716  label="Válec2686"
  Angle = 360
  AttacherType = Attacher::AttachEngine3D
  Height = 60
  Placement = pos=(24,73,-80) rot=(0,0,1;0rad)
  Radius = 1.5
FEATURE [Part::Cylinder] Cylinder2717  label="Válec2687"
  Angle = 360
  AttacherType = Attacher::AttachEngine3D
  Height = 60
  Placement = pos=(-24,73,-80) rot=(0,0,1;0rad)
  Radius = 1.5
FEATURE [Part::Cylinder] Cylinder2718  label="Válec2688"
  Angle = 360
  AttacherType = Attacher::AttachEngine3D
  Height = 60
  Placement = pos=(-15,125,-80) rot=(0,0,1;0rad)
  Radius = 1.5
FEATURE [Part::Cylinder] Cylinder2719  label="Válec2689"
  Angle = 360
  AttacherType = Attacher::AttachEngine3D
  Height = 60
  Placement = pos=(15,125,-80) rot=(0,0,1;0rad)
  Radius = 1.5
FEATURE [Part::Cut] Cut997
  Base = -> Chamfer155
  Tool = -> Cylinder2714
FEATURE [Part::Cut] Cut998
  Base = -> Chamfer154
  Tool = -> Cylinder2715
FEATURE [Part::Compound] Compound1188
  Links = -> [Cut998,Cut997]
FEATURE [Part::Cut] Cut1020
  Base = -> Compound1207
  Tool = -> Compound1188
FEATURE [Part::Box] Box929  label="Krychle928"
  AttacherType = Attacher::AttachEngine3D
  Height = 9
  Length = 54
  Placement = pos=(-27,60,76) rot=(0,0,1;0rad)
  Width = 68
FEATURE [Part::Box] Box930  label="Krychle929"
  AttacherType = Attacher::AttachEngine3D
  Height = 50
  Length = 42
  Placement = pos=(-21,58,40) rot=(0,0,1;0rad)
  Width = 64
FEATURE [Part::Box] Box931  label="Krychle930"
  AttacherType = Attacher::AttachEngine3D
  Height = 2
  Length = 7
  Placement = pos=(-28,70,-48) rot=(0,0,1;0rad)
  Width = 6
FEATURE [Part::Box] Box932  label="Krychle931"
  AttacherType = Attacher::AttachEngine3D
  Height = 2
  Length = 6
  Placement = pos=(-18,122,-48) rot=(0,0,1;0rad)
  Width = 6
FEATURE [Part::Box] Box933  label="Krychle932"
  AttacherType = Attacher::AttachEngine3D
  Height = 2
  Length = 6
  Placement = pos=(21,70,-48) rot=(0,0,1;0rad)
  Width = 6
FEATURE [Part::Box] Box934  label="Krychle933"
  AttacherType = Attacher::AttachEngine3D
  Height = 2
  Length = 6
  Placement = pos=(12,122,-48) rot=(0,0,1;0rad)
  Width = 6
FEATURE [Part::Cylinder] Cylinder2720  label="Válec2690"
  Angle = 360
  AttacherType = Attacher::AttachEngine3D
  Height = 10
  Placement = pos=(17,-98,44) rot=(1,0,0;1.5708rad)
  Radius = 2
FEATURE [Part::Cylinder] Cylinder2721  label="Válec2691"
  Angle = 360
  AttacherType = Attacher::AttachEngine3D
  Height = 20
  Placement = pos=(0,-54,37) rot=(1,0,0;1.5708rad)
  Radius = 39
FEATURE [Part::Cut] Cut999
  Base = -> Cut1020
  Tool = -> Cylinder2721
FEATURE [Part::Chamfer] Chamfer153
  Base = -> Cut999
  Edges = 2 edges r=6: [Edge18,Edge36]
FEATURE [Part::Cut] Cut1021
  Base = -> Box929
  Placement = pos=(0,0,-9) rot=(0,0,1;0rad)
  Tool = -> Box930
FEATURE [Part::Chamfer] Chamfer152
  Base = -> Cut1021
  Edges = 2 edges r=3: [Edge3,Edge15]
FEATURE [Part::Compound] Compound1208
  Links = -> [Cylinder2716,Cylinder2717,Cylinder2718,Cylinder2719]
  Placement = pos=(0,0,120) rot=(0,0,1;0rad)
FEATURE [Part::Cut] Cut1022
  Base = -> Chamfer152
  Tool = -> Compound1208
FEATURE [Part::Compound] Compound1209
  Links = -> [Box931,Box932,Box933,Box934]
  Placement = pos=(0,0,118) rot=(0,0,1;0rad)
FEATURE [Part::FeaturePython] Tube128  # WARN: FeaturePython — macro-defined, semantics opaque (R4)
  AttacherType = Attacher::AttachEngine3D
  Height = 11.5
  InnerRadius = 34.5
  OuterRadius = 39
  Placement = pos=(17,-92,10) rot=(1,0,0;1.5708rad)
FEATURE [Part::Cut] Cut1019
  Base = -> Tube128
  Tool = -> Torus005
FEATURE [Part::Cut] Cut1018
  Base = -> Cut1019
  Placement = pos=(0,-2,0) rot=(0,0,1;0rad)
  Tool = -> Cylinder2720
FEATURE [Part::FeaturePython] Tube129  # WARN: FeaturePython — macro-defined, semantics opaque (R4)
  AttacherType = Attacher::AttachEngine3D
  Height = 0.5
  InnerRadius = 34.5
  OuterRadius = 39
  Placement = pos=(17,-93.5,10) rot=(1,0,0;1.5708rad)
FEATURE [Part::FeaturePython] Tube130  # WARN: FeaturePython — macro-defined, semantics opaque (R4)
  AttacherType = Attacher::AttachEngine3D
  Height = 1.5
  InnerRadius = 31
  OuterRadius = 39
  Placement = pos=(17,-92,10) rot=(1,0,0;1.5708rad)
FEATURE [Part::Cut] Cut1023
  Base = -> Cut1022
  Placement = pos=(0,2,65) rot=(0,0.707107,-0.707107;3.14159rad)
  Tool = -> Compound1209
FEATURE [Part::Compound] Compound1210
  Links = -> [Tube130,Tube129]
FEATURE [Part::Compound] Compound1211  label="Wrist_outer-halo-ring001"
  Links = -> [Cut1018,Compound1210]
  Placement = pos=(-17,-166,47) rot=(1,0,0;3.14159rad)
FEATURE [Part::Cylinder] Cylinder2722  label="Válec2692"
  Angle = 360
  AttacherType = Attacher::AttachEngine3D
  Height = 3
  Placement = pos=(-34,-61,8) rot=(1,0,0;1.5708rad)
  Radius = 3
FEATURE [Part::Cylinder] Cylinder2723  label="Válec2693"
  Angle = 360
  AttacherType = Attacher::AttachEngine3D
  Height = 3
  Placement = pos=(34,-61,8) rot=(1,0,0;1.5708rad)
  Radius = 3
FEATURE [Part::Cylinder] Cylinder2724  label="Válec2694"
  Angle = 360
  AttacherType = Attacher::AttachEngine3D
  Height = 60
  Placement = pos=(-33,-10,8) rot=(1,0,0;1.5708rad)
  Radius = 1.5
FEATURE [Part::Cylinder] Cylinder2725  label="Válec2695"
  Angle = 360
  AttacherType = Attacher::AttachEngine3D
  Height = 60
  Placement = pos=(33,-10,8) rot=(1,0,0;1.5708rad)
  Radius = 1.5
FEATURE [Part::Compound] Compound1189
  Links = -> [Cylinder2722,Cylinder2723]
  Placement = pos=(0,-10,0) rot=(0,0,1;0rad)
FEATURE [Part::Cut] Cut1000
  Base = -> Chamfer153
  Tool = -> Compound1189
FEATURE [Part::Compound] Compound1190
  Links = -> [Cylinder2724,Cylinder2725]
  Placement = pos=(0,-4,0) rot=(0,0,1;0rad)
FEATURE [Part::Cut] Cut1001
  Base = -> Cut1000
  Tool = -> Compound1190
FEATURE [Part::Box] Box935  label="Krychle934"
  AttacherType = Attacher::AttachEngine3D
  Height = 16
  Length = 12
  Placement = pos=(9,-74,-11) rot=(0,0,1;0rad)
  Width = 9
FEATURE [Part::Box] Box936  label="Krychle935"
  AttacherType = Attacher::AttachEngine3D
  Height = 16
  Length = 12
  Placement = pos=(-21,-74,-11) rot=(0,0,1;0rad)
  Width = 9
FEATURE [Part::Compound] Compound1212
  Links = -> [Box935,Box936]
FEATURE [Part::Cylinder] Cylinder2726  label="Válec2696"
  Angle = 360
  AttacherType = Attacher::AttachEngine3D
  Height = 14
  Placement = pos=(9,-60,-11) rot=(1,0,0;1.5708rad)
  Radius = 12
FEATURE [Part::Cylinder] Cylinder2727  label="Válec2697"
  Angle = 360
  AttacherType = Attacher::AttachEngine3D
  Height = 14
  Placement = pos=(-9,-60,-11) rot=(1,0,0;1.5708rad)
  Radius = 12
FEATURE [Part::Compound] Compound1213
  Links = -> [Cylinder2726,Cylinder2727]
FEATURE [Part::Cut] Cut1024
  Base = -> Compound1212
  Tool = -> Compound1213
FEATURE [Part::Cylinder] Cylinder2728  label="Válec2698"
  Angle = 360
  AttacherType = Attacher::AttachEngine3D
  Height = 20
  Placement = pos=(0,-54,37) rot=(1,0,0;1.5708rad)
  Radius = 39
FEATURE [Part::Cut] Cut1025
  Base = -> Cut1024
  Tool = -> Cylinder2728
FEATURE [Part::Compound] Compound1214  label="Wrist_outer-halo-encoder"
  Links = -> [Cut1025,Cut1001,Compound1211,Cut1023]
  Placement = pos=(0,-4,0) rot=(0,0,1;0rad)
FEATURE [Part::Cylinder] Cylinder2729  label="Válec2699"
  Angle = 360
  AttacherType = Attacher::AttachEngine3D
  Height = 3
  Placement = pos=(15.5,15.5,-54) rot=(0,0,1;0rad)
  Radius = 3
FEATURE [Part::Box] Box937  label="Krychle936"
  AttacherType = Attacher::AttachEngine3D
  Height = 8
  Length = 54
  Placement = pos=(-27,-26,-24) rot=(0,0,1;0rad)
  Width = 52
FEATURE [Part::Box] Box938  label="Krychle937"
  AttacherType = Attacher::AttachEngine3D
  Height = 2
  Length = 8
  Placement = pos=(-24.5,-22.5,-55) rot=(0,0,1;0rad)
  Width = 6
FEATURE [Part::Cylinder] Cylinder2730  label="Válec2700"
  Angle = 360
  AttacherType = Attacher::AttachEngine3D
  Height = 20
  Placement = pos=(21,23,-28) rot=(0,0,1;0rad)
  Radius = 1.5
FEATURE [Part::Cylinder] Cylinder2731  label="Válec2701"
  Angle = 360
  AttacherType = Attacher::AttachEngine3D
  Height = 3
  Placement = pos=(-15.5,15.5,-54) rot=(0,0,1;0rad)
  Radius = 3
FEATURE [Part::Cylinder] Cylinder2732  label="Válec2702"
  Angle = 360
  AttacherType = Attacher::AttachEngine3D
  Height = 3
  Placement = pos=(-15.5,-15.5,-54) rot=(0,0,1;0rad)
  Radius = 3
FEATURE [Part::Cylinder] Cylinder2733  label="Válec2703"
  Angle = 360
  AttacherType = Attacher::AttachEngine3D
  Height = 20
  Placement = pos=(15.5,-15.5,-68) rot=(0,0,1;0rad)
  Radius = 1.5
FEATURE [Part::Cylinder] Cylinder2734  label="Válec2704"
  Angle = 360
  AttacherType = Attacher::AttachEngine3D
  Height = 20
  Placement = pos=(10.48,15.75,-50) rot=(0,0,1;0rad)
  Radius = 1.5
FEATURE [Part::Cylinder] Cylinder2735  label="Válec2705"
  Angle = 360
  AttacherType = Attacher::AttachEngine3D
  Height = 20
  Placement = pos=(15.5,15.5,-68) rot=(0,0,1;0rad)
  Radius = 1.5
FEATURE [Part::Cylinder] Cylinder2736  label="Válec2706"
  Angle = 360
  AttacherType = Attacher::AttachEngine3D
  Height = 3
  Placement = pos=(15.5,-15.5,-54) rot=(0,0,1;0rad)
  Radius = 3
FEATURE [Part::Cylinder] Cylinder2737  label="Válec2707"
  Angle = 360
  AttacherType = Attacher::AttachEngine3D
  Height = 20
  Placement = pos=(-10.48,15.75,-50) rot=(0,0,1;0rad)
  Radius = 1.5
FEATURE [Part::Box] Box939  label="Krychle938"
  AttacherType = Attacher::AttachEngine3D
  Height = 2
  Length = 8
  Placement = pos=(16.5,-22.5,-55) rot=(0,0,1;0rad)
  Width = 6
FEATURE [Part::Cylinder] Cylinder2738  label="Válec2708"
  Angle = 360
  AttacherType = Attacher::AttachEngine3D
  Height = 20
  Placement = pos=(-21,23,-28) rot=(0,0,1;0rad)
  Radius = 1.5
FEATURE [Part::Box] Box940  label="Krychle939"
  AttacherType = Attacher::AttachEngine3D
  Height = 2
  Length = 8
  Placement = pos=(16.5,16.5,-55) rot=(0,0,1;0rad)
  Width = 6
FEATURE [Part::Box] Box941  label="Krychle940"
  AttacherType = Attacher::AttachEngine3D
  Height = 2
  Length = 8
  Placement = pos=(-24.5,16.5,-55) rot=(0,0,1;0rad)
  Width = 6
FEATURE [Part::Cylinder] Cylinder2739  label="Válec2709"
  Angle = 360
  AttacherType = Attacher::AttachEngine3D
  Height = 20
  Placement = pos=(-15.5,-15.5,-68) rot=(0,0,1;0rad)
  Radius = 1.5
FEATURE [Part::Cylinder] Cylinder2740  label="Válec2710"
  Angle = 360
  AttacherType = Attacher::AttachEngine3D
  Height = 20
  Placement = pos=(21,-23,-28) rot=(0,0,1;0rad)
  Radius = 1.5
FEATURE [Part::Cylinder] Cylinder2741  label="Válec2711"
  Angle = 360
  AttacherType = Attacher::AttachEngine3D
  Height = 20
  Placement = pos=(-15.5,15.5,-68) rot=(0,0,1;0rad)
  Radius = 1.5
FEATURE [Part::Cylinder] Cylinder2742  label="Válec2712"
  Angle = 360
  AttacherType = Attacher::AttachEngine3D
  Height = 50
  Placement = pos=(0,0,-29) rot=(0,0,1;0rad)
  Radius = 8
FEATURE [Part::Cylinder] Cylinder2743  label="Válec2713"
  Angle = 360
  AttacherType = Attacher::AttachEngine3D
  Height = 20
  Placement = pos=(-21,-23,-28) rot=(0,0,1;0rad)
  Radius = 1.5
FEATURE [Part::Box] Box942  label="Krychle941"
  AttacherType = Attacher::AttachEngine3D
  Height = 2
  Length = 6
  Placement = pos=(25,19,-55) rot=(0,0,1;0rad)
  Width = 8
FEATURE [Part::Box] Box943  label="Krychle942"
  AttacherType = Attacher::AttachEngine3D
  Height = 2
  Length = 6
  Placement = pos=(-17,-25,-55) rot=(0,0,1;0rad)
  Width = 8
FEATURE [Part::Box] Box944  label="Krychle943"
  AttacherType = Attacher::AttachEngine3D
  Height = 2
  Length = 6
  Placement = pos=(-17,19,-55) rot=(0,0,1;0rad)
  Width = 8
FEATURE [Part::Box] Box945  label="Krychle944"
  AttacherType = Attacher::AttachEngine3D
  Height = 2
  Length = 6
  Placement = pos=(25,-25,-55) rot=(0,0,1;0rad)
  Width = 8
FEATURE [Part::Cylinder] Cylinder2744  label="Válec2714"
  Angle = 360
  AttacherType = Attacher::AttachEngine3D
  Height = 20
  Placement = pos=(39.5,-17,10) rot=(1,0,0;1.5708rad)
  Radius = 2.65
FEATURE [Part::Cylinder] Cylinder2745  label="Válec2715"
  Angle = 360
  AttacherType = Attacher::AttachEngine3D
  Height = 20
  Placement = pos=(-5.5,-17,10) rot=(1,0,0;1.5708rad)
  Radius = 2.65
FEATURE [Part::Box] Box946  label="Krychle945"
  AttacherType = Attacher::AttachEngine3D
  Height = 32
  Length = 5.85
  Placement = pos=(-10,-138,-6) rot=(0,0,1;0rad)
  Width = 60
FEATURE [Part::Box] Box947  label="Krychle946"
  AttacherType = Attacher::AttachEngine3D
  Height = 32
  Length = 5.85
  Placement = pos=(38.15,-138,-6) rot=(0,0,1;0rad)
  Width = 60
FEATURE [Part::Cylinder] Cylinder2746  label="Válec2716"
  Angle = 360
  AttacherType = Attacher::AttachEngine3D
  Height = 16
  Placement = pos=(18,-9,64) rot=(0,1,0;1.5708rad)
  Radius = 1.5
FEATURE [Part::Cylinder] Cylinder2747  label="Válec2717"
  Angle = 360
  AttacherType = Attacher::AttachEngine3D
  Height = 16
  Placement = pos=(18,9,64) rot=(0,1,0;1.5708rad)
  Radius = 1.5
FEATURE [Part::Cylinder] Cylinder2748  label="Válec2718"
  Angle = 360
  AttacherType = Attacher::AttachEngine3D
  Height = 16
  Placement = pos=(-28,9,64) rot=(0,1,0;1.5708rad)
  Radius = 1.5
FEATURE [Part::Cylinder] Cylinder2749  label="Válec2719"
  Angle = 360
  AttacherType = Attacher::AttachEngine3D
  Height = 16
  Placement = pos=(-28,-9,64) rot=(0,1,0;1.5708rad)
  Radius = 1.5
FEATURE [Part::Cylinder] Cylinder2750  label="Válec2720"
  Angle = 360
  AttacherType = Attacher::AttachEngine3D
  Height = 20
  Placement = pos=(32,-108,18) rot=(0,1,0;1.5708rad)
  Radius = 1
FEATURE [Part::Cylinder] Cylinder2751  label="Válec2721"
  Angle = 360
  AttacherType = Attacher::AttachEngine3D
  Height = 20
  Placement = pos=(-17,-108,18) rot=(0,1,0;1.5708rad)
  Radius = 1
FEATURE [Part::Cylinder] Cylinder2752  label="Válec2722"
  Angle = 360
  AttacherType = Attacher::AttachEngine3D
  Height = 20
  Placement = pos=(32,-108,2) rot=(0,1,0;1.5708rad)
  Radius = 1
FEATURE [Part::Cylinder] Cylinder2753  label="Válec2723"
  Angle = 360
  AttacherType = Attacher::AttachEngine3D
  Height = 20
  Placement = pos=(-17,-108,2) rot=(0,1,0;1.5708rad)
  Radius = 1
FEATURE [Part::Box] Box948  label="Krychle947"
  AttacherType = Attacher::AttachEngine3D
  Height = 4
  Length = 4
  Placement = pos=(-7,-113,16) rot=(0,0,1;0rad)
  Width = 4
FEATURE [Part::Box] Box949  label="Krychle948"
  AttacherType = Attacher::AttachEngine3D
  Height = 4
  Length = 4
  Placement = pos=(-7,-113,0) rot=(0,0,1;0rad)
  Width = 4
FEATURE [Part::Box] Box950  label="Krychle949"
  AttacherType = Attacher::AttachEngine3D
  Height = 4
  Length = 4
  Placement = pos=(37,-113,16) rot=(0,0,1;0rad)
  Width = 4
FEATURE [Part::Box] Box951  label="Krychle950"
  AttacherType = Attacher::AttachEngine3D
  Height = 4
  Length = 4
  Placement = pos=(37,-113,0) rot=(0,0,1;0rad)
  Width = 4
FEATURE [Part::Cylinder] Cylinder2754  label="Válec2724"
  Angle = 360
  AttacherType = Attacher::AttachEngine3D
  Height = 3
  Placement = pos=(10,-35,10) rot=(0,0,1;0rad)
  Radius = 3
FEATURE [Part::Cylinder] Cylinder2232  label="Válec2232"
  Angle = 360
  AttacherType = Attacher::AttachEngine3D
  Height = 3
  Placement = pos=(-8,-35,10) rot=(0,0,1;0rad)
  Radius = 3
FEATURE [Part::Cylinder] Cylinder2233  label="Válec2233"
  Angle = 360
  AttacherType = Attacher::AttachEngine3D
  Height = 3
  Placement = pos=(10,-35,10) rot=(0,0,1;0rad)
  Radius = 3
FEATURE [Part::Cylinder] Cylinder2234  label="Válec2234"
  Angle = 360
  AttacherType = Attacher::AttachEngine3D
  Height = 3
  Placement = pos=(-8,-35,10) rot=(0,0,1;0rad)
  Radius = 3
FEATURE [Part::Cut] Cut1030
  Base = -> Box937
  Tool = -> Cylinder2742
FEATURE [Part::Compound] Compound1215
  Links = -> [Box940,Box941,Box939,Box938]
  Placement = pos=(0,0,10) rot=(0,0,1;0rad)
FEATURE [Part::Compound] Compound1216
  Links = -> [Cylinder2737,Cylinder2734]
  Placement = pos=(0,0,-10) rot=(0,0,1;0rad)
FEATURE [Part::Compound] Compound1217
  Links = -> [Cylinder2732,Cylinder2736,Cylinder2731,Cylinder2729]
FEATURE [Part::Compound] Compound1219
  Links = -> [Cylinder2743,Cylinder2730,Cylinder2738,Cylinder2740]
FEATURE [Part::Cut] Cut1031
  Base = -> Cut1030
  Tool = -> Compound1219
FEATURE [Part::Compound] Compound1218
  Links = -> [Cut1031]
  Placement = pos=(0,0,-30) rot=(0,0,1;0rad)
FEATURE [Part::Cut] Cut1032
  Base = -> Compound1218
  Tool = -> Compound1215
FEATURE [Part::Cut] Cut1036
  Base = -> Cut1032
  Tool = -> Compound1216
FEATURE [Part::Compound] Compound1220
  Links = -> [Cylinder2735,Cylinder2741,Cylinder2733,Cylinder2739]
  Placement = pos=(0,0,4) rot=(0,0,1;0rad)
FEATURE [Part::Cut] Cut1035
  Base = -> Cut1036
  Tool = -> Compound1220
FEATURE [Part::Cut] Cut1026
  Base = -> Cut1035
  Placement = pos=(17,-127,10) rot=(1,0,0;1.5708rad)
  Tool = -> Compound1217
FEATURE [Part::Compound] Compound1221
  Links = -> [Box942,Box944,Box945,Box943]
  Placement = pos=(10,-24,11) rot=(-1,0,0;1.5708rad)
FEATURE [Part::Cut] Cut1027
  Base = -> Cut1026
  Tool = -> Compound1221
FEATURE [Part::Compound] Compound1222
  Links = -> [Cylinder2745,Cylinder2744]
  Placement = pos=(0,-40,0) rot=(0,0,1;0rad)
FEATURE [Part::Chamfer] Chamfer156
  Base = -> Cut1027
  Edges = 1 edges r=3: [Edge17]
FEATURE [Part::Chamfer] Chamfer157
  Base = -> Chamfer156
  Edges = 1 edges r=3: [Edge33]
FEATURE [Part::Cut] Cut1028
  Base = -> Chamfer157
  Tool = -> Compound1222
FEATURE [Part::Compound] Compound1223
  Links = -> [Cylinder2748,Cylinder2749,Cylinder2747,Cylinder2746]
  Placement = pos=(14,-71,10) rot=(1,0,0;1.5708rad)
FEATURE [Part::Compound] Compound1224
  Links = -> [Box946,Box947]
FEATURE [Part::Cut] Cut1029
  Base = -> Compound1224
  Tool = -> Compound1223
FEATURE [Part::Compound] Compound1225
  Links = -> [Cylinder2752,Cylinder2750]
  Placement = pos=(0,-3,0) rot=(0,0,1;0rad)
FEATURE [Part::Compound] Compound1226
  Links = -> [Cylinder2753,Cylinder2751]
  Placement = pos=(0,-3,0) rot=(0,0,1;0rad)
FEATURE [Part::Compound] Compound1227
  Links = -> [Compound1225,Compound1226]
  Placement = pos=(0,-1.5,0) rot=(0,0,1;0rad)
FEATURE [Part::Chamfer] Chamfer158
  Base = -> Cut1029
  Edges = 2 edges r=2: [Edge29,Edge31]
FEATURE [Part::Chamfer] Chamfer159
  Base = -> Chamfer158
  Edges = 2 edges r=2: [Edge26,Edge28]
FEATURE [Part::Cut] Cut1033
  Base = -> Chamfer159
  Tool = -> Compound1227
FEATURE [Part::Compound] Compound1228
  Links = -> [Box948,Box949,Box950,Box951]
  Placement = pos=(0,-1.5,0) rot=(0,0,1;0rad)
FEATURE [Part::Cut] Cut1034
  Base = -> Cut1033
  Tool = -> Compound1228
FEATURE [Part::Compound] Compound1229  label="Wrist_moto-hold1"
  Links = -> [Cut1034,Cut1028]
  Placement = pos=(-9,-170,20) rot=(0.707107,0,0.707107;3.14159rad)
FEATURE [Part::Compound] Compound1230
  Links = -> [Cylinder2233,Cylinder2234]
  Placement = pos=(0,0,51) rot=(0,0,1;0rad)
FEATURE [Part::Compound] Compound1231
  Links = -> [Cylinder2754,Cylinder2232]
FEATURE [Part::Compound] Compound1232
  Links = -> [Compound1231,Compound1230]
FEATURE [Part::Cut] Cut1037  label="Wrist_moto-hold-oldo"
  Base = -> Compound1229
  Placement = pos=(-1,0,0) rot=(0,0,1;0rad)
  Tool = -> Compound1232
FEATURE [Part::Torus] Torus006  label="Anuloid006"
  Angle1 = -180
  Angle2 = 180
  Angle3 = 360
  AttacherType = Attacher::AttachEngine3D
  Placement = pos=(0,0,17.5) rot=(0,0,1;0rad)
  Radius1 = 20
  Radius2 = 2.2
FEATURE [Part::Cylinder] Cylinder2755  label="Válec2725"
  Angle = 360
  AttacherType = Attacher::AttachEngine3D
  Height = 10
  Placement = pos=(20,0,17.5) rot=(0,0,1;0rad)
  Radius = 2.2
FEATURE [Part::Cylinder] Cylinder2756  label="Válec2726"
  Angle = 360
  AttacherType = Attacher::AttachEngine3D
  Height = 20
  Placement = pos=(0,23,8) rot=(0,0,1;0rad)
  Radius = 1
FEATURE [Part::Cylinder] Cylinder2757  label="Válec2727"
  Angle = 360
  AttacherType = Attacher::AttachEngine3D
  Height = 20
  Placement = pos=(-16.26,16.26,8) rot=(0,0,1;0.785398rad)
  Radius = 1
FEATURE [Part::Cylinder] Cylinder2758  label="Válec2728"
  Angle = 360
  AttacherType = Attacher::AttachEngine3D
  Height = 20
  Placement = pos=(-23,0,8) rot=(0,0,1;1.5708rad)
  Radius = 1
FEATURE [Part::Cylinder] Cylinder2759  label="Válec2729"
  Angle = 360
  AttacherType = Attacher::AttachEngine3D
  Height = 20
  Placement = pos=(-16.26,-16.26,8) rot=(0,0,1;2.35619rad)
  Radius = 1
FEATURE [Part::Cylinder] Cylinder2760  label="Válec2730"
  Angle = 360
  AttacherType = Attacher::AttachEngine3D
  Height = 20
  Placement = pos=(4e-15,-23,8) rot=(0,0,1;3.14159rad)
  Radius = 1
FEATURE [Part::Cylinder] Cylinder2761  label="Válec2731"
  Angle = 360
  AttacherType = Attacher::AttachEngine3D
  Height = 20
  Placement = pos=(16.26,-16.26,8) rot=(0,0,1;3.92699rad)
  Radius = 1
FEATURE [Part::Cylinder] Cylinder2762  label="Válec2732"
  Angle = 360
  AttacherType = Attacher::AttachEngine3D
  Height = 20
  Placement = pos=(23,1.1e-14,8) rot=(0,0,-1;1.5708rad)
  Radius = 1
FEATURE [Part::Cylinder] Cylinder2763  label="Válec2733"
  Angle = 360
  AttacherType = Attacher::AttachEngine3D
  Height = 20
  Placement = pos=(16.26,16.26,8) rot=(0,0,-1;0.785398rad)
  Radius = 1
FEATURE [Part::Compound] Compound1233
  Links = -> [Cylinder2756,Cylinder2763,Cylinder2762,Cylinder2760,Cylinder2761,Cylinder2759,Cylinder2757,Cylinder2758]
  Placement = pos=(0,0,-12) rot=(0,0,1;0rad)
FEATURE [Part::Box] Box952  label="Krychle951"
  AttacherType = Attacher::AttachEngine3D
  Height = 1.4
  Length = 4
  Placement = pos=(-2,21,14) rot=(0,0,1;0rad)
  Width = 4
FEATURE [Part::Box] Box953  label="Krychle952"
  AttacherType = Attacher::AttachEngine3D
  Height = 1.4
  Length = 4
  Placement = pos=(-16.2635,13.435,14) rot=(0,0,1;0.785398rad)
  Width = 4
FEATURE [Part::Box] Box954  label="Krychle953"
  AttacherType = Attacher::AttachEngine3D
  Height = 1.4
  Length = 4
  Placement = pos=(-21,-2,14) rot=(0,0,1;1.5708rad)
  Width = 4
FEATURE [Part::Box] Box955  label="Krychle954"
  AttacherType = Attacher::AttachEngine3D
  Height = 1.4
  Length = 4
  Placement = pos=(-13.435,-16.2635,14) rot=(0,0,1;2.35619rad)
  Width = 4
FEATURE [Part::Box] Box956  label="Krychle955"
  AttacherType = Attacher::AttachEngine3D
  Height = 1.4
  Length = 4
  Placement = pos=(2,-21,14) rot=(0,0,1;3.14159rad)
  Width = 4
FEATURE [Part::Box] Box957  label="Krychle956"
  AttacherType = Attacher::AttachEngine3D
  Height = 1.4
  Length = 4
  Placement = pos=(16.2635,-13.435,14) rot=(0,0,1;3.92699rad)
  Width = 4
FEATURE [Part::FeaturePython] Tube134  # WARN: FeaturePython — macro-defined, semantics opaque (R4)
  AttacherType = Attacher::AttachEngine3D
  Height = 14
  InnerRadius = 21
  OuterRadius = 25
  Placement = pos=(0,0,10) rot=(0,0,1;0rad)
FEATURE [Part::Cut] Cut1040
  Base = -> Tube134
  Tool = -> Torus006
FEATURE [Part::Box] Box958  label="Krychle957"
  AttacherType = Attacher::AttachEngine3D
  Height = 1.4
  Length = 4
  Placement = pos=(21,2,14) rot=(0,0,-1;1.5708rad)
  Width = 4
FEATURE [Part::Box] Box959  label="Krychle958"
  AttacherType = Attacher::AttachEngine3D
  Height = 1.4
  Length = 4
  Placement = pos=(13.435,16.2635,14) rot=(0,0,-1;0.785398rad)
  Width = 4
FEATURE [Part::Compound] Compound1234
  Links = -> [Box952,Box953,Box954,Box955,Box956,Box957,Box958,Box959]
  Placement = pos=(0,0,-1) rot=(0,0,1;0rad)
FEATURE [Part::Cut] Cut1039
  Base = -> Cut1040
  Tool = -> Compound1234
FEATURE [Part::Cut] Cut1038
  Base = -> Cut1039
  Tool = -> Compound1233
FEATURE [Part::Cut] Cut1041
  Base = -> Cut1038
  Tool = -> Cylinder2755
FEATURE [Part::Cylinder] Cylinder2764  label="Válec2734"
  Angle = 360
  AttacherType = Attacher::AttachEngine3D
  Height = 10
  Radius = 21
FEATURE [Part::Cylinder] Cylinder2765  label="Válec2735"
  Angle = 360
  AttacherType = Attacher::AttachEngine3D
  Height = 10
  Radius = 21
FEATURE [Part::Box] Box960  label="Krychle959"
  AttacherType = Attacher::AttachEngine3D
  Height = 1.4
  Length = 4
  Placement = pos=(-2,17,-13) rot=(0,0,1;0rad)
  Width = 4
FEATURE [Part::Box] Box961  label="Krychle960"
  AttacherType = Attacher::AttachEngine3D
  Height = 1.4
  Length = 4
  Placement = pos=(-13.435,10.6066,-13) rot=(0,0,1;0.785398rad)
  Width = 4
FEATURE [Part::Box] Box962  label="Krychle961"
  AttacherType = Attacher::AttachEngine3D
  Height = 1.4
  Length = 4
  Placement = pos=(-10.6066,-13.435,-13) rot=(0,0,1;2.35619rad)
  Width = 4
FEATURE [Part::Box] Box963  label="Krychle962"
  AttacherType = Attacher::AttachEngine3D
  Height = 1.4
  Length = 4
  Placement = pos=(2,-17,-13) rot=(0,0,1;3.14159rad)
  Width = 4
FEATURE [Part::Cylinder] Cylinder2766  label="Válec2736"
  Angle = 360
  AttacherType = Attacher::AttachEngine3D
  Height = 10
  Placement = pos=(0,19,-20) rot=(0,0,1;0rad)
  Radius = 1
FEATURE [Part::Box] Box964  label="Krychle963"
  AttacherType = Attacher::AttachEngine3D
  Height = 1.4
  Length = 4
  Placement = pos=(-17,-2,-13) rot=(0,0,1;1.5708rad)
  Width = 4
FEATURE [Part::Box] Box965  label="Krychle964"
  AttacherType = Attacher::AttachEngine3D
  Height = 1.4
  Length = 4
  Placement = pos=(13.435,-10.6066,-13) rot=(0,0,1;3.92699rad)
  Width = 4
FEATURE [Part::Box] Box966  label="Krychle965"
  AttacherType = Attacher::AttachEngine3D
  Height = 1.4
  Length = 4
  Placement = pos=(10.6066,13.435,-13) rot=(0,0,-1;0.785398rad)
  Width = 4
FEATURE [Part::Cylinder] Cylinder2767  label="Válec2737"
  Angle = 360
  AttacherType = Attacher::AttachEngine3D
  Height = 10
  Placement = pos=(-13.435,13.435,-20) rot=(0,0,1;0.785398rad)
  Radius = 1
FEATURE [Part::Cylinder] Cylinder2768  label="Válec2738"
  Angle = 360
  AttacherType = Attacher::AttachEngine3D
  Height = 10
  Placement = pos=(-19,-1e-15,-20) rot=(0,0,1;1.5708rad)
  Radius = 1
FEATURE [Part::Cylinder] Cylinder2769  label="Válec2739"
  Angle = 360
  AttacherType = Attacher::AttachEngine3D
  Height = 10
  Placement = pos=(-13.435,-13.435,-20) rot=(0,0,1;2.35619rad)
  Radius = 1
FEATURE [Part::Cylinder] Cylinder2770  label="Válec2740"
  Angle = 360
  AttacherType = Attacher::AttachEngine3D
  Height = 10
  Placement = pos=(6e-15,-19,-20) rot=(0,0,1;3.14159rad)
  Radius = 1
FEATURE [Part::FeaturePython] wormgear045  # WARN: FeaturePython — macro-defined, semantics opaque (R4)
  AttacherType = Attacher::AttachEngine3D
  Placement = pos=(0,0,0) rot=(0,0,1;1.13446rad)
  beta = 42.7094
  clearance = 0.25
  diameter = 32.5
  head = 0
  height = 12
  module = 1
  pressure_angle = 20
  reverse_pitch = true
  teeth = 30
  version = 0.0.3
FEATURE [Part::Cut] Cut1042
  Base = -> Cylinder2764
  Tool = -> wormgear045
FEATURE [Part::FeaturePython] wormgear046  # WARN: FeaturePython — macro-defined, semantics opaque (R4)
  AttacherType = Attacher::AttachEngine3D
  Placement = pos=(0,0,0) rot=(0,0,1;1.09607rad)
  beta = 42.7094
  clearance = 0.25
  diameter = 32.5
  head = 0
  height = 12
  module = 1
  pressure_angle = 20
  reverse_pitch = false
  teeth = 30
  version = 0.0.3
FEATURE [Part::Cut] Cut1043
  Base = -> Cylinder2765
  Placement = pos=(0,0,-10) rot=(0,0,1;0rad)
  Tool = -> wormgear046
FEATURE [Part::Compound] Compound1235  label="gearovina-mini_okruh004"
  Links = -> [Cut1043,Cut1042]
FEATURE [Part::FeaturePython] Tube135  # WARN: FeaturePython — macro-defined, semantics opaque (R4)
  AttacherType = Attacher::AttachEngine3D
  Height = 6
  InnerRadius = 17
  OuterRadius = 21
  Placement = pos=(0,0,-16) rot=(0,0,1;0rad)
FEATURE [Part::FeaturePython] Tube136  # WARN: FeaturePython — macro-defined, semantics opaque (R4)
  AttacherType = Attacher::AttachEngine3D
  Height = 6
  InnerRadius = 20
  OuterRadius = 25
  Placement = pos=(0,0,4) rot=(0,0,1;0rad)
FEATURE [Part::Cylinder] Cylinder2771  label="Válec2741"
  Angle = 360
  AttacherType = Attacher::AttachEngine3D
  Height = 10
  Placement = pos=(13.435,-13.435,-20) rot=(0,0,1;3.92699rad)
  Radius = 1
FEATURE [Part::Box] Box967  label="Krychle966"
  AttacherType = Attacher::AttachEngine3D
  Height = 1.4
  Length = 4
  Placement = pos=(17,2,-13) rot=(0,0,-1;1.5708rad)
  Width = 4
FEATURE [Part::Compound] Compound1236
  Links = -> [Box960,Box961,Box964,Box962,Box963,Box965,Box967,Box966]
FEATURE [Part::Cut] Cut1044
  Base = -> Tube135
  Tool = -> Compound1236
FEATURE [Part::Cylinder] Cylinder2772  label="Válec2742"
  Angle = 360
  AttacherType = Attacher::AttachEngine3D
  Height = 10
  Placement = pos=(19,8e-15,-20) rot=(0,0,-1;1.5708rad)
  Radius = 1
FEATURE [Part::Cylinder] Cylinder2773  label="Válec2743"
  Angle = 360
  AttacherType = Attacher::AttachEngine3D
  Height = 10
  Placement = pos=(13.435,13.435,-20) rot=(0,0,-1;0.785398rad)
  Radius = 1
FEATURE [Part::Compound] Compound1237
  Links = -> [Cylinder2766,Cylinder2767,Cylinder2768,Cylinder2769,Cylinder2770,Cylinder2771,Cylinder2772,Cylinder2773]
FEATURE [Part::Cut] Cut1045
  Base = -> Cut1044
  Tool = -> Compound1237
FEATURE [Part::Cylinder] Cylinder2774  label="Válec2744"
  Angle = 360
  AttacherType = Attacher::AttachEngine3D
  Height = 10
  Placement = pos=(0,23,4) rot=(0,0,1;0rad)
  Radius = 1
FEATURE [Part::Cylinder] Cylinder2775  label="Válec2745"
  Angle = 360
  AttacherType = Attacher::AttachEngine3D
  Height = 10
  Placement = pos=(16.2635,16.2635,4) rot=(0,0,-1;0.785398rad)
  Radius = 1
FEATURE [Part::Cylinder] Cylinder2776  label="Válec2746"
  Angle = 360
  AttacherType = Attacher::AttachEngine3D
  Height = 10
  Placement = pos=(16.2635,-16.2635,4) rot=(0,0,1;3.92699rad)
  Radius = 1
FEATURE [Part::Cylinder] Cylinder2777  label="Válec2747"
  Angle = 360
  AttacherType = Attacher::AttachEngine3D
  Height = 10
  Placement = pos=(-16.2635,16.2635,4) rot=(0,0,1;0.785398rad)
  Radius = 1
FEATURE [Part::Cylinder] Cylinder2778  label="Válec2748"
  Angle = 360
  AttacherType = Attacher::AttachEngine3D
  Height = 2
  Placement = pos=(-16.2635,-16.2635,4) rot=(0,0,1;2.35619rad)
  Radius = 2
FEATURE [Part::Cylinder] Cylinder2779  label="Válec2749"
  Angle = 360
  AttacherType = Attacher::AttachEngine3D
  Height = 10
  Placement = pos=(-23,-1e-15,4) rot=(0,0,1;1.5708rad)
  Radius = 1
FEATURE [Part::Cylinder] Cylinder2780  label="Válec2750"
  Angle = 360
  AttacherType = Attacher::AttachEngine3D
  Height = 10
  Placement = pos=(-16.2635,-16.2635,4) rot=(0,0,1;2.35619rad)
  Radius = 1
FEATURE [Part::Cylinder] Cylinder2781  label="Válec2751"
  Angle = 360
  AttacherType = Attacher::AttachEngine3D
  Height = 2
  Placement = pos=(0,23,4) rot=(0,0,1;0rad)
  Radius = 2
FEATURE [Part::Cylinder] Cylinder2782  label="Válec2752"
  Angle = 360
  AttacherType = Attacher::AttachEngine3D
  Height = 10
  Placement = pos=(23,1.1e-14,4) rot=(0,0,-1;1.5708rad)
  Radius = 1
FEATURE [Part::Cylinder] Cylinder2783  label="Válec2753"
  Angle = 360
  AttacherType = Attacher::AttachEngine3D
  Height = 2
  Placement = pos=(-23,-1e-15,4) rot=(0,0,1;1.5708rad)
  Radius = 2
FEATURE [Part::Cylinder] Cylinder2784  label="Válec2754"
  Angle = 360
  AttacherType = Attacher::AttachEngine3D
  Height = 10
  Placement = pos=(4e-15,-23,4) rot=(0,0,1;3.14159rad)
  Radius = 1
FEATURE [Part::Compound] Compound1238
  Links = -> [Cylinder2774,Cylinder2777,Cylinder2779,Cylinder2780,Cylinder2784,Cylinder2776,Cylinder2782,Cylinder2775]
FEATURE [Part::Cylinder] Cylinder2785  label="Válec2755"
  Angle = 360
  AttacherType = Attacher::AttachEngine3D
  Height = 2
  Placement = pos=(16.2635,-16.2635,4) rot=(0,0,1;3.92699rad)
  Radius = 2
FEATURE [Part::Cylinder] Cylinder2786  label="Válec2756"
  Angle = 360
  AttacherType = Attacher::AttachEngine3D
  Height = 2
  Placement = pos=(23,1.1e-14,4) rot=(0,0,-1;1.5708rad)
  Radius = 2
FEATURE [Part::Cylinder] Cylinder2787  label="Válec2757"
  Angle = 360
  AttacherType = Attacher::AttachEngine3D
  Height = 2
  Placement = pos=(16.2635,16.2635,4) rot=(0,0,-1;0.785398rad)
  Radius = 2
FEATURE [Part::Cylinder] Cylinder2788  label="Válec2758"
  Angle = 360
  AttacherType = Attacher::AttachEngine3D
  Height = 2
  Placement = pos=(-16.2635,16.2635,4) rot=(0,0,1;0.785398rad)
  Radius = 2
FEATURE [Part::Cylinder] Cylinder2789  label="Válec2759"
  Angle = 360
  AttacherType = Attacher::AttachEngine3D
  Height = 2
  Placement = pos=(4e-15,-23,4) rot=(0,0,1;3.14159rad)
  Radius = 2
FEATURE [Part::Compound] Compound1239
  Links = -> [Cylinder2781,Cylinder2788,Cylinder2783,Cylinder2778,Cylinder2789,Cylinder2785,Cylinder2786,Cylinder2787]
FEATURE [Part::Cut] Cut1047
  Base = -> Tube136
  Tool = -> Compound1239
FEATURE [Part::Cut] Cut1046
  Base = -> Cut1047
  Tool = -> Compound1238
FEATURE [Part::Compound] Compound1240
  Links = -> [Cut1045,Compound1235,Cut1046]
FEATURE [Part::Compound] Compound1241
  Links = -> [Compound1240,Cut1041]
  Placement = pos=(0,1,37) rot=(1,0,0;1.5708rad)
FEATURE [Part::Cylinder] Cylinder2551  label="Válec2521"
  Angle = 360
  AttacherType = Attacher::AttachEngine3D
  Height = 4
  Placement = pos=(-18,-106.5,2) rot=(0,1,0;1.5708rad)
  Radius = 2
FEATURE [Part::Cylinder] Cylinder2552  label="Válec2522"
  Angle = 360
  AttacherType = Attacher::AttachEngine3D
  Height = 4
  Placement = pos=(-18,-106.5,18) rot=(0,1,0;1.5708rad)
  Radius = 2
FEATURE [Part::Cylinder] Cylinder2553  label="Válec2523"
  Angle = 360
  AttacherType = Attacher::AttachEngine3D
  Height = 4
  Placement = pos=(50,-106.5,18) rot=(0,1,0;1.5708rad)
  Radius = 2
FEATURE [Part::Cylinder] Cylinder2554  label="Válec2524"
  Angle = 360
  AttacherType = Attacher::AttachEngine3D
  Height = 4
  Placement = pos=(50,-106.5,2) rot=(0,1,0;1.5708rad)
  Radius = 2
FEATURE [Part::Compound] Compound1130
  Links = -> [Cylinder2551,Cylinder2552,Cylinder2553,Cylinder2554]
  Placement = pos=(-18,10,105) rot=(1,0,0;1.5708rad)
FEATURE [Part::FeaturePython] Tube098  # WARN: FeaturePython — macro-defined, semantics opaque (R4)
  AttacherType = Attacher::AttachEngine3D
  Height = 7
  InnerRadius = 31
  OuterRadius = 36
  Placement = pos=(0,0,3) rot=(0,0,1;0rad)
FEATURE [Part::FeaturePython] Tube099  # WARN: FeaturePython — macro-defined, semantics opaque (R4)
  AttacherType = Attacher::AttachEngine3D
  Height = 7
  InnerRadius = 32
  OuterRadius = 33.4
  Placement = pos=(0,0,-22) rot=(0,0,1;0rad)
FEATURE [Part::FeaturePython] Tube100  # WARN: FeaturePython — macro-defined, semantics opaque (R4)
  AttacherType = Attacher::AttachEngine3D
  Height = 7
  InnerRadius = 32
  OuterRadius = 33.4
  Placement = pos=(0,0,-22) rot=(0,0,1;0rad)
FEATURE [Part::Cylinder] Cylinder2558  label="Válec2528"
  Angle = 360
  AttacherType = Attacher::AttachEngine3D
  Height = 7
  Placement = pos=(0,0,-22) rot=(0,0,1;0rad)
  Radius = 32
FEATURE [Part::Box] Box867  label="Krychle866"
  AttacherType = Attacher::AttachEngine3D
  Height = 7
  Length = 1.4
  Placement = pos=(0,0,-22) rot=(0,0,-1;0.05236rad)
  Width = 60
FEATURE [Part::Box] Box968  label="Krychle967"
  AttacherType = Attacher::AttachEngine3D
  Height = 7
  Length = 1.4
  Placement = pos=(0,0,-22) rot=(0,0,1;0.099484rad)
  Width = 60
FEATURE [Part::Compound] Compound1135
  Links = -> [Box867,Box968]
FEATURE [Part::Cut] Cut957
  Base = -> Compound1135
  Placement = pos=(0,0,25) rot=(0,0,1;0rad)
  Tool = -> Cylinder2558
FEATURE [Part::Cut] Cut961
  Base = -> Tube098
  Tool = -> Cut957
FEATURE [Part::Box] Box969  label="Krychle968"
  AttacherType = Attacher::AttachEngine3D
  Height = 7
  Length = 60
  Placement = pos=(0,0,-22) rot=(0,0,-1;0.349066rad)
  Width = 60
FEATURE [Part::Box] Box970  label="Krychle969"
  AttacherType = Attacher::AttachEngine3D
  Height = 7
  Length = 60
  Placement = pos=(-56.3816,-20.5212,-22) rot=(0,0,1;0.349066rad)
  Width = 60
FEATURE [Part::Compound] Compound1137
  Links = -> [Box969,Box970]
FEATURE [Part::Box] Box971  label="Krychle970"
  AttacherType = Attacher::AttachEngine3D
  Height = 7
  Length = 60
  Placement = pos=(0,0,-22) rot=(0,0,-1;0.034907rad)
  Width = 60
FEATURE [Part::Box] Box972  label="Krychle971"
  AttacherType = Attacher::AttachEngine3D
  Height = 7
  Length = 120
  Placement = pos=(-60,-60,-22) rot=(0,0,-1;0rad)
  Width = 60
FEATURE [Part::Cut] Cut960
  Base = -> Tube099
  Tool = -> Box972
FEATURE [Part::Cut] Cut959
  Base = -> Cut960
  Placement = pos=(0,0,-7) rot=(0,0,1;0rad)
  Tool = -> Compound1137
FEATURE [Part::Box] Box973  label="Krychle972"
  AttacherType = Attacher::AttachEngine3D
  Height = 7
  Length = 60
  Placement = pos=(-59.9909,-1.04714,-22) rot=(0,0,1;0.017453rad)
  Width = 60
FEATURE [Part::Compound] Compound1136
  Links = -> [Box971,Box973]
FEATURE [Part::Box] Box974  label="Krychle973"
  AttacherType = Attacher::AttachEngine3D
  Height = 7
  Length = 120
  Placement = pos=(-60,-60,-22) rot=(0,0,-1;0rad)
  Width = 60
FEATURE [Part::Cut] Cut964
  Base = -> Tube100
  Tool = -> Box974
FEATURE [Part::Cut] Cut963
  Base = -> Cut964
  Placement = pos=(0,0,-7) rot=(0,0,1;0rad)
  Tool = -> Compound1136
FEATURE [Part::Cut] Cut958
  Base = -> Cut959
  Placement = pos=(0,0,32) rot=(0,0,1;0rad)
  Tool = -> Cut963
FEATURE [Part::Cut] Cut962
  Base = -> Cut961
  Placement = pos=(0,0,-8) rot=(0,0,1;0rad)
  Tool = -> Cut958
FEATURE [Part::Box] Box975  label="Krychle974"
  AttacherType = Attacher::AttachEngine3D
  Height = 28.2
  Length = 2.2
  Placement = pos=(-12.1,-111,-4.1) rot=(0,0,1;0rad)
  Width = 20
FEATURE [Part::Box] Box976  label="Krychle975"
  AttacherType = Attacher::AttachEngine3D
  Height = 28.2
  Length = 2.2
  Placement = pos=(43.9,-111,-4.1) rot=(0,0,1;0rad)
  Width = 20
FEATURE [Part::Compound] Compound1138
  Links = -> [Box975,Box976]
  Placement = pos=(-17,10,97) rot=(1,0,0;1.5708rad)
FEATURE [Part::Cut] Cut1048
  Base = -> Cut962
  Tool = -> Compound1138
FEATURE [Part::Box] Box977  label="Krychle976"
  AttacherType = Attacher::AttachEngine3D
  Height = 28.2
  Length = 5
  Placement = pos=(-15.1,-108,-4.1) rot=(0,0,1;0rad)
  Width = 7
FEATURE [Part::Box] Box978  label="Krychle977"
  AttacherType = Attacher::AttachEngine3D
  Height = 28.2
  Length = 5
  Placement = pos=(43.9,-108,-4.1) rot=(0,0,1;0rad)
  Width = 7
FEATURE [Part::Compound] Compound1140
  Links = -> [Box977,Box978]
  Placement = pos=(-17,10,103) rot=(1,0,0;1.5708rad)
FEATURE [Part::Box] Box979  label="Krychle978"
  AttacherType = Attacher::AttachEngine3D
  Height = 28.2
  Length = 2.2
  Placement = pos=(-12.1,-111,-4.1) rot=(0,0,1;0rad)
  Width = 20
FEATURE [Part::Box] Box980  label="Krychle979"
  AttacherType = Attacher::AttachEngine3D
  Height = 28.2
  Length = 2.2
  Placement = pos=(43.9,-111,-4.1) rot=(0,0,1;0rad)
  Width = 20
FEATURE [Part::Compound] Compound1141
  Links = -> [Box979,Box980]
  Placement = pos=(-17,10,97) rot=(1,0,0;1.5708rad)
FEATURE [Part::Cut] Cut966
  Base = -> Compound1140
  Tool = -> Compound1141
FEATURE [Part::Cylinder] Cylinder2559  label="Válec2529"
  Angle = 360
  AttacherType = Attacher::AttachEngine3D
  Height = 30
  Placement = pos=(-17,-108,2) rot=(0,1,0;1.5708rad)
  Radius = 1
FEATURE [Part::Cylinder] Cylinder2560  label="Válec2530"
  Angle = 360
  AttacherType = Attacher::AttachEngine3D
  Height = 30
  Placement = pos=(-17,-108,18) rot=(0,1,0;1.5708rad)
  Radius = 1
FEATURE [Part::Cylinder] Cylinder2561  label="Válec2531"
  Angle = 360
  AttacherType = Attacher::AttachEngine3D
  Height = 30
  Placement = pos=(32,-108,18) rot=(0,1,0;1.5708rad)
  Radius = 1
FEATURE [Part::Cylinder] Cylinder2562  label="Válec2532"
  Angle = 360
  AttacherType = Attacher::AttachEngine3D
  Height = 30
  Placement = pos=(32,-108,2) rot=(0,1,0;1.5708rad)
  Radius = 1
FEATURE [Part::Compound] Compound1142
  Links = -> [Cylinder2559,Cylinder2560,Cylinder2561,Cylinder2562]
  Placement = pos=(-22,10,106.5) rot=(1,0,0;1.5708rad)
FEATURE [Part::Cut] Cut1049
  Base = -> Cut966
  Tool = -> Compound1142
FEATURE [Part::Cylinder] Cylinder2563  label="Válec2533"
  Angle = 360
  AttacherType = Attacher::AttachEngine3D
  Height = 30
  Placement = pos=(-17,-108,2) rot=(0,1,0;1.5708rad)
  Radius = 1
FEATURE [Part::Cylinder] Cylinder2564  label="Válec2534"
  Angle = 360
  AttacherType = Attacher::AttachEngine3D
  Height = 30
  Placement = pos=(-17,-108,18) rot=(0,1,0;1.5708rad)
  Radius = 1
FEATURE [Part::Cylinder] Cylinder2565  label="Válec2535"
  Angle = 360
  AttacherType = Attacher::AttachEngine3D
  Height = 30
  Placement = pos=(32,-108,18) rot=(0,1,0;1.5708rad)
  Radius = 1
FEATURE [Part::Cylinder] Cylinder2566  label="Válec2536"
  Angle = 360
  AttacherType = Attacher::AttachEngine3D
  Height = 30
  Placement = pos=(32,-108,2) rot=(0,1,0;1.5708rad)
  Radius = 1
FEATURE [Part::Compound] Compound1143
  Links = -> [Cylinder2563,Cylinder2564,Cylinder2565,Cylinder2566]
  Placement = pos=(-22,10,106.5) rot=(1,0,0;1.5708rad)
FEATURE [Part::Cut] Cut1050
  Base = -> Cut1048
  Tool = -> Compound1143
FEATURE [Part::Cylinder] Cylinder2567  label="Válec2537"
  Angle = 360
  AttacherType = Attacher::AttachEngine3D
  Height = 4
  Placement = pos=(-18,-106.5,2) rot=(0,1,0;1.5708rad)
  Radius = 2
FEATURE [Part::Cylinder] Cylinder2568  label="Válec2538"
  Angle = 360
  AttacherType = Attacher::AttachEngine3D
  Height = 4
  Placement = pos=(-18,-106.5,18) rot=(0,1,0;1.5708rad)
  Radius = 2
FEATURE [Part::Cylinder] Cylinder2569  label="Válec2539"
  Angle = 360
  AttacherType = Attacher::AttachEngine3D
  Height = 4
  Placement = pos=(50,-106.5,18) rot=(0,1,0;1.5708rad)
  Radius = 2
FEATURE [Part::Cylinder] Cylinder2570  label="Válec2540"
  Angle = 360
  AttacherType = Attacher::AttachEngine3D
  Height = 4
  Placement = pos=(50,-106.5,2) rot=(0,1,0;1.5708rad)
  Radius = 2
FEATURE [Part::Compound] Compound1144
  Links = -> [Cylinder2567,Cylinder2568,Cylinder2569,Cylinder2570]
  Placement = pos=(-18,10,105) rot=(1,0,0;1.5708rad)
FEATURE [Part::Cut] Cut1051
  Base = -> Cut1050
  Tool = -> Compound1144
FEATURE [Part::Cut] Cut1052
  Base = -> Cut1049
  Tool = -> Compound1130
FEATURE [Part::Compound] Compound1150
  Links = -> [Cut1051,Cut1052]
FEATURE [Part::Cylinder] Cylinder2581  label="Válec2551"
  Angle = 360
  AttacherType = Attacher::AttachEngine3D
  Height = 34
  Placement = pos=(0,0,-21) rot=(0,0,1;0rad)
  Radius = 31
FEATURE [Part::Cylinder] Cylinder2582  label="Válec2552"
  Angle = 360
  AttacherType = Attacher::AttachEngine3D
  Height = 3
  Radius = 39
FEATURE [Part::Cut] Cut1053
  Base = -> Cylinder2582
  Tool = -> Cylinder2581
FEATURE [Part::Box] Box981  label="Krychle980"
  AttacherType = Attacher::AttachEngine3D
  Height = 28.2
  Length = 2.2
  Placement = pos=(-12.1,-111,-4.1) rot=(0,0,1;0rad)
  Width = 20
FEATURE [Part::Box] Box982  label="Krychle981"
  AttacherType = Attacher::AttachEngine3D
  Height = 28.2
  Length = 2.2
  Placement = pos=(43.9,-111,-4.1) rot=(0,0,1;0rad)
  Width = 20
FEATURE [Part::Compound] Compound1153
  Links = -> [Box981,Box982]
  Placement = pos=(-17,10,97) rot=(1,0,0;1.5708rad)
FEATURE [Part::Box] Box983  label="Krychle982"
  AttacherType = Attacher::AttachEngine3D
  Height = 28.2
  Length = 5
  Placement = pos=(-15.1,-111,-4.1) rot=(0,0,1;0rad)
  Width = 3
FEATURE [Part::Box] Box984  label="Krychle983"
  AttacherType = Attacher::AttachEngine3D
  Height = 28.2
  Length = 5
  Placement = pos=(43.9,-111,-4.1) rot=(0,0,1;0rad)
  Width = 3
FEATURE [Part::Compound] Compound1155
  Links = -> [Box983,Box984]
  Placement = pos=(-17,10,103) rot=(1,0,0;1.5708rad)
FEATURE [Part::Box] Box985  label="Krychle984"
  AttacherType = Attacher::AttachEngine3D
  Height = 28.2
  Length = 2.2
  Placement = pos=(-12.1,-111,-4.1) rot=(0,0,1;0rad)
  Width = 20
FEATURE [Part::Box] Box986  label="Krychle985"
  AttacherType = Attacher::AttachEngine3D
  Height = 28.2
  Length = 2.2
  Placement = pos=(43.9,-111,-4.1) rot=(0,0,1;0rad)
  Width = 20
FEATURE [Part::Compound] Compound1154
  Links = -> [Box985,Box986]
  Placement = pos=(-17,10,97) rot=(1,0,0;1.5708rad)
FEATURE [Part::Cut] Cut1055
  Base = -> Compound1155
  Tool = -> Compound1154
FEATURE [Part::Chamfer] Chamfer092
  Base = -> Cut1053
  Edges = 1 edges r=1: [Edge1]
  Placement = pos=(0,0,-8) rot=(0,0,1;0rad)
FEATURE [Part::Cut] Cut1054
  Base = -> Chamfer092
  Tool = -> Compound1153
FEATURE [Part::Compound] Compound1152
  Links = -> [Cut1054,Cut1055]
  Placement = pos=(0,0,-3) rot=(1,0,0;3.14159rad)
FEATURE [Part::Cylinder] Cylinder2790  label="Válec2760"
  Angle = 360
  AttacherType = Attacher::AttachEngine3D
  Height = 20
  Placement = pos=(24,24,-12) rot=(0,0,1;0rad)
  Radius = 1
FEATURE [Part::Box] Box987  label="Krychle986"
  AttacherType = Attacher::AttachEngine3D
  Height = 1.5
  Length = 4
  Placement = pos=(22,22,3) rot=(0,0,1;0rad)
  Width = 4
FEATURE [Part::Box] Box988  label="Krychle987"
  AttacherType = Attacher::AttachEngine3D
  Height = 1.5
  Length = 4
  Placement = pos=(-22,22,3) rot=(0,0,1;1.5708rad)
  Width = 4
FEATURE [Part::Box] Box989  label="Krychle988"
  AttacherType = Attacher::AttachEngine3D
  Height = 1.5
  Length = 4
  Placement = pos=(-22,-22,3) rot=(0,0,1;3.14159rad)
  Width = 4
FEATURE [Part::Box] Box990  label="Krychle989"
  AttacherType = Attacher::AttachEngine3D
  Height = 1.5
  Length = 4
  Placement = pos=(22,-22,3) rot=(0,0,-1;1.5708rad)
  Width = 4
FEATURE [Part::Compound] Compound1242
  Links = -> [Box987,Box988,Box989,Box990]
  Placement = pos=(0,0,0.5) rot=(0,0,1;0rad)
FEATURE [Part::Cut] Cut1056
  Base = -> Compound1152
  Tool = -> Compound1242
FEATURE [Part::Cylinder] Cylinder2587  label="Válec2557"
  Angle = 360
  AttacherType = Attacher::AttachEngine3D
  Height = 20
  Placement = pos=(-24,24,-12) rot=(0,0,1;1.5708rad)
  Radius = 1
FEATURE [Part::Cylinder] Cylinder2588  label="Válec2558"
  Angle = 360
  AttacherType = Attacher::AttachEngine3D
  Height = 20
  Placement = pos=(-24,-24,-12) rot=(0,0,1;3.14159rad)
  Radius = 1
FEATURE [Part::Cylinder] Cylinder2589  label="Válec2559"
  Angle = 360
  AttacherType = Attacher::AttachEngine3D
  Height = 20
  Placement = pos=(24,-24,-12) rot=(0,0,-1;1.5708rad)
  Radius = 1
FEATURE [Part::Compound] Compound1243
  Links = -> [Cylinder2790,Cylinder2587,Cylinder2588,Cylinder2589]
FEATURE [Part::Cylinder] Cylinder2590  label="Válec2560"
  Angle = 360
  AttacherType = Attacher::AttachEngine3D
  Height = 20
  Placement = pos=(24,24,-12) rot=(0,0,1;0rad)
  Radius = 1
FEATURE [Part::Cylinder] Cylinder2591  label="Válec2561"
  Angle = 360
  AttacherType = Attacher::AttachEngine3D
  Height = 20
  Placement = pos=(-24,24,-12) rot=(0,0,1;1.5708rad)
  Radius = 1
FEATURE [Part::Cylinder] Cylinder2592  label="Válec2562"
  Angle = 360
  AttacherType = Attacher::AttachEngine3D
  Height = 20
  Placement = pos=(-24,-24,-12) rot=(0,0,1;3.14159rad)
  Radius = 1
FEATURE [Part::Cylinder] Cylinder2593  label="Válec2563"
  Angle = 360
  AttacherType = Attacher::AttachEngine3D
  Height = 20
  Placement = pos=(24,-24,-12) rot=(0,0,-1;1.5708rad)
  Radius = 1
FEATURE [Part::Compound] Compound1244
  Links = -> [Cylinder2590,Cylinder2591,Cylinder2592,Cylinder2593]
FEATURE [Part::Cut] Cut980
  Base = -> Cut1056
  Tool = -> Compound1244
FEATURE [Part::Cut] Cut1057
  Base = -> Compound1150
  Tool = -> Compound1243
FEATURE [Part::Compound] Compound1245  label="G-mini_encoder-belt-ring"
  Links = -> [Cut980,Cut1057]
  Placement = pos=(0,-59,37) rot=(0.57735,-0.57735,0.57735;2.0944rad)
FEATURE [Part::Box] Box991  label="Krychle990"
  AttacherType = Attacher::AttachEngine3D
  Height = 32
  Length = 5.85
  Placement = pos=(-10,-134,-6) rot=(0,0,1;0rad)
  Width = 56
FEATURE [Part::Box] Box992  label="Krychle991"
  AttacherType = Attacher::AttachEngine3D
  Height = 32
  Length = 5.85
  Placement = pos=(38.15,-134,-6) rot=(0,0,1;0rad)
  Width = 56
FEATURE [Part::Compound] Compound1246
  Links = -> [Box991,Box992]
FEATURE [Part::Box] Box993  label="Krychle992"
  AttacherType = Attacher::AttachEngine3D
  Height = 12
  Length = 46.3
  Placement = pos=(-23.15,-23.15,-70) rot=(0,0,1;0rad)
  Width = 46.3
FEATURE [Part::Box] Box994  label="Krychle993"
  AttacherType = Attacher::AttachEngine3D
  Height = 12
  Length = 42.3
  Placement = pos=(-21.15,-21.15,-70) rot=(0,0,1;0rad)
  Width = 42.3
FEATURE [Part::Cut] Cut1059
  Base = -> Box993
  Placement = pos=(17,-32,10) rot=(-1,0,0;1.5708rad)
  Tool = -> Box994
FEATURE [Part::Box] Box995  label="Krychle994"
  AttacherType = Attacher::AttachEngine3D
  Height = 12
  Length = 7
  Placement = pos=(-22,15,-74) rot=(0,0,1;0rad)
  Width = 7
FEATURE [Part::Cylinder] Cylinder2791  label="Válec2761"
  Angle = 360
  AttacherType = Attacher::AttachEngine3D
  Height = 12
  Placement = pos=(-15.15,15.15,-74) rot=(0,0,1;0rad)
  Radius = 6
FEATURE [Part::Cut] Cut1060
  Base = -> Box995
  Placement = pos=(0,0,0) rot=(0,0,1;1.5708rad)
  Tool = -> Cylinder2791
FEATURE [Part::Cylinder] Cylinder2792  label="Válec2762"
  Angle = 360
  AttacherType = Attacher::AttachEngine3D
  Height = 20
  Placement = pos=(-17,-108,18) rot=(0,1,0;1.5708rad)
  Radius = 1
FEATURE [Part::Cylinder] Cylinder2793  label="Válec2763"
  Angle = 360
  AttacherType = Attacher::AttachEngine3D
  Height = 20
  Placement = pos=(32,-108,2) rot=(0,1,0;1.5708rad)
  Radius = 1
FEATURE [Part::Cylinder] Cylinder2794  label="Válec2764"
  Angle = 360
  AttacherType = Attacher::AttachEngine3D
  Height = 20
  Placement = pos=(32,-108,18) rot=(0,1,0;1.5708rad)
  Radius = 1
FEATURE [Part::Box] Box996  label="Krychle995"
  AttacherType = Attacher::AttachEngine3D
  Height = 36
  Length = 7.85
  Placement = pos=(-10,-134,-8) rot=(0,0,1;0rad)
  Width = 56
FEATURE [Part::Box] Box997  label="Krychle996"
  AttacherType = Attacher::AttachEngine3D
  Height = 36
  Length = 7.85
  Placement = pos=(36.15,-134,-8) rot=(0,0,1;0rad)
  Width = 56
FEATURE [Part::Box] Box998  label="Krychle997"
  AttacherType = Attacher::AttachEngine3D
  Height = 36
  Length = 7.85
  Placement = pos=(36.15,-134,-8) rot=(0,0,1;0rad)
  Width = 56
FEATURE [Part::Box] Box999  label="Krychle998"
  AttacherType = Attacher::AttachEngine3D
  Height = 36
  Length = 7.85
  Placement = pos=(-10,-134,-8) rot=(0,0,1;0rad)
  Width = 56
FEATURE [Part::Cylinder] Cylinder2795  label="Válec2765"
  Angle = 360
  AttacherType = Attacher::AttachEngine3D
  Height = 10
  Placement = pos=(17,-98,44) rot=(1,0,0;1.5708rad)
  Radius = 2
FEATURE [Part::Box] Box1000  label="Krychle999"
  AttacherType = Attacher::AttachEngine3D
  Height = 28
  Length = 2
  Placement = pos=(-12,-117,-4) rot=(0,0,1;0rad)
  Width = 14
FEATURE [Part::Box] Box1001  label="Krychle1000"
  AttacherType = Attacher::AttachEngine3D
  Height = 28
  Length = 2
  Placement = pos=(44,-117,-4) rot=(0,0,1;0rad)
  Width = 14
FEATURE [Part::Cylinder] Cylinder2796  label="Válec2766"
  Angle = 360
  AttacherType = Attacher::AttachEngine3D
  Height = 20
  Placement = pos=(-17,-108,2) rot=(0,1,0;1.5708rad)
  Radius = 1
FEATURE [Part::Chamfer] Chamfer160
  Base = -> Compound1246
  Edges = 2 edges r=2: [Edge2,Edge4]
FEATURE [Part::Chamfer] Chamfer161
  Base = -> Chamfer160
  Edges = 2 edges r=2: [Edge24,Edge26]
FEATURE [Part::Compound] Compound1248
  Links = -> [Box996,Box997]
FEATURE [Part::Compound] Compound1249
  Links = -> [Box999,Box998]
FEATURE [Part::Compound] Compound1253
  Links = -> [Cylinder2793,Cylinder2794]
  Placement = pos=(0,-3,0) rot=(0,0,1;0rad)
FEATURE [Part::Compound] Compound1254
  Links = -> [Cylinder2796,Cylinder2792]
  Placement = pos=(0,-3,0) rot=(0,0,1;0rad)
FEATURE [Part::Compound] Compound1255
  Links = -> [Compound1253,Compound1254]
  Placement = pos=(0,-1.5,0) rot=(0,0,1;0rad)
FEATURE [Part::FeaturePython] Tube137  # WARN: FeaturePython — macro-defined, semantics opaque (R4)
  AttacherType = Attacher::AttachEngine3D
  Height = 12
  InnerRadius = 27
  OuterRadius = 34
  Placement = pos=(17,-92,10) rot=(1,0,0;1.5708rad)
FEATURE [Part::Cut] Cut1058
  Base = -> Tube137
  Tool = -> Chamfer161
FEATURE [Part::Torus] Torus007  label="Anuloid007"
  Angle1 = -180
  Angle2 = 180
  Angle3 = 360
  AttacherType = Attacher::AttachEngine3D
  Placement = pos=(17,-98,10) rot=(1,0,0;1.5708rad)
  Radius1 = 33.8
  Radius2 = 2
FEATURE [Part::Torus] Torus008  label="Anuloid008"
  Angle1 = -180
  Angle2 = 180
  Angle3 = 360
  AttacherType = Attacher::AttachEngine3D
  Placement = pos=(17,-98,10) rot=(1,0,0;1.5708rad)
  Radius1 = 33.8
  Radius2 = 2
FEATURE [Part::Cut] Cut1061
  Base = -> Box995
  Placement = pos=(0,0,0) rot=(0,0,-1;1.5708rad)
  Tool = -> Cylinder2791
FEATURE [Part::Cut] Cut1062
  Base = -> Box995
  Tool = -> Cylinder2791
FEATURE [Part::Cut] Cut1063
  Base = -> Box995
  Placement = pos=(0,0,0) rot=(0,0,1;3.14159rad)
  Tool = -> Cylinder2791
FEATURE [Part::Compound] Compound1247
  Links = -> [Cut1062,Cut1060,Cut1063,Cut1061]
  Placement = pos=(17,-28,10) rot=(-1,0,0;1.5708rad)
FEATURE [Part::Cut] Cut1064
  Base = -> Compound1247
  Tool = -> Compound1248
FEATURE [Part::Cut] Cut1065
  Base = -> Cut1059
  Tool = -> Compound1249
FEATURE [Part::Compound] Compound1250
  Links = -> [Cut1064,Cut1065]
  Placement = pos=(0,-2,0) rot=(0,0,1;0rad)
FEATURE [Part::Cut] Cut1066
  Base = -> Cut1058
  Tool = -> Torus008
FEATURE [Part::Cut] Cut1067
  Base = -> Compound1250
  Placement = pos=(0,-2,0) rot=(0,0,1;0rad)
  Tool = -> Torus007
FEATURE [Part::Cut] Cut1068
  Base = -> Cut1066
  Tool = -> Cylinder2795
FEATURE [Part::Compound] Compound1251  label="wrist_halo_inner004"
  Links = -> [Box1000,Box1001,Cut1068]
  Placement = pos=(0,-2,0) rot=(0,0,1;0rad)
FEATURE [Part::Compound] Compound1252  label="wrist_halo_inner005"
  Links = -> [Cut1067,Compound1251]
FEATURE [Part::Cut] Cut1069  label="Wrist_inner-halo"
  Base = -> Compound1252
  Placement = pos=(10,-170,54) rot=(0.707107,0,-0.707107;3.14159rad)
  Tool = -> Compound1255
FEATURE [Part::FeaturePython] Tube138  # WARN: FeaturePython — macro-defined, semantics opaque (R4)
  AttacherType = Attacher::AttachEngine3D
  Height = 6
  InnerRadius = 17
  OuterRadius = 25
  Placement = pos=(0,0,34) rot=(0,0,1;0rad)
FEATURE [Part::Box] Box1002  label="Krychle1001"
  AttacherType = Attacher::AttachEngine3D
  Height = 2
  Length = 6
  Placement = pos=(16.4057,10.0426,36) rot=(0,0,-1;1.1781rad)
  Width = 6
FEATURE [Part::Box] Box1003  label="Krychle1002"
  AttacherType = Attacher::AttachEngine3D
  Height = 2
  Length = 6
  Placement = pos=(10.0426,-16.4057,36) rot=(0,0,1;3.53429rad)
  Width = 6
FEATURE [Part::Cylinder] Cylinder2797  label="Válec2767"
  Angle = 360
  AttacherType = Attacher::AttachEngine3D
  Height = 60
  Placement = pos=(-8.41904,20.3253,34) rot=(0,0,1;0.392699rad)
  Radius = 1.5
FEATURE [Part::Box] Box1004  label="Krychle1003"
  AttacherType = Attacher::AttachEngine3D
  Height = 2
  Length = 6
  Placement = pos=(-16.4057,-10.0426,36) rot=(0,0,1;1.96349rad)
  Width = 6
FEATURE [Part::Box] Box1005  label="Krychle1004"
  AttacherType = Attacher::AttachEngine3D
  Height = 2
  Length = 6
  Placement = pos=(-10.0426,16.4057,36) rot=(0,0,1;0.392699rad)
  Width = 6
FEATURE [Part::Cylinder] Cylinder2798  label="Válec2768"
  Angle = 360
  AttacherType = Attacher::AttachEngine3D
  Height = 60
  Placement = pos=(20.3253,8.41904,34) rot=(0,0,-1;1.1781rad)
  Radius = 1.5
FEATURE [Part::Cylinder] Cylinder2799  label="Válec2769"
  Angle = 360
  AttacherType = Attacher::AttachEngine3D
  Height = 60
  Placement = pos=(8.41904,-20.3253,34) rot=(0,0,1;3.53429rad)
  Radius = 1.5
FEATURE [Part::Cylinder] Cylinder2800  label="Válec2770"
  Angle = 360
  AttacherType = Attacher::AttachEngine3D
  Height = 60
  Placement = pos=(-20.3253,-8.41904,34) rot=(0,0,1;1.96349rad)
  Radius = 1.5
FEATURE [Part::Cylinder] Cylinder2801  label="Válec2771"
  Angle = 360
  AttacherType = Attacher::AttachEngine3D
  Height = 60
  Placement = pos=(-8.41904,20.3253,34) rot=(0,0,1;0.392699rad)
  Radius = 1.5
FEATURE [Part::Cylinder] Cylinder2802  label="Válec2772"
  Angle = 360
  AttacherType = Attacher::AttachEngine3D
  Height = 2
  Placement = pos=(-18.5,0,26) rot=(0,0,1;1.5708rad)
  Radius = 2
FEATURE [Part::Cylinder] Cylinder2803  label="Válec2773"
  Angle = 360
  AttacherType = Attacher::AttachEngine3D
  Height = 2
  Placement = pos=(6e-15,-18.5,26) rot=(0,0,1;3.14159rad)
  Radius = 2
FEATURE [Part::Cylinder] Cylinder2804  label="Válec2774"
  Angle = 360
  AttacherType = Attacher::AttachEngine3D
  Height = 60
  Placement = pos=(20.3253,8.41904,34) rot=(0,0,-1;1.1781rad)
  Radius = 1.5
FEATURE [Part::Cylinder] Cylinder2805  label="Válec2775"
  Angle = 360
  AttacherType = Attacher::AttachEngine3D
  Height = 2
  Placement = pos=(13.08,-13.08,26) rot=(0,0,1;3.92699rad)
  Radius = 2
FEATURE [Part::Cylinder] Cylinder2806  label="Válec2776"
  Angle = 360
  AttacherType = Attacher::AttachEngine3D
  Height = 2
  Placement = pos=(18.5,8e-15,26) rot=(0,0,-1;1.5708rad)
  Radius = 2
FEATURE [Part::Cylinder] Cylinder2807  label="Válec2777"
  Angle = 360
  AttacherType = Attacher::AttachEngine3D
  Height = 2
  Placement = pos=(13.08,13.08,26) rot=(0,0,-1;0.785398rad)
  Radius = 2
FEATURE [Part::Cylinder] Cylinder2808  label="Válec2778"
  Angle = 360
  AttacherType = Attacher::AttachEngine3D
  Height = 2
  Placement = pos=(-13.08,13.08,26) rot=(0,0,1;0.785398rad)
  Radius = 2
FEATURE [Part::Cylinder] Cylinder2809  label="Válec2779"
  Angle = 360
  AttacherType = Attacher::AttachEngine3D
  Height = 2
  Placement = pos=(-13.08,-13.08,26) rot=(0,0,1;2.35619rad)
  Radius = 2
FEATURE [Part::Cylinder] Cylinder2810  label="Válec2780"
  Angle = 360
  AttacherType = Attacher::AttachEngine3D
  Height = 2
  Placement = pos=(0,0,40) rot=(0,0,1;0rad)
  Radius = 25
FEATURE [Part::Cylinder] Cylinder2811  label="Válec2781"
  Angle = 360
  AttacherType = Attacher::AttachEngine3D
  Height = 2
  Placement = pos=(18.5,8e-15,26) rot=(0,0,-1;1.5708rad)
  Radius = 2
FEATURE [Part::Cylinder] Cylinder2812  label="Válec2782"
  Angle = 360
  AttacherType = Attacher::AttachEngine3D
  Height = 2
  Placement = pos=(13.08,13.08,26) rot=(0,0,-1;0.785398rad)
  Radius = 2
FEATURE [Part::Cylinder] Cylinder2813  label="Válec2783"
  Angle = 360
  AttacherType = Attacher::AttachEngine3D
  Height = 2
  Placement = pos=(-18.5,0,26) rot=(0,0,1;1.5708rad)
  Radius = 2
FEATURE [Part::Cylinder] Cylinder2814  label="Válec2784"
  Angle = 360
  AttacherType = Attacher::AttachEngine3D
  Height = 2
  Placement = pos=(13.08,-13.08,26) rot=(0,0,1;3.92699rad)
  Radius = 2
FEATURE [Part::Cylinder] Cylinder2815  label="Válec2785"
  Angle = 360
  AttacherType = Attacher::AttachEngine3D
  Height = 2
  Placement = pos=(6e-15,-18.5,26) rot=(0,0,1;3.14159rad)
  Radius = 2
FEATURE [Part::Cylinder] Cylinder2816  label="Válec2786"
  Angle = 360
  AttacherType = Attacher::AttachEngine3D
  Height = 2
  Placement = pos=(-13.08,-13.08,26) rot=(0,0,1;2.35619rad)
  Radius = 2
FEATURE [Part::Cylinder] Cylinder2817  label="Válec2787"
  Angle = 360
  AttacherType = Attacher::AttachEngine3D
  Height = 2
  Placement = pos=(0,18.5,26) rot=(0,0,1;0rad)
  Radius = 2
FEATURE [Part::Cylinder] Cylinder2818  label="Válec2788"
  Angle = 360
  AttacherType = Attacher::AttachEngine3D
  Height = 2
  Placement = pos=(-13.08,13.08,26) rot=(0,0,1;0.785398rad)
  Radius = 2
FEATURE [Part::Cylinder] Cylinder2819  label="Válec2789"
  Angle = 360
  AttacherType = Attacher::AttachEngine3D
  Height = 20
  Placement = pos=(18.5,8e-15,26) rot=(0,0,-1;1.5708rad)
  Radius = 1
FEATURE [Part::Cylinder] Cylinder2820  label="Válec2790"
  Angle = 360
  AttacherType = Attacher::AttachEngine3D
  Height = 20
  Placement = pos=(-13.08,13.08,26) rot=(0,0,1;0.785398rad)
  Radius = 1
FEATURE [Part::Cylinder] Cylinder2821  label="Válec2791"
  Angle = 360
  AttacherType = Attacher::AttachEngine3D
  Height = 20
  Placement = pos=(13.08,13.08,26) rot=(0,0,-1;0.785398rad)
  Radius = 1
FEATURE [Part::Cylinder] Cylinder2822  label="Válec2792"
  Angle = 360
  AttacherType = Attacher::AttachEngine3D
  Height = 20
  Placement = pos=(0,18.5,26) rot=(0,0,1;0rad)
  Radius = 1
FEATURE [Part::Cylinder] Cylinder2823  label="Válec2793"
  Angle = 360
  AttacherType = Attacher::AttachEngine3D
  Height = 20
  Placement = pos=(-13.08,-13.08,26) rot=(0,0,1;2.35619rad)
  Radius = 1
FEATURE [Part::Cylinder] Cylinder2824  label="Válec2794"
  Angle = 360
  AttacherType = Attacher::AttachEngine3D
  Height = 20
  Placement = pos=(-18.5,0,26) rot=(0,0,1;1.5708rad)
  Radius = 1
FEATURE [Part::Cylinder] Cylinder2825  label="Válec2795"
  Angle = 360
  AttacherType = Attacher::AttachEngine3D
  Height = 20
  Placement = pos=(13.08,-13.08,26) rot=(0,0,1;3.92699rad)
  Radius = 1
FEATURE [Part::Cylinder] Cylinder2826  label="Válec2796"
  Angle = 360
  AttacherType = Attacher::AttachEngine3D
  Height = 20
  Placement = pos=(6e-15,-18.5,26) rot=(0,0,1;3.14159rad)
  Radius = 1
FEATURE [Part::Cylinder] Cylinder2827  label="Válec2797"
  Angle = 360
  AttacherType = Attacher::AttachEngine3D
  Height = 2
  Placement = pos=(0,18.5,26) rot=(0,0,1;0rad)
  Radius = 2
FEATURE [Part::Cylinder] Cylinder2828  label="Válec2798"
  Angle = 360
  AttacherType = Attacher::AttachEngine3D
  Height = 60
  Placement = pos=(-20.3253,-8.41904,34) rot=(0,0,1;1.96349rad)
  Radius = 1.5
FEATURE [Part::Cylinder] Cylinder2829  label="Válec2799"
  Angle = 360
  AttacherType = Attacher::AttachEngine3D
  Height = 60
  Placement = pos=(8.41904,-20.3253,34) rot=(0,0,1;3.53429rad)
  Radius = 1.5
FEATURE [Part::Compound] Compound1257
  Links = -> [Box1002,Box1003,Box1004,Box1005]
FEATURE [Part::Compound] Compound1258
  Links = -> [Cylinder2797,Cylinder2828,Cylinder2829,Cylinder2804]
FEATURE [Part::Compound] Compound1259
  Links = -> [Cylinder2827,Cylinder2808,Cylinder2802,Cylinder2809,Cylinder2803,Cylinder2805,Cylinder2806,Cylinder2807]
  Placement = pos=(0,0,14) rot=(0,0,1;0rad)
FEATURE [Part::Cut] Cut1072
  Base = -> Cylinder2810
  Tool = -> Compound1259
FEATURE [Part::Compound] Compound1260
  Links = -> [Cylinder2801,Cylinder2800,Cylinder2799,Cylinder2798]
FEATURE [Part::Cut] Cut1073
  Base = -> Cut1072
  Tool = -> Compound1260
FEATURE [Part::Compound] Compound1261
  Links = -> [Cylinder2822,Cylinder2820,Cylinder2824,Cylinder2823,Cylinder2826,Cylinder2825,Cylinder2819,Cylinder2821]
FEATURE [Part::Compound] Compound1262
  Links = -> [Cylinder2817,Cylinder2818,Cylinder2813,Cylinder2816,Cylinder2815,Cylinder2814,Cylinder2811,Cylinder2812]
  Placement = pos=(0,0,14) rot=(0,0,1;0rad)
FEATURE [Part::Cut] Cut1071
  Base = -> Tube138
  Tool = -> Compound1262
FEATURE [Part::Cut] Cut1070
  Base = -> Cut1071
  Tool = -> Compound1261
FEATURE [Part::Cut] Cut1074
  Base = -> Cut1070
  Tool = -> Compound1258
FEATURE [Part::Cut] Cut1075
  Base = -> Cut1074
  Tool = -> Compound1257
FEATURE [Part::Compound] Compound1256  label="G-mini_actuator-drum"
  Links = -> [Cut1073,Cut1075]
  Placement = pos=(0,10,37) rot=(1,0,0;1.5708rad)
FEATURE [Mesh::Feature] Mesh  label="Wrist_moto-hold-nuovo (Meshed)"
FEATURE [Mesh::Feature] Mesh001  label="G-mini_encoder-belt-ring (Meshed)"
FEATURE [Mesh::Feature] Mesh002  label="G-mini_actuator-drum (Meshed)"
FEATURE [Mesh::Feature] Mesh003  label="Wrist_inner-halo (Meshed)"
FEATURE [Mesh::Feature] Mesh004  label="G-mini_moto-holder-A (Meshed)"
FEATURE [Part::Box] Box107  label="Krychle107"
  AttacherType = Attacher::AttachEngine3D
  Height = 4
  Length = 46.3
  Placement = pos=(-23.15,-23.15,-25) rot=(0,0,1;0rad)
  Width = 46.3
FEATURE [Part::Box] Box104  label="Krychle104"
  AttacherType = Attacher::AttachEngine3D
  Height = 8
  Length = 46.3
  Placement = pos=(-23.15,-23.15,-70) rot=(0,0,1;0rad)
  Width = 46.3
FEATURE [Part::Box] Box105  label="Krychle105"
  AttacherType = Attacher::AttachEngine3D
  Height = 8
  Length = 42.3
  Placement = pos=(-21.15,-21.15,-70) rot=(0,0,1;0rad)
  Width = 42.3
FEATURE [Part::Box] Box106  label="Krychle106"
  AttacherType = Attacher::AttachEngine3D
  Height = 20
  Length = 29
  Placement = pos=(-14.5,0,-75) rot=(0,0,1;0rad)
  Width = 45.5
FEATURE [Part::Cylinder] Cylinder326  label="Válec326"
  Angle = 360
  AttacherType = Attacher::AttachEngine3D
  Height = 20
  Placement = pos=(-10.48,15.75,-50) rot=(0,0,1;0rad)
  Radius = 1.5
FEATURE [Part::Box] Box111  label="Krychle111"
  AttacherType = Attacher::AttachEngine3D
  Height = 2
  Length = 8
  Placement = pos=(-24.5,16.5,-55) rot=(0,0,1;0rad)
  Width = 6
FEATURE [Part::Cylinder] Cylinder335  label="Válec335"
  Angle = 360
  AttacherType = Attacher::AttachEngine3D
  Height = 20
  Placement = pos=(10.48,15.75,-50) rot=(0,0,1;0rad)
  Radius = 1.5
FEATURE [Part::Compound] Compound108
  Links = -> [Cylinder326,Cylinder335]
  Placement = pos=(0,0,-10) rot=(0,0,1;0rad)
FEATURE [Part::Cylinder] Cylinder331  label="Válec331"
  Angle = 360
  AttacherType = Attacher::AttachEngine3D
  Height = 50
  Placement = pos=(0,0,-29) rot=(0,0,1;0rad)
  Radius = 8
FEATURE [Part::Cylinder] Cylinder339  label="Válec339"
  Angle = 360
  AttacherType = Attacher::AttachEngine3D
  Height = 10
  Placement = pos=(-19.5,19.5,-28) rot=(0,0,1;0rad)
  Radius = 1.5
FEATURE [Part::Box] Box112  label="Krychle112"
  AttacherType = Attacher::AttachEngine3D
  Height = 8
  Length = 7
  Placement = pos=(-22,15,-74) rot=(0,0,1;0rad)
  Width = 7
FEATURE [Part::Cylinder] Cylinder327  label="Válec327"
  Angle = 360
  AttacherType = Attacher::AttachEngine3D
  Height = 10
  Placement = pos=(19.5,-19.5,-28) rot=(0,0,1;0rad)
  Radius = 1.5
FEATURE [Part::Cylinder] Cylinder329  label="Válec329"
  Angle = 360
  AttacherType = Attacher::AttachEngine3D
  Height = 20
  Placement = pos=(15.5,15.5,-68) rot=(0,0,1;0rad)
  Radius = 1.5
FEATURE [Part::Box] Box109  label="Krychle109"
  AttacherType = Attacher::AttachEngine3D
  Height = 2
  Length = 8
  Placement = pos=(16.5,-22.5,-55) rot=(0,0,1;0rad)
  Width = 6
FEATURE [Part::Cylinder] Cylinder328  label="Válec328"
  Angle = 360
  AttacherType = Attacher::AttachEngine3D
  Height = 20
  Placement = pos=(15.5,-15.5,-68) rot=(0,0,1;0rad)
  Radius = 1.5
FEATURE [Part::Cylinder] Cylinder330  label="Válec330"
  Angle = 360
  AttacherType = Attacher::AttachEngine3D
  Height = 20
  Placement = pos=(-15.5,-15.5,-68) rot=(0,0,1;0rad)
  Radius = 1.5
FEATURE [Part::Box] Box108  label="Krychle108"
  AttacherType = Attacher::AttachEngine3D
  Height = 2
  Length = 8
  Placement = pos=(16.5,16.5,-55) rot=(0,0,1;0rad)
  Width = 6
FEATURE [Part::Cylinder] Cylinder332  label="Válec332"
  Angle = 360
  AttacherType = Attacher::AttachEngine3D
  Height = 3
  Placement = pos=(15.5,-15.5,-54) rot=(0,0,1;0rad)
  Radius = 3
FEATURE [Part::Box] Box110  label="Krychle110"
  AttacherType = Attacher::AttachEngine3D
  Height = 2
  Length = 8
  Placement = pos=(-24.5,-22.5,-55) rot=(0,0,1;0rad)
  Width = 6
FEATURE [Part::Compound] Compound105
  Links = -> [Box108,Box111,Box109,Box110]
  Placement = pos=(0,0,10) rot=(0,0,1;0rad)
FEATURE [Part::Cylinder] Cylinder333  label="Válec333"
  Angle = 360
  AttacherType = Attacher::AttachEngine3D
  Height = 3
  Placement = pos=(15.5,15.5,-54) rot=(0,0,1;0rad)
  Radius = 3
FEATURE [Part::Cylinder] Cylinder334  label="Válec334"
  Angle = 360
  AttacherType = Attacher::AttachEngine3D
  Height = 3
  Placement = pos=(-15.5,15.5,-54) rot=(0,0,1;0rad)
  Radius = 3
FEATURE [Part::Cylinder] Cylinder336  label="Válec336"
  Angle = 360
  AttacherType = Attacher::AttachEngine3D
  Height = 3
  Placement = pos=(-15.5,-15.5,-54) rot=(0,0,1;0rad)
  Radius = 3
FEATURE [Part::Compound] Compound110
  Links = -> [Cylinder336,Cylinder332,Cylinder334,Cylinder333]
FEATURE [Part::Cylinder] Cylinder337  label="Válec337"
  Angle = 360
  AttacherType = Attacher::AttachEngine3D
  Height = 10
  Placement = pos=(-19.5,-19.5,-28) rot=(0,0,1;0rad)
  Radius = 1.5
FEATURE [Part::Cylinder] Cylinder338  label="Válec338"
  Angle = 360
  AttacherType = Attacher::AttachEngine3D
  Height = 20
  Placement = pos=(-15.5,15.5,-68) rot=(0,0,1;0rad)
  Radius = 1.5
FEATURE [Part::Compound] Compound106
  Links = -> [Cylinder329,Cylinder338,Cylinder328,Cylinder330]
FEATURE [Part::Cylinder] Cylinder340  label="Válec340"
  Angle = 360
  AttacherType = Attacher::AttachEngine3D
  Height = 10
  Placement = pos=(19.5,19.5,-28) rot=(0,0,1;0rad)
  Radius = 1.5
FEATURE [Part::Compound] Compound109
  Links = -> [Cylinder337,Cylinder339,Cylinder327,Cylinder340]
FEATURE [Part::Cylinder] Cylinder341  label="Válec341"
  Angle = 360
  AttacherType = Attacher::AttachEngine3D
  Height = 8
  Placement = pos=(-15.15,15.15,-74) rot=(0,0,1;0rad)
  Radius = 6
FEATURE [Part::Cut] Cut118
  Base = -> Box112
  Placement = pos=(0,0,0) rot=(0,0,-1;1.5708rad)
  Tool = -> Cylinder341
FEATURE [Part::Cut] Cut119
  Base = -> Box112
  Placement = pos=(0,0,0) rot=(0,0,1;3.14159rad)
  Tool = -> Cylinder341
FEATURE [Part::Cut] Cut120
  Base = -> Box112
  Tool = -> Cylinder341
FEATURE [Part::Cut] Cut117
  Base = -> Box112
  Placement = pos=(0,0,0) rot=(0,0,1;1.5708rad)
  Tool = -> Cylinder341
FEATURE [Part::Cylinder] Cylinder342  label="Válec342"
  Angle = 360
  AttacherType = Attacher::AttachEngine3D
  Height = 20
  Placement = pos=(-19.5,-19.5,-28) rot=(0,0,1;0rad)
  Radius = 1.5
FEATURE [Part::Cylinder] Cylinder350  label="Válec350"
  Angle = 360
  AttacherType = Attacher::AttachEngine3D
  Height = 20
  Placement = pos=(-15.5,-15.5,-68) rot=(0,0,1;0rad)
  Radius = 1.5
FEATURE [Part::Cylinder] Cylinder345  label="Válec345"
  Angle = 360
  AttacherType = Attacher::AttachEngine3D
  Height = 20
  Placement = pos=(-19.5,19.5,-28) rot=(0,0,1;0rad)
  Radius = 1.5
FEATURE [Part::Cylinder] Cylinder344  label="Válec344"
  Angle = 360
  AttacherType = Attacher::AttachEngine3D
  Height = 20
  Placement = pos=(19.5,-19.5,-28) rot=(0,0,1;0rad)
  Radius = 1.5
FEATURE [Part::Cylinder] Cylinder343  label="Válec343"
  Angle = 360
  AttacherType = Attacher::AttachEngine3D
  Height = 20
  Placement = pos=(19.5,19.5,-28) rot=(0,0,1;0rad)
  Radius = 1.5
FEATURE [Part::Compound] Compound112
  Links = -> [Cylinder342,Cylinder345,Cylinder344,Cylinder343]
  Placement = pos=(0,0,-33) rot=(0,0,1;0rad)
FEATURE [Part::Box] Box115  label="Krychle115"
  AttacherType = Attacher::AttachEngine3D
  Height = 2
  Length = 8
  Placement = pos=(16.5,16.5,-55) rot=(0,0,1;0rad)
  Width = 6
FEATURE [Part::Box] Box116  label="Krychle116"
  AttacherType = Attacher::AttachEngine3D
  Height = 2
  Length = 8
  Placement = pos=(16.5,-22.5,-55) rot=(0,0,1;0rad)
  Width = 6
FEATURE [Part::Box] Box114  label="Krychle114"
  AttacherType = Attacher::AttachEngine3D
  Height = 2
  Length = 8
  Placement = pos=(-24.5,16.5,-55) rot=(0,0,1;0rad)
  Width = 6
FEATURE [Part::Box] Box113  label="Krychle113"
  AttacherType = Attacher::AttachEngine3D
  Height = 2
  Length = 8
  Placement = pos=(-24.5,-22.5,-55) rot=(0,0,1;0rad)
  Width = 6
FEATURE [Part::Box] Box119  label="Krychle119"
  AttacherType = Attacher::AttachEngine3D
  Height = 11
  Length = 34
  Placement = pos=(-17,-17,-73) rot=(0,0,1;0rad)
  Width = 34
FEATURE [Part::Cylinder] Cylinder352  label="Válec352"
  Angle = 360
  AttacherType = Attacher::AttachEngine3D
  Height = 20
  Placement = pos=(15.5,-15.5,-68) rot=(0,0,1;0rad)
  Radius = 1.5
FEATURE [Part::Box] Box117  label="Krychle117"
  AttacherType = Attacher::AttachEngine3D
  Height = 20
  Length = 29
  Placement = pos=(-14.5,0,-75) rot=(0,0,1;0rad)
  Width = 45.5
FEATURE [Part::Cylinder] Cylinder353  label="Válec353"
  Angle = 360
  AttacherType = Attacher::AttachEngine3D
  Height = 20
  Placement = pos=(15.5,15.5,-68) rot=(0,0,1;0rad)
  Radius = 1.5
FEATURE [Part::Box] Box118  label="Krychle118"
  AttacherType = Attacher::AttachEngine3D
  Height = 2
  Length = 46.3
  Placement = pos=(-23.15,-23.15,-64) rot=(0,0,1;0rad)
  Width = 46.3
FEATURE [Part::Cylinder] Cylinder351  label="Válec351"
  Angle = 360
  AttacherType = Attacher::AttachEngine3D
  Height = 20
  Placement = pos=(-15.5,15.5,-68) rot=(0,0,1;0rad)
  Radius = 1.5
FEATURE [Part::Compound] Compound115
  Links = -> [Cylinder353,Cylinder351,Cylinder352,Cylinder350]
FEATURE [Part::Cut] Cut115
  Base = -> Box107
  Tool = -> Cylinder331
FEATURE [Part::Cut] Cut114
  Base = -> Cut115
  Tool = -> Compound109
FEATURE [Part::Compound] Compound107
  Links = -> [Cut114]
  Placement = pos=(0,0,-30) rot=(0,0,1;0rad)
FEATURE [Part::Cut] Cut116
  Base = -> Compound107
  Tool = -> Compound105
FEATURE [Part::Cut] Cut112
  Base = -> Cut116
  Tool = -> Compound108
FEATURE [Part::Cut] Cut110
  Base = -> Box104
  Placement = pos=(0,0,-4) rot=(0,0,1;0rad)
  Tool = -> Box105
FEATURE [Part::Cut] Cut109
  Base = -> Cut110
  Placement = pos=(0,0,9) rot=(0,0,1;0rad)
  Tool = -> Box106
FEATURE [Part::Chamfer] Chamfer011
  Base = -> Cut109
  Edges = 4 edges r=2: [Edge1,Edge3,Edge6,Edge29]
FEATURE [Part::Chamfer] Chamfer012
  Base = -> Chamfer011
  Edges = 5 edges r=0.9: [Edge3,Edge24,Edge25,Edge27,Edge29]
FEATURE [Part::Cut] Cut113
  Base = -> Cut112
  Tool = -> Compound106
FEATURE [Part::Cut] Cut111
  Base = -> Cut113
  Tool = -> Compound110
FEATURE [Part::Chamfer] Chamfer010
  Base = -> Cut111
  Edges = 4 edges r=2: [Edge1,Edge3,Edge6,Edge22]
FEATURE [Part::Compound] Compound111
  Links = -> [Cut120,Cut117,Cut119,Cut118]
  Placement = pos=(0,0,9) rot=(0,0,1;0rad)
FEATURE [Part::Cut] Cut1076
  Base = -> Compound111
  Tool = -> Compound112
FEATURE [Part::Compound] Compound113
  Links = -> [Box115,Box114,Box116,Box113]
  Placement = pos=(0,0,-2) rot=(0,0,1;0rad)
FEATURE [Part::Cut] Cut123
  Base = -> Box118
  Placement = pos=(0,0,7) rot=(0,0,1;0rad)
  Tool = -> Box119
FEATURE [Part::Cut] Cut121
  Base = -> Cut123
  Tool = -> Compound115
FEATURE [Part::Cut] Cut122
  Base = -> Cut121
  Tool = -> Box117
FEATURE [Part::Chamfer] Chamfer162
  Base = -> Cut122
  Edges = 2 edges r=2: [Edge1,Edge3]
FEATURE [Part::Chamfer] Chamfer009
  Base = -> Chamfer162
  Edges = 2 edges r=2: [Edge53,Edge55]
FEATURE [Part::Cut] Cut124
  Base = -> Chamfer009
  Tool = -> Compound113
FEATURE [Part::Compound] Compound1263  label="G-mini_moto-holder-B-nuovo"
  Links = -> [Cut1076,Cut124,Chamfer010,Chamfer012]
FEATURE [Part::Cylinder] Cylinder2830  label="Válec2800"
  Angle = 360
  AttacherType = Attacher::AttachEngine3D
  Height = 20
  Placement = pos=(15.5,-15.5,-68) rot=(0,0,1;0rad)
  Radius = 1.5
FEATURE [Part::Box] Box1006  label="Krychle1005"
  AttacherType = Attacher::AttachEngine3D
  Height = 8
  Length = 54
  Placement = pos=(-27,-26,-24) rot=(0,0,1;0rad)
  Width = 52
FEATURE [Part::Cylinder] Cylinder2831  label="Válec2801"
  Angle = 360
  AttacherType = Attacher::AttachEngine3D
  Height = 20
  Placement = pos=(-10.48,15.75,-50) rot=(0,0,1;0rad)
  Radius = 1.5
FEATURE [Part::Box] Box1007  label="Krychle1006"
  AttacherType = Attacher::AttachEngine3D
  Height = 2
  Length = 8
  Placement = pos=(16.5,16.5,-55) rot=(0,0,1;0rad)
  Width = 6
FEATURE [Part::Cylinder] Cylinder2832  label="Válec2802"
  Angle = 360
  AttacherType = Attacher::AttachEngine3D
  Height = 20
  Placement = pos=(-21,23,-28) rot=(0,0,1;0rad)
  Radius = 1.5
FEATURE [Part::Cylinder] Cylinder2833  label="Válec2803"
  Angle = 360
  AttacherType = Attacher::AttachEngine3D
  Height = 20
  Placement = pos=(21,-23,-28) rot=(0,0,1;0rad)
  Radius = 1.5
FEATURE [Part::Cylinder] Cylinder2834  label="Válec2804"
  Angle = 360
  AttacherType = Attacher::AttachEngine3D
  Height = 3
  Placement = pos=(15.5,-15.5,-54) rot=(0,0,1;0rad)
  Radius = 3
FEATURE [Part::Cylinder] Cylinder2835  label="Válec2805"
  Angle = 360
  AttacherType = Attacher::AttachEngine3D
  Height = 3
  Placement = pos=(15.5,15.5,-54) rot=(0,0,1;0rad)
  Radius = 3
FEATURE [Part::Cylinder] Cylinder2836  label="Válec2806"
  Angle = 360
  AttacherType = Attacher::AttachEngine3D
  Height = 20
  Placement = pos=(21,23,-28) rot=(0,0,1;0rad)
  Radius = 1.5
FEATURE [Part::Box] Box1008  label="Krychle1007"
  AttacherType = Attacher::AttachEngine3D
  Height = 2
  Length = 8
  Placement = pos=(-24.5,-22.5,-55) rot=(0,0,1;0rad)
  Width = 6
FEATURE [Part::Box] Box1009  label="Krychle1008"
  AttacherType = Attacher::AttachEngine3D
  Height = 2
  Length = 8
  Placement = pos=(16.5,-22.5,-55) rot=(0,0,1;0rad)
  Width = 6
FEATURE [Part::Cylinder] Cylinder2837  label="Válec2807"
  Angle = 360
  AttacherType = Attacher::AttachEngine3D
  Height = 20
  Placement = pos=(15.5,15.5,-68) rot=(0,0,1;0rad)
  Radius = 1.5
FEATURE [Part::Cylinder] Cylinder2838  label="Válec2808"
  Angle = 360
  AttacherType = Attacher::AttachEngine3D
  Height = 20
  Placement = pos=(10.48,15.75,-50) rot=(0,0,1;0rad)
  Radius = 1.5
FEATURE [Part::Cylinder] Cylinder2839  label="Válec2809"
  Angle = 360
  AttacherType = Attacher::AttachEngine3D
  Height = 3
  Placement = pos=(-15.5,-15.5,-54) rot=(0,0,1;0rad)
  Radius = 3
FEATURE [Part::Box] Box1010  label="Krychle1009"
  AttacherType = Attacher::AttachEngine3D
  Height = 2
  Length = 6
  Placement = pos=(-17,19,-55) rot=(0,0,1;0rad)
  Width = 8
FEATURE [Part::Cylinder] Cylinder2840  label="Válec2810"
  Angle = 360
  AttacherType = Attacher::AttachEngine3D
  Height = 20
  Placement = pos=(-5.5,-17,10) rot=(1,0,0;1.5708rad)
  Radius = 2.65
FEATURE [Part::Box] Box1011  label="Krychle1010"
  AttacherType = Attacher::AttachEngine3D
  Height = 2
  Length = 8
  Placement = pos=(-24.5,16.5,-55) rot=(0,0,1;0rad)
  Width = 6
FEATURE [Part::Box] Box1012  label="Krychle1011"
  AttacherType = Attacher::AttachEngine3D
  Height = 2
  Length = 6
  Placement = pos=(25,19,-55) rot=(0,0,1;0rad)
  Width = 8
FEATURE [Part::Cylinder] Cylinder2841  label="Válec2811"
  Angle = 360
  AttacherType = Attacher::AttachEngine3D
  Height = 20
  Placement = pos=(-15.5,15.5,-68) rot=(0,0,1;0rad)
  Radius = 1.5
FEATURE [Part::Cylinder] Cylinder2842  label="Válec2812"
  Angle = 360
  AttacherType = Attacher::AttachEngine3D
  Height = 20
  Placement = pos=(32,-108,18) rot=(0,1,0;1.5708rad)
  Radius = 1
FEATURE [Part::Cylinder] Cylinder2843  label="Válec2813"
  Angle = 360
  AttacherType = Attacher::AttachEngine3D
  Height = 3
  Placement = pos=(10,-35,10) rot=(0,0,1;0rad)
  Radius = 3
FEATURE [Part::Cylinder] Cylinder2844  label="Válec2814"
  Angle = 360
  AttacherType = Attacher::AttachEngine3D
  Height = 20
  Placement = pos=(39.5,-17,10) rot=(1,0,0;1.5708rad)
  Radius = 2.65
FEATURE [Part::Cylinder] Cylinder2845  label="Válec2815"
  Angle = 360
  AttacherType = Attacher::AttachEngine3D
  Height = 3
  Placement = pos=(-15.5,15.5,-54) rot=(0,0,1;0rad)
  Radius = 3
FEATURE [Part::Cylinder] Cylinder2846  label="Válec2816"
  Angle = 360
  AttacherType = Attacher::AttachEngine3D
  Height = 20
  Placement = pos=(-21,-23,-28) rot=(0,0,1;0rad)
  Radius = 1.5
FEATURE [Part::Cylinder] Cylinder2847  label="Válec2817"
  Angle = 360
  AttacherType = Attacher::AttachEngine3D
  Height = 50
  Placement = pos=(0,0,-29) rot=(0,0,1;0rad)
  Radius = 8
FEATURE [Part::Box] Box1013  label="Krychle1012"
  AttacherType = Attacher::AttachEngine3D
  Height = 32
  Length = 5.85
  Placement = pos=(38.15,-138,-6) rot=(0,0,1;0rad)
  Width = 60
FEATURE [Part::Box] Box1014  label="Krychle1013"
  AttacherType = Attacher::AttachEngine3D
  Height = 2
  Length = 6
  Placement = pos=(25,-25,-55) rot=(0,0,1;0rad)
  Width = 8
FEATURE [Part::Box] Box1015  label="Krychle1014"
  AttacherType = Attacher::AttachEngine3D
  Height = 2
  Length = 6
  Placement = pos=(-17,-25,-55) rot=(0,0,1;0rad)
  Width = 8
FEATURE [Part::Box] Box1016  label="Krychle1015"
  AttacherType = Attacher::AttachEngine3D
  Height = 32
  Length = 5.85
  Placement = pos=(-10,-138,-6) rot=(0,0,1;0rad)
  Width = 60
FEATURE [Part::Cylinder] Cylinder2848  label="Válec2818"
  Angle = 360
  AttacherType = Attacher::AttachEngine3D
  Height = 20
  Placement = pos=(-15.5,-15.5,-68) rot=(0,0,1;0rad)
  Radius = 1.5
FEATURE [Part::Cylinder] Cylinder2849  label="Válec2819"
  Angle = 360
  AttacherType = Attacher::AttachEngine3D
  Height = 16
  Placement = pos=(18,9,64) rot=(0,1,0;1.5708rad)
  Radius = 1.5
FEATURE [Part::Cylinder] Cylinder2850  label="Válec2820"
  Angle = 360
  AttacherType = Attacher::AttachEngine3D
  Height = 16
  Placement = pos=(-28,9,64) rot=(0,1,0;1.5708rad)
  Radius = 1.5
FEATURE [Part::Box] Box1017  label="Krychle1016"
  AttacherType = Attacher::AttachEngine3D
  Height = 4
  Length = 4
  Placement = pos=(-7,-113,16) rot=(0,0,1;0rad)
  Width = 4
FEATURE [Part::Cylinder] Cylinder2851  label="Válec2821"
  Angle = 360
  AttacherType = Attacher::AttachEngine3D
  Height = 16
  Placement = pos=(18,-9,64) rot=(0,1,0;1.5708rad)
  Radius = 1.5
FEATURE [Part::Cylinder] Cylinder2852  label="Válec2822"
  Angle = 360
  AttacherType = Attacher::AttachEngine3D
  Height = 20
  Placement = pos=(-17,-108,18) rot=(0,1,0;1.5708rad)
  Radius = 1
FEATURE [Part::Cylinder] Cylinder2853  label="Válec2823"
  Angle = 360
  AttacherType = Attacher::AttachEngine3D
  Height = 3
  Placement = pos=(10,-35,10) rot=(0,0,1;0rad)
  Radius = 3
FEATURE [Part::Cylinder] Cylinder2854  label="Válec2824"
  Angle = 360
  AttacherType = Attacher::AttachEngine3D
  Height = 20
  Placement = pos=(-17,-108,2) rot=(0,1,0;1.5708rad)
  Radius = 1
FEATURE [Part::Box] Box1018  label="Krychle1017"
  AttacherType = Attacher::AttachEngine3D
  Height = 4
  Length = 4
  Placement = pos=(37,-113,16) rot=(0,0,1;0rad)
  Width = 4
FEATURE [Part::Cut] Cut1078
  Base = -> Box1006
  Tool = -> Cylinder2847
FEATURE [Part::Cylinder] Cylinder2855  label="Válec2825"
  Angle = 360
  AttacherType = Attacher::AttachEngine3D
  Height = 20
  Placement = pos=(32,-108,2) rot=(0,1,0;1.5708rad)
  Radius = 1
FEATURE [Part::Box] Box1019  label="Krychle1018"
  AttacherType = Attacher::AttachEngine3D
  Height = 4
  Length = 4
  Placement = pos=(37,-113,0) rot=(0,0,1;0rad)
  Width = 4
FEATURE [Part::Cylinder] Cylinder2856  label="Válec2826"
  Angle = 360
  AttacherType = Attacher::AttachEngine3D
  Height = 3
  Placement = pos=(-8,-35,10) rot=(0,0,1;0rad)
  Radius = 3
FEATURE [Part::Box] Box1020  label="Krychle1019"
  AttacherType = Attacher::AttachEngine3D
  Height = 4
  Length = 4
  Placement = pos=(-7,-113,0) rot=(0,0,1;0rad)
  Width = 4
FEATURE [Part::Cylinder] Cylinder2857  label="Válec2827"
  Angle = 360
  AttacherType = Attacher::AttachEngine3D
  Height = 3
  Placement = pos=(-8,-35,10) rot=(0,0,1;0rad)
  Radius = 3
FEATURE [Part::Cylinder] Cylinder2858  label="Válec2828"
  Angle = 360
  AttacherType = Attacher::AttachEngine3D
  Height = 16
  Placement = pos=(-28,-9,64) rot=(0,1,0;1.5708rad)
  Radius = 1.5
FEATURE [Part::Box] Box1021  label="Krychle1020"
  AttacherType = Attacher::AttachEngine3D
  Height = 11
  Length = 46.3
  Placement = pos=(-23.15,-23.15,-73) rot=(0,0,1;0rad)
  Width = 46.3
FEATURE [Part::Cylinder] Cylinder2859  label="Válec2829"
  Angle = 360
  AttacherType = Attacher::AttachEngine3D
  Height = 20
  Placement = pos=(-15.5,15.5,-68) rot=(0,0,1;0rad)
  Radius = 1.5
FEATURE [Part::Cylinder] Cylinder2860  label="Válec2830"
  Angle = 360
  AttacherType = Attacher::AttachEngine3D
  Height = 20
  Placement = pos=(-15.5,-15.5,-68) rot=(0,0,1;0rad)
  Radius = 1.5
FEATURE [Part::Box] Box1022  label="Krychle1021"
  AttacherType = Attacher::AttachEngine3D
  Height = 20
  Length = 29
  Placement = pos=(-14.5,0,-75) rot=(0,0,1;0rad)
  Width = 45.5
FEATURE [Part::Cylinder] Cylinder2861  label="Válec2831"
  Angle = 360
  AttacherType = Attacher::AttachEngine3D
  Height = 20
  Placement = pos=(15.5,15.5,-68) rot=(0,0,1;0rad)
  Radius = 1.5
FEATURE [Part::Box] Box1023  label="Krychle1022"
  AttacherType = Attacher::AttachEngine3D
  Height = 11
  Length = 34
  Placement = pos=(-17,-17,-73) rot=(0,0,1;0rad)
  Width = 34
FEATURE [Part::Cylinder] Cylinder2862  label="Válec2832"
  Angle = 360
  AttacherType = Attacher::AttachEngine3D
  Height = 20
  Placement = pos=(15.5,-15.5,-68) rot=(0,0,1;0rad)
  Radius = 1.5
FEATURE [Part::Compound] Compound1265
  Links = -> [Cylinder2831,Cylinder2838]
  Placement = pos=(0,0,-10) rot=(0,0,1;0rad)
FEATURE [Part::Compound] Compound1266
  Links = -> [Cylinder2854,Cylinder2852]
  Placement = pos=(0,-3,0) rot=(0,0,1;0rad)
FEATURE [Part::Compound] Compound1267
  Links = -> [Cylinder2846,Cylinder2836,Cylinder2832,Cylinder2833]
FEATURE [Part::Cut] Cut1084
  Base = -> Cut1078
  Tool = -> Compound1267
FEATURE [Part::Compound] Compound1264
  Links = -> [Cut1084]
  Placement = pos=(0,0,-30) rot=(0,0,1;0rad)
FEATURE [Part::Compound] Compound1268
  Links = -> [Cylinder2837,Cylinder2841,Cylinder2830,Cylinder2848]
  Placement = pos=(0,0,4) rot=(0,0,1;0rad)
FEATURE [Part::Compound] Compound1269
  Links = -> [Cylinder2839,Cylinder2834,Cylinder2845,Cylinder2835]
FEATURE [Part::Compound] Compound1270
  Links = -> [Cylinder2843,Cylinder2857]
FEATURE [Part::Compound] Compound1271
  Links = -> [Box1017,Box1020,Box1018,Box1019]
  Placement = pos=(0,-1.5,0) rot=(0,0,1;0rad)
FEATURE [Part::Compound] Compound1272
  Links = -> [Cylinder2855,Cylinder2842]
  Placement = pos=(0,-3,0) rot=(0,0,1;0rad)
FEATURE [Part::Compound] Compound1273
  Links = -> [Box1007,Box1011,Box1009,Box1008]
  Placement = pos=(0,0,10) rot=(0,0,1;0rad)
FEATURE [Part::Cut] Cut1085
  Base = -> Compound1264
  Tool = -> Compound1273
FEATURE [Part::Cut] Cut1087
  Base = -> Cut1085
  Tool = -> Compound1265
FEATURE [Part::Cut] Cut1086
  Base = -> Cut1087
  Tool = -> Compound1268
FEATURE [Part::Cut] Cut1088
  Base = -> Cut1086
  Placement = pos=(17,-127,10) rot=(1,0,0;1.5708rad)
  Tool = -> Compound1269
FEATURE [Part::Compound] Compound1274
  Links = -> [Cylinder2853,Cylinder2856]
  Placement = pos=(0,0,51) rot=(0,0,1;0rad)
FEATURE [Part::Compound] Compound1276
  Links = -> [Cylinder2850,Cylinder2858,Cylinder2849,Cylinder2851]
  Placement = pos=(14,-71,10) rot=(1,0,0;1.5708rad)
FEATURE [Part::Compound] Compound1277
  Links = -> [Compound1272,Compound1266]
  Placement = pos=(0,-1.5,0) rot=(0,0,1;0rad)
FEATURE [Part::Compound] Compound1278
  Links = -> [Compound1270,Compound1274]
FEATURE [Part::Compound] Compound1279
  Links = -> [Box1012,Box1010,Box1014,Box1015]
  Placement = pos=(10,-24,11) rot=(-1,0,0;1.5708rad)
FEATURE [Part::Cut] Cut1082
  Base = -> Cut1088
  Tool = -> Compound1279
FEATURE [Part::Chamfer] Chamfer166
  Base = -> Cut1082
  Edges = 1 edges r=3: [Edge17]
FEATURE [Part::Chamfer] Chamfer163
  Base = -> Chamfer166
  Edges = 1 edges r=3: [Edge33]
FEATURE [Part::Compound] Compound1280
  Links = -> [Cylinder2840,Cylinder2844]
  Placement = pos=(0,-40,0) rot=(0,0,1;0rad)
FEATURE [Part::Cut] Cut1081
  Base = -> Chamfer163
  Tool = -> Compound1280
FEATURE [Part::Compound] Compound1281
  Links = -> [Box1016,Box1013]
FEATURE [Part::Cut] Cut1079
  Base = -> Compound1281
  Tool = -> Compound1276
FEATURE [Part::Chamfer] Chamfer164
  Base = -> Cut1079
  Edges = 2 edges r=2: [Edge29,Edge31]
FEATURE [Part::Chamfer] Chamfer165
  Base = -> Chamfer164
  Edges = 2 edges r=2: [Edge26,Edge28]
FEATURE [Part::Cut] Cut1080
  Base = -> Chamfer165
  Tool = -> Compound1277
FEATURE [Part::Cut] Cut1083
  Base = -> Cut1080
  Tool = -> Compound1271
FEATURE [Part::Compound] Compound1275  label="Wrist_moto-hold002"
  Links = -> [Cut1083,Cut1081]
  Placement = pos=(-9,-170,20) rot=(0.707107,0,0.707107;3.14159rad)
FEATURE [Part::Cut] Cut1077  label="Wrist_moto-hold-oldo001"
  Base = -> Compound1275
  Placement = pos=(-1,0,0) rot=(0,0,1;0rad)
  Tool = -> Compound1278
FEATURE [Part::Compound] Compound1282
  Links = -> [Cylinder2861,Cylinder2859,Cylinder2862,Cylinder2860]
FEATURE [Part::Cut] Cut1090
  Base = -> Box1021
  Placement = pos=(0,0,7) rot=(0,0,1;0rad)
  Tool = -> Box1023
FEATURE [Part::Cut] Cut1089
  Base = -> Cut1090
  Tool = -> Compound1282
FEATURE [Part::Cut] Cut1091
  Base = -> Cut1089
  Placement = pos=(0,-144,37) rot=(0.57735,0.57735,-0.57735;2.0944rad)
  Tool = -> Box1022
FEATURE [Part::Chamfer] Chamfer167
  Base = -> Cut1091
  Edges = 2 edges r=6: [Edge3,Edge45]
FEATURE [Part::Chamfer] Chamfer168
  Base = -> Chamfer167
  Edges = 2 edges r=6: [Edge2,Edge29]
FEATURE [Part::Compound] Compound1283  label="Wrist_moto-hold-nuovo"
  Links = -> [Chamfer168,Cut1077]
FEATURE [Mesh::Feature] Mesh005  label="Wrist_moto-hold-nuovo (Meshed)001"
FEATURE [Part::Box] Box072  label="Krychle072"
  AttacherType = Attacher::AttachEngine3D
  Height = 8
  Length = 12
  Placement = pos=(-10,-73,22) rot=(0,0,1;0rad)
  Width = 52
FEATURE [Part::Box] Box073  label="Krychle073"
  AttacherType = Attacher::AttachEngine3D
  Height = 8
  Length = 12
  Placement = pos=(-10,-73,-10) rot=(0,0,1;0rad)
  Width = 52
FEATURE [Part::Compound] Compound1284
  Links = -> [Box072,Box073]
FEATURE [Part::Box] Box1024  label="Krychle1023"
  AttacherType = Attacher::AttachEngine3D
  Height = 8
  Length = 12
  Placement = pos=(-5,-73,-10) rot=(0,0,1;0rad)
  Width = 52
FEATURE [Part::Box] Box1025  label="Krychle1024"
  AttacherType = Attacher::AttachEngine3D
  Height = 8
  Length = 12
  Placement = pos=(-5,-73,22) rot=(0,0,1;0rad)
  Width = 52
FEATURE [Part::Compound] Compound1285
  Links = -> [Box1025,Box1024]
  Placement = pos=(37,0,0) rot=(0,0,1;0rad)
FEATURE [Part::Compound] Compound1286
  Links = -> [Compound1284,Compound1285]
FEATURE [Part::Box] Box1026  label="Krychle1025"
  AttacherType = Attacher::AttachEngine3D
  Height = 6
  Length = 6
  Placement = pos=(-7,-41,-10) rot=(0,0,1;0rad)
  Width = 2
FEATURE [Part::Box] Box1027  label="Krychle1026"
  AttacherType = Attacher::AttachEngine3D
  Height = 6
  Length = 6
  Placement = pos=(35,-41,-10) rot=(0,0,1;0rad)
  Width = 2
FEATURE [Part::Box] Box1028  label="Krychle1027"
  AttacherType = Attacher::AttachEngine3D
  Height = 6
  Length = 6
  Placement = pos=(-7,-41,24) rot=(0,0,1;0rad)
  Width = 2
FEATURE [Part::Box] Box1029  label="Krychle1028"
  AttacherType = Attacher::AttachEngine3D
  Height = 6
  Length = 6
  Placement = pos=(35,-41,24) rot=(0,0,1;0rad)
  Width = 2
FEATURE [Part::Compound] Compound1287
  Links = -> [Box1026,Box1027,Box1028,Box1029]
  Placement = pos=(0,-200,0) rot=(0,0,1;0rad)
FEATURE [Part::Cylinder] Cylinder2863  label="Válec2833"
  Angle = 360
  AttacherType = Attacher::AttachEngine3D
  Height = 3
  Placement = pos=(33,-32,0) rot=(1,0,0;1.5708rad)
  Radius = 3
FEATURE [Part::Cylinder] Cylinder2864  label="Válec2834"
  Angle = 360
  AttacherType = Attacher::AttachEngine3D
  Height = 3
  Placement = pos=(33,-32,20) rot=(1,0,0;1.5708rad)
  Radius = 3
FEATURE [Part::Cylinder] Cylinder2865  label="Válec2835"
  Angle = 360
  AttacherType = Attacher::AttachEngine3D
  Height = 3
  Placement = pos=(1,-32,0) rot=(1,0,0;1.5708rad)
  Radius = 3
FEATURE [Part::Cylinder] Cylinder2866  label="Válec2836"
  Angle = 360
  AttacherType = Attacher::AttachEngine3D
  Height = 3
  Placement = pos=(1,-32,20) rot=(1,0,0;1.5708rad)
  Radius = 3
FEATURE [Part::Compound] Compound039
  Links = -> [Cylinder2866,Cylinder2865,Cylinder2864,Cylinder2863]
  Placement = pos=(0,17,0) rot=(0,0,1;0rad)
FEATURE [Part::Box] Box204  label="Krychle204"
  AttacherType = Attacher::AttachEngine3D
  Height = 6
  Length = 54
  Placement = pos=(-10,-25,24) rot=(0,0,1;0rad)
  Width = 10
FEATURE [Part::Box] Box205  label="Krychle205"
  AttacherType = Attacher::AttachEngine3D
  Height = 6
  Length = 54
  Placement = pos=(-10,-25,-10) rot=(0,0,1;0rad)
  Width = 10
FEATURE [Part::Cylinder] Cylinder2867  label="Válec2837"
  Angle = 360
  AttacherType = Attacher::AttachEngine3D
  Height = 50
  Placement = pos=(1,-32,20) rot=(1,0,0;1.5708rad)
  Radius = 1.5
FEATURE [Part::Cylinder] Cylinder2868  label="Válec2838"
  Angle = 360
  AttacherType = Attacher::AttachEngine3D
  Height = 50
  Placement = pos=(1,-32,0) rot=(1,0,0;1.5708rad)
  Radius = 1.5
FEATURE [Part::Cylinder] Cylinder2869  label="Válec2839"
  Angle = 360
  AttacherType = Attacher::AttachEngine3D
  Height = 50
  Placement = pos=(33,-32,20) rot=(1,0,0;1.5708rad)
  Radius = 1.5
FEATURE [Part::Cylinder] Cylinder2870  label="Válec2840"
  Angle = 360
  AttacherType = Attacher::AttachEngine3D
  Height = 50
  Placement = pos=(33,-32,0) rot=(1,0,0;1.5708rad)
  Radius = 1.5
FEATURE [Part::Cylinder] Cylinder2871  label="Válec2841"
  Angle = 360
  AttacherType = Attacher::AttachEngine3D
  Height = 80
  Placement = pos=(38,-32,-7) rot=(1,0,0;1.5708rad)
  Radius = 1.5
FEATURE [Part::Compound] Compound1288
  Links = -> [Cylinder2867,Cylinder2868,Cylinder2869,Cylinder2870]
  Placement = pos=(0,20,0) rot=(0,0,1;0rad)
FEATURE [Part::Cut] Cut058
  Base = -> Compound1286
  Tool = -> Compound1288
FEATURE [Part::Cut] Cut1092
  Base = -> Cut058
  Tool = -> Compound1287
FEATURE [Part::Cut] Cut1093
  Base = -> Cut1092
  Tool = -> Compound039
FEATURE [Part::Compound] Compound135
  Links = -> [Box204,Box205]
FEATURE [Part::Cylinder] Cylinder2872  label="Válec2842"
  Angle = 360
  AttacherType = Attacher::AttachEngine3D
  Height = 80
  Placement = pos=(-4,-32,27) rot=(1,0,0;1.5708rad)
  Radius = 1.5
FEATURE [Part::Cylinder] Cylinder2873  label="Válec2843"
  Angle = 360
  AttacherType = Attacher::AttachEngine3D
  Height = 80
  Placement = pos=(-4,-32,-7) rot=(1,0,0;1.5708rad)
  Radius = 1.5
FEATURE [Part::Cylinder] Cylinder2874  label="Válec2844"
  Angle = 360
  AttacherType = Attacher::AttachEngine3D
  Height = 80
  Placement = pos=(38,-32,27) rot=(1,0,0;1.5708rad)
  Radius = 1.5
FEATURE [Part::Compound] Compound132
  Links = -> [Cylinder2872,Cylinder2873,Cylinder2874,Cylinder2871]
  Placement = pos=(0,20,0) rot=(0,0,1;0rad)
FEATURE [Part::Cut] Cut189
  Base = -> Cut1093
  Tool = -> Compound132
FEATURE [Part::Cylinder] Cylinder2875  label="Válec2845"
  Angle = 360
  AttacherType = Attacher::AttachEngine3D
  Height = 3
  Placement = pos=(38,-32,27) rot=(1,0,0;1.5708rad)
  Radius = 3
FEATURE [Part::Cylinder] Cylinder2876  label="Válec2846"
  Angle = 360
  AttacherType = Attacher::AttachEngine3D
  Height = 3
  Placement = pos=(-4,-32,-7) rot=(1,0,0;1.5708rad)
  Radius = 3
FEATURE [Part::Cylinder] Cylinder2877  label="Válec2847"
  Angle = 360
  AttacherType = Attacher::AttachEngine3D
  Height = 3
  Placement = pos=(-4,-32,27) rot=(1,0,0;1.5708rad)
  Radius = 3
FEATURE [Part::Cylinder] Cylinder2878  label="Válec2848"
  Angle = 360
  AttacherType = Attacher::AttachEngine3D
  Height = 3
  Placement = pos=(38,-32,-7) rot=(1,0,0;1.5708rad)
  Radius = 3
FEATURE [Part::Compound] Compound133
  Links = -> [Cylinder2877,Cylinder2876,Cylinder2875,Cylinder2878]
  Placement = pos=(0,17,0) rot=(0,0,1;0rad)
FEATURE [Part::Cylinder] Cylinder2879  label="Válec2849"
  Angle = 360
  AttacherType = Attacher::AttachEngine3D
  Height = 50
  Placement = pos=(38,-32,-7) rot=(1,0,0;1.5708rad)
  Radius = 1.5
FEATURE [Part::Cylinder] Cylinder2880  label="Válec2850"
  Angle = 360
  AttacherType = Attacher::AttachEngine3D
  Height = 50
  Placement = pos=(-4,-32,27) rot=(1,0,0;1.5708rad)
  Radius = 1.5
FEATURE [Part::Cylinder] Cylinder2881  label="Válec2851"
  Angle = 360
  AttacherType = Attacher::AttachEngine3D
  Height = 50
  Placement = pos=(-4,-32,-7) rot=(1,0,0;1.5708rad)
  Radius = 1.5
FEATURE [Part::Cylinder] Cylinder2882  label="Válec2852"
  Angle = 360
  AttacherType = Attacher::AttachEngine3D
  Height = 50
  Placement = pos=(38,-32,27) rot=(1,0,0;1.5708rad)
  Radius = 1.5
FEATURE [Part::Compound] Compound134
  Links = -> [Cylinder2880,Cylinder2881,Cylinder2882,Cylinder2879]
  Placement = pos=(0,20,0) rot=(0,0,1;0rad)
FEATURE [Part::Cut] Cut190
  Base = -> Compound135
  Tool = -> Compound134
FEATURE [Part::Cut] Cut191
  Base = -> Cut190
  Tool = -> Compound133
FEATURE [Part::Chamfer] Chamfer017
  Base = -> Cut191
  Edges = 2 edges r=3: [Edge3,Edge43]
FEATURE [Part::Chamfer] Chamfer018
  Base = -> Chamfer017
  Edges = 2 edges r=3: [Edge28,Edge73]
FEATURE [Part::Cylinder] Cylinder354  label="Válec354"
  Angle = 360
  AttacherType = Attacher::AttachEngine3D
  Height = 6
  Placement = pos=(21,23,-28) rot=(0,0,1;0rad)
  Radius = 3
FEATURE [Part::Cylinder] Cylinder355  label="Válec355"
  Angle = 360
  AttacherType = Attacher::AttachEngine3D
  Height = 6
  Placement = pos=(-21,23,-28) rot=(0,0,1;0rad)
  Radius = 3
FEATURE [Part::Cylinder] Cylinder356  label="Válec356"
  Angle = 360
  AttacherType = Attacher::AttachEngine3D
  Height = 6
  Placement = pos=(21,-23,-28) rot=(0,0,1;0rad)
  Radius = 3
FEATURE [Part::Cylinder] Cylinder357  label="Válec357"
  Angle = 360
  AttacherType = Attacher::AttachEngine3D
  Height = 6
  Placement = pos=(-21,-23,-28) rot=(0,0,1;0rad)
  Radius = 3
FEATURE [Part::Compound] Compound157
  Links = -> [Cylinder357,Cylinder354,Cylinder355,Cylinder356]
  Placement = pos=(17,-91,10) rot=(1,0,0;1.5708rad)
FEATURE [Part::Box] Box228  label="Krychle228"
  AttacherType = Attacher::AttachEngine3D
  Height = 6
  Length = 12
  Placement = pos=(-10,-73,-16) rot=(0,0,1;0rad)
  Width = 4
FEATURE [Part::Box] Box230  label="Krychle230"
  AttacherType = Attacher::AttachEngine3D
  Height = 6
  Length = 12
  Placement = pos=(-10,-69,-16) rot=(0,0,1;0rad)
  Width = 6
FEATURE [Part::Chamfer] Chamfer019
  Base = -> Box230
  Edges = 1 edges r=5.6: [Edge11]
FEATURE [Part::Compound] Compound158
  Links = -> [Box228,Chamfer019]
FEATURE [Part::Box] Box231  label="Krychle231"
  AttacherType = Attacher::AttachEngine3D
  Height = 6
  Length = 12
  Placement = pos=(-10,-73,-16) rot=(0,0,1;0rad)
  Width = 4
FEATURE [Part::Box] Box232  label="Krychle232"
  AttacherType = Attacher::AttachEngine3D
  Height = 6
  Length = 12
  Placement = pos=(-10,-69,-16) rot=(0,0,1;0rad)
  Width = 6
FEATURE [Part::Chamfer] Chamfer020
  Base = -> Box232
  Edges = 1 edges r=5.6: [Edge11]
FEATURE [Part::Compound] Compound159
  Links = -> [Box231,Chamfer020]
  Placement = pos=(42,0,0) rot=(0,0,1;0rad)
FEATURE [Part::Box] Box233  label="Krychle233"
  AttacherType = Attacher::AttachEngine3D
  Height = 6
  Length = 12
  Placement = pos=(-10,-73,30) rot=(0,0,1;0rad)
  Width = 4
FEATURE [Part::Box] Box234  label="Krychle234"
  AttacherType = Attacher::AttachEngine3D
  Height = 6
  Length = 12
  Placement = pos=(-10,-69,30) rot=(0,0,1;0rad)
  Width = 6
FEATURE [Part::Chamfer] Chamfer021
  Base = -> Box234
  Edges = 1 edges r=5.6: [Edge12]
FEATURE [Part::Compound] Compound160
  Links = -> [Box233,Chamfer021]
FEATURE [Part::Box] Box235  label="Krychle235"
  AttacherType = Attacher::AttachEngine3D
  Height = 6
  Length = 12
  Placement = pos=(-10,-69,30) rot=(0,0,1;0rad)
  Width = 6
FEATURE [Part::Chamfer] Chamfer022
  Base = -> Box235
  Edges = 1 edges r=5.6: [Edge12]
FEATURE [Part::Box] Box236  label="Krychle236"
  AttacherType = Attacher::AttachEngine3D
  Height = 6
  Length = 12
  Placement = pos=(-10,-73,30) rot=(0,0,1;0rad)
  Width = 4
FEATURE [Part::Compound] Compound161
  Links = -> [Box236,Chamfer022]
  Placement = pos=(42,0,0) rot=(0,0,1;0rad)
FEATURE [Part::Compound] Compound162
  Links = -> [Compound158,Compound161,Compound160,Compound159]
FEATURE [Part::Cylinder] Cylinder358  label="Válec358"
  Angle = 360
  AttacherType = Attacher::AttachEngine3D
  Height = 10
  Placement = pos=(21,23,-28) rot=(0,0,1;0rad)
  Radius = 1.5
FEATURE [Part::Cylinder] Cylinder359  label="Válec359"
  Angle = 360
  AttacherType = Attacher::AttachEngine3D
  Height = 10
  Placement = pos=(-21,23,-28) rot=(0,0,1;0rad)
  Radius = 1.5
FEATURE [Part::Cylinder] Cylinder360  label="Válec360"
  Angle = 360
  AttacherType = Attacher::AttachEngine3D
  Height = 10
  Placement = pos=(21,-23,-28) rot=(0,0,1;0rad)
  Radius = 1.5
FEATURE [Part::Cylinder] Cylinder361  label="Válec361"
  Angle = 360
  AttacherType = Attacher::AttachEngine3D
  Height = 10
  Placement = pos=(-21,-23,-28) rot=(0,0,1;0rad)
  Radius = 1.5
FEATURE [Part::Compound] Compound163
  Links = -> [Cylinder361,Cylinder358,Cylinder359,Cylinder360]
  Placement = pos=(17,-95,10) rot=(1,0,0;1.5708rad)
FEATURE [Part::Cylinder] Cylinder362  label="Válec362"
  Angle = 360
  AttacherType = Attacher::AttachEngine3D
  Height = 3
  Placement = pos=(38,-32,-7) rot=(1,0,0;1.5708rad)
  Radius = 3
FEATURE [Part::Cylinder] Cylinder363  label="Válec363"
  Angle = 360
  AttacherType = Attacher::AttachEngine3D
  Height = 3
  Placement = pos=(38,-32,27) rot=(1,0,0;1.5708rad)
  Radius = 3
FEATURE [Part::Cylinder] Cylinder364  label="Válec364"
  Angle = 360
  AttacherType = Attacher::AttachEngine3D
  Height = 3
  Placement = pos=(-4,-32,27) rot=(1,0,0;1.5708rad)
  Radius = 3
FEATURE [Part::Cylinder] Cylinder365  label="Válec365"
  Angle = 360
  AttacherType = Attacher::AttachEngine3D
  Height = 3
  Placement = pos=(-4,-32,-7) rot=(1,0,0;1.5708rad)
  Radius = 3
FEATURE [Part::Compound] Compound164
  Links = -> [Cylinder364,Cylinder365,Cylinder363,Cylinder362]
  Placement = pos=(0,-38,0) rot=(0,0,1;0rad)
FEATURE [Part::Cut] Cut224
  Base = -> Compound162
  Tool = -> Compound157
FEATURE [Part::Cut] Cut225
  Base = -> Cut224
  Tool = -> Compound163
FEATURE [Part::Cut] Cut226
  Base = -> Cut189
  Tool = -> Compound164
FEATURE [Part::Cylinder] Cylinder419  label="Válec419"
  Angle = 360
  AttacherType = Attacher::AttachEngine3D
  Height = 32
  Placement = pos=(7,-10,-6) rot=(0,0,1;0rad)
  Radius = 8
FEATURE [Part::Cylinder] Cylinder420  label="Válec420"
  Angle = 360
  AttacherType = Attacher::AttachEngine3D
  Height = 32
  Placement = pos=(27,-10,-6) rot=(0,0,1;0rad)
  Radius = 8
FEATURE [Part::Compound] Compound197
  Links = -> [Cylinder419,Cylinder420]
FEATURE [Part::Cut] Cut252
  Base = -> Chamfer018
  Tool = -> Compound197
FEATURE [Part::Cylinder] Cylinder439  label="Válec439"
  Angle = 360
  AttacherType = Attacher::AttachEngine3D
  Height = 20
  Placement = pos=(31,-10,10) rot=(1,0,0;1.5708rad)
  Radius = 1
FEATURE [Part::Box] Box291  label="Krychle291"
  AttacherType = Attacher::AttachEngine3D
  Height = 8
  Length = 54
  Placement = pos=(-10,-21,6) rot=(0,0,1;0rad)
  Width = 6
FEATURE [Part::Cylinder] Cylinder440  label="Válec440"
  Angle = 360
  AttacherType = Attacher::AttachEngine3D
  Height = 20
  Placement = pos=(3,-10,10) rot=(1,0,0;1.5708rad)
  Radius = 1
FEATURE [Part::Cylinder] Cylinder441  label="Válec441"
  Angle = 360
  AttacherType = Attacher::AttachEngine3D
  Height = 20
  Placement = pos=(17,-10,8) rot=(1,0,0;1.5708rad)
  Radius = 1
FEATURE [Part::Cylinder] Cylinder442  label="Válec442"
  Angle = 360
  AttacherType = Attacher::AttachEngine3D
  Height = 20
  Placement = pos=(17,-10,12) rot=(1,0,0;1.5708rad)
  Radius = 1
FEATURE [Part::Cylinder] Cylinder443  label="Válec443"
  Angle = 360
  AttacherType = Attacher::AttachEngine3D
  Height = 2
  Placement = pos=(31,-10,10) rot=(1,0,0;1.5708rad)
  Radius = 2
FEATURE [Part::Cylinder] Cylinder444  label="Válec444"
  Angle = 360
  AttacherType = Attacher::AttachEngine3D
  Height = 2
  Placement = pos=(17,-10,12) rot=(1,0,0;1.5708rad)
  Radius = 2
FEATURE [Part::Cylinder] Cylinder445  label="Válec445"
  Angle = 360
  AttacherType = Attacher::AttachEngine3D
  Height = 2
  Placement = pos=(3,-10,10) rot=(1,0,0;1.5708rad)
  Radius = 2
FEATURE [Part::Cylinder] Cylinder446  label="Válec446"
  Angle = 360
  AttacherType = Attacher::AttachEngine3D
  Height = 2
  Placement = pos=(17,-10,8) rot=(1,0,0;1.5708rad)
  Radius = 2
FEATURE [Part::Cylinder] Cylinder447  label="Válec447"
  Angle = 360
  AttacherType = Attacher::AttachEngine3D
  Height = 20
  Placement = pos=(-5,-17,10) rot=(1,0,0;1.5708rad)
  Radius = 2.65
FEATURE [Part::Cylinder] Cylinder448  label="Válec448"
  Angle = 360
  AttacherType = Attacher::AttachEngine3D
  Height = 20
  Placement = pos=(39,-17,10) rot=(1,0,0;1.5708rad)
  Radius = 2.65
FEATURE [Part::Box] Box292  label="Krychle292"
  AttacherType = Attacher::AttachEngine3D
  Height = 10
  Length = 54
  Placement = pos=(-10,-21,14) rot=(0,0,1;0rad)
  Width = 6
FEATURE [Part::Cylinder] Cylinder449  label="Válec449"
  Angle = 360
  AttacherType = Attacher::AttachEngine3D
  Height = 10
  Placement = pos=(27,-10,-4) rot=(0,0,1;0rad)
  Radius = 8
FEATURE [Part::Cylinder] Cylinder450  label="Válec450"
  Angle = 360
  AttacherType = Attacher::AttachEngine3D
  Height = 10
  Placement = pos=(7,-10,14) rot=(0,0,1;0rad)
  Radius = 8
FEATURE [Part::Cylinder] Cylinder451  label="Válec451"
  Angle = 360
  AttacherType = Attacher::AttachEngine3D
  Height = 10
  Placement = pos=(7,-10,-4) rot=(0,0,1;0rad)
  Radius = 8
FEATURE [Part::Cylinder] Cylinder452  label="Válec452"
  Angle = 360
  AttacherType = Attacher::AttachEngine3D
  Height = 10
  Placement = pos=(27,-10,14) rot=(0,0,1;0rad)
  Radius = 8
FEATURE [Part::Box] Box293  label="Krychle293"
  AttacherType = Attacher::AttachEngine3D
  Height = 10
  Length = 54
  Placement = pos=(-10,-21,-4) rot=(0,0,1;0rad)
  Width = 6
FEATURE [Part::Cylinder] Cylinder453  label="Válec453"
  Angle = 360
  AttacherType = Attacher::AttachEngine3D
  Height = 50
  Placement = pos=(-5,-32,-7) rot=(1,0,0;1.5708rad)
  Radius = 1.5
FEATURE [Part::Cylinder] Cylinder454  label="Válec454"
  Angle = 360
  AttacherType = Attacher::AttachEngine3D
  Height = 3
  Placement = pos=(-5,-32,27) rot=(1,0,0;1.5708rad)
  Radius = 3
FEATURE [Part::Cylinder] Cylinder455  label="Válec455"
  Angle = 360
  AttacherType = Attacher::AttachEngine3D
  Height = 50
  Placement = pos=(39,-32,27) rot=(1,0,0;1.5708rad)
  Radius = 1.5
FEATURE [Part::Cylinder] Cylinder456  label="Válec456"
  Angle = 360
  AttacherType = Attacher::AttachEngine3D
  Height = 3
  Placement = pos=(-5,-32,-7) rot=(1,0,0;1.5708rad)
  Radius = 3
FEATURE [Part::Cylinder] Cylinder457  label="Válec457"
  Angle = 360
  AttacherType = Attacher::AttachEngine3D
  Height = 50
  Placement = pos=(39,-32,-7) rot=(1,0,0;1.5708rad)
  Radius = 1.5
FEATURE [Part::Cylinder] Cylinder458  label="Válec458"
  Angle = 360
  AttacherType = Attacher::AttachEngine3D
  Height = 3
  Placement = pos=(39,-32,27) rot=(1,0,0;1.5708rad)
  Radius = 3
FEATURE [Part::Cylinder] Cylinder459  label="Válec459"
  Angle = 360
  AttacherType = Attacher::AttachEngine3D
  Height = 3
  Placement = pos=(39,-32,-7) rot=(1,0,0;1.5708rad)
  Radius = 3
FEATURE [Part::Cylinder] Cylinder460  label="Válec460"
  Angle = 360
  AttacherType = Attacher::AttachEngine3D
  Height = 50
  Placement = pos=(-5,-32,27) rot=(1,0,0;1.5708rad)
  Radius = 1.5
FEATURE [Part::Cut] Cut272
  Base = -> Box293
  Tool = -> Cylinder451
FEATURE [Part::Cut] Cut270
  Base = -> Cut272
  Tool = -> Cylinder449
FEATURE [Part::Cut] Cut273
  Base = -> Box292
  Tool = -> Cylinder450
FEATURE [Part::Cut] Cut271
  Base = -> Cut273
  Tool = -> Cylinder452
FEATURE [Part::Compound] Compound217
  Links = -> [Cylinder445,Cylinder443,Cylinder446,Cylinder444]
  Placement = pos=(0,-9,0) rot=(0,0,1;0rad)
FEATURE [Part::Cut] Cut267
  Base = -> Box291
  Tool = -> Compound217
FEATURE [Part::Compound] Compound218
  Links = -> [Cylinder440,Cylinder439,Cylinder441,Cylinder442]
FEATURE [Part::Cut] Cut268
  Base = -> Cut267
  Tool = -> Compound218
FEATURE [Part::Compound] Compound219
  Links = -> [Cylinder447,Cylinder448]
FEATURE [Part::Cut] Cut269
  Base = -> Cut268
  Tool = -> Compound219
FEATURE [Part::Compound] Compound220
  Links = -> [Cylinder460,Cylinder453,Cylinder455,Cylinder457]
  Placement = pos=(0,20,0) rot=(0,0,1;0rad)
FEATURE [Part::Compound] Compound221
  Links = -> [Cylinder454,Cylinder456,Cylinder458,Cylinder459]
  Placement = pos=(0,17,0) rot=(0,0,1;0rad)
FEATURE [Part::Compound] Compound222
  Links = -> [Cut271,Cut270]
FEATURE [Part::Cut] Cut275
  Base = -> Compound222
  Tool = -> Compound220
FEATURE [Part::Cut] Cut274
  Base = -> Cut275
  Tool = -> Compound221
FEATURE [Part::Chamfer] Chamfer038
  Base = -> Cut269
  Edges = 1 edges r=2: [Edge22]
FEATURE [Part::Chamfer] Chamfer039
  Base = -> Cut274
  Edges = 2 edges r=2: [Edge25,Edge53]
FEATURE [Part::Chamfer] Chamfer040
  Base = -> Chamfer038
  Edges = 1 edges r=2: [Edge9]
FEATURE [Part::Chamfer] Chamfer042
  Base = -> Chamfer039
  Edges = 2 edges r=2: [Edge23,Edge57]
FEATURE [Part::Compound] Compound223  label="Wrist_tabular-wider"
  Links = -> [Chamfer040,Chamfer042,Cut252,Cut226,Cut225]
  Placement = pos=(-10,-170,20) rot=(0.707107,0,0.707107;3.14159rad)
FEATURE [Part::Box] Box1030  label="Krychle1029"
  AttacherType = Attacher::AttachEngine3D
  Height = 8
  Length = 12
  Placement = pos=(-10,-73,22) rot=(0,0,1;0rad)
  Width = 52
FEATURE [Part::Box] Box1031  label="Krychle1030"
  AttacherType = Attacher::AttachEngine3D
  Height = 8
  Length = 12
  Placement = pos=(-10,-73,-10) rot=(0,0,1;0rad)
  Width = 52
FEATURE [Part::Box] Box1032  label="Krychle1031"
  AttacherType = Attacher::AttachEngine3D
  Height = 8
  Length = 12
  Placement = pos=(-5,-73,-10) rot=(0,0,1;0rad)
  Width = 52
FEATURE [Part::Box] Box1033  label="Krychle1032"
  AttacherType = Attacher::AttachEngine3D
  Height = 8
  Length = 12
  Placement = pos=(-5,-73,22) rot=(0,0,1;0rad)
  Width = 52
FEATURE [Part::Box] Box1034  label="Krychle1033"
  AttacherType = Attacher::AttachEngine3D
  Height = 6
  Length = 6
  Placement = pos=(-7,-41,-10) rot=(0,0,1;0rad)
  Width = 2
FEATURE [Part::Box] Box1035  label="Krychle1034"
  AttacherType = Attacher::AttachEngine3D
  Height = 6
  Length = 6
  Placement = pos=(35,-41,-10) rot=(0,0,1;0rad)
  Width = 2
FEATURE [Part::Box] Box1036  label="Krychle1035"
  AttacherType = Attacher::AttachEngine3D
  Height = 6
  Length = 6
  Placement = pos=(-7,-41,24) rot=(0,0,1;0rad)
  Width = 2
FEATURE [Part::Box] Box1037  label="Krychle1036"
  AttacherType = Attacher::AttachEngine3D
  Height = 6
  Length = 6
  Placement = pos=(35,-41,24) rot=(0,0,1;0rad)
  Width = 2
FEATURE [Part::Cylinder] Cylinder2883  label="Válec2853"
  Angle = 360
  AttacherType = Attacher::AttachEngine3D
  Height = 3
  Placement = pos=(33,-32,0) rot=(1,0,0;1.5708rad)
  Radius = 3
FEATURE [Part::Cylinder] Cylinder2884  label="Válec2854"
  Angle = 360
  AttacherType = Attacher::AttachEngine3D
  Height = 3
  Placement = pos=(33,-32,20) rot=(1,0,0;1.5708rad)
  Radius = 3
FEATURE [Part::Cylinder] Cylinder2885  label="Válec2855"
  Angle = 360
  AttacherType = Attacher::AttachEngine3D
  Height = 3
  Placement = pos=(1,-32,0) rot=(1,0,0;1.5708rad)
  Radius = 3
FEATURE [Part::Cylinder] Cylinder2886  label="Válec2856"
  Angle = 360
  AttacherType = Attacher::AttachEngine3D
  Height = 3
  Placement = pos=(1,-32,20) rot=(1,0,0;1.5708rad)
  Radius = 3
FEATURE [Part::Box] Box1038  label="Krychle1037"
  AttacherType = Attacher::AttachEngine3D
  Height = 6
  Length = 54
  Placement = pos=(-10,-25,24) rot=(0,0,1;0rad)
  Width = 10
FEATURE [Part::Box] Box1039  label="Krychle1038"
  AttacherType = Attacher::AttachEngine3D
  Height = 6
  Length = 54
  Placement = pos=(-10,-25,-10) rot=(0,0,1;0rad)
  Width = 10
FEATURE [Part::Cylinder] Cylinder2887  label="Válec2857"
  Angle = 360
  AttacherType = Attacher::AttachEngine3D
  Height = 50
  Placement = pos=(1,-32,20) rot=(1,0,0;1.5708rad)
  Radius = 1.5
FEATURE [Part::Cylinder] Cylinder2888  label="Válec2858"
  Angle = 360
  AttacherType = Attacher::AttachEngine3D
  Height = 50
  Placement = pos=(1,-32,0) rot=(1,0,0;1.5708rad)
  Radius = 1.5
FEATURE [Part::Cylinder] Cylinder2889  label="Válec2859"
  Angle = 360
  AttacherType = Attacher::AttachEngine3D
  Height = 50
  Placement = pos=(33,-32,20) rot=(1,0,0;1.5708rad)
  Radius = 1.5
FEATURE [Part::Cylinder] Cylinder2890  label="Válec2860"
  Angle = 360
  AttacherType = Attacher::AttachEngine3D
  Height = 50
  Placement = pos=(33,-32,0) rot=(1,0,0;1.5708rad)
  Radius = 1.5
FEATURE [Part::Cylinder] Cylinder2891  label="Válec2861"
  Angle = 360
  AttacherType = Attacher::AttachEngine3D
  Height = 80
  Placement = pos=(38,-32,-7) rot=(1,0,0;1.5708rad)
  Radius = 1.5
FEATURE [Part::Cylinder] Cylinder2892  label="Válec2862"
  Angle = 360
  AttacherType = Attacher::AttachEngine3D
  Height = 80
  Placement = pos=(-4,-32,27) rot=(1,0,0;1.5708rad)
  Radius = 1.5
FEATURE [Part::Cylinder] Cylinder2893  label="Válec2863"
  Angle = 360
  AttacherType = Attacher::AttachEngine3D
  Height = 80
  Placement = pos=(-4,-32,-7) rot=(1,0,0;1.5708rad)
  Radius = 1.5
FEATURE [Part::Cylinder] Cylinder2894  label="Válec2864"
  Angle = 360
  AttacherType = Attacher::AttachEngine3D
  Height = 80
  Placement = pos=(38,-32,27) rot=(1,0,0;1.5708rad)
  Radius = 1.5
FEATURE [Part::Cylinder] Cylinder2895  label="Válec2865"
  Angle = 360
  AttacherType = Attacher::AttachEngine3D
  Height = 3
  Placement = pos=(38,-32,27) rot=(1,0,0;1.5708rad)
  Radius = 3
FEATURE [Part::Cylinder] Cylinder2896  label="Válec2866"
  Angle = 360
  AttacherType = Attacher::AttachEngine3D
  Height = 3
  Placement = pos=(-4,-32,-7) rot=(1,0,0;1.5708rad)
  Radius = 3
FEATURE [Part::Cylinder] Cylinder2897  label="Válec2867"
  Angle = 360
  AttacherType = Attacher::AttachEngine3D
  Height = 3
  Placement = pos=(-4,-32,27) rot=(1,0,0;1.5708rad)
  Radius = 3
FEATURE [Part::Cylinder] Cylinder2898  label="Válec2868"
  Angle = 360
  AttacherType = Attacher::AttachEngine3D
  Height = 3
  Placement = pos=(38,-32,-7) rot=(1,0,0;1.5708rad)
  Radius = 3
FEATURE [Part::Cylinder] Cylinder2899  label="Válec2869"
  Angle = 360
  AttacherType = Attacher::AttachEngine3D
  Height = 50
  Placement = pos=(38,-32,-7) rot=(1,0,0;1.5708rad)
  Radius = 1.5
FEATURE [Part::Cylinder] Cylinder2900  label="Válec2870"
  Angle = 360
  AttacherType = Attacher::AttachEngine3D
  Height = 50
  Placement = pos=(-4,-32,27) rot=(1,0,0;1.5708rad)
  Radius = 1.5
FEATURE [Part::Cylinder] Cylinder2901  label="Válec2871"
  Angle = 360
  AttacherType = Attacher::AttachEngine3D
  Height = 50
  Placement = pos=(-4,-32,-7) rot=(1,0,0;1.5708rad)
  Radius = 1.5
FEATURE [Part::Cylinder] Cylinder2902  label="Válec2872"
  Angle = 360
  AttacherType = Attacher::AttachEngine3D
  Height = 50
  Placement = pos=(38,-32,27) rot=(1,0,0;1.5708rad)
  Radius = 1.5
FEATURE [Part::Cylinder] Cylinder2903  label="Válec2873"
  Angle = 360
  AttacherType = Attacher::AttachEngine3D
  Height = 6
  Placement = pos=(21,23,-28) rot=(0,0,1;0rad)
  Radius = 3
FEATURE [Part::Cylinder] Cylinder2904  label="Válec2874"
  Angle = 360
  AttacherType = Attacher::AttachEngine3D
  Height = 6
  Placement = pos=(-21,23,-28) rot=(0,0,1;0rad)
  Radius = 3
FEATURE [Part::Cylinder] Cylinder2905  label="Válec2875"
  Angle = 360
  AttacherType = Attacher::AttachEngine3D
  Height = 6
  Placement = pos=(21,-23,-28) rot=(0,0,1;0rad)
  Radius = 3
FEATURE [Part::Cylinder] Cylinder2906  label="Válec2876"
  Angle = 360
  AttacherType = Attacher::AttachEngine3D
  Height = 6
  Placement = pos=(-21,-23,-28) rot=(0,0,1;0rad)
  Radius = 3
FEATURE [Part::Box] Box1040  label="Krychle1039"
  AttacherType = Attacher::AttachEngine3D
  Height = 10
  Length = 12
  Placement = pos=(-10,-73,-16) rot=(0,0,1;0rad)
  Width = 4
FEATURE [Part::Box] Box1041  label="Krychle1040"
  AttacherType = Attacher::AttachEngine3D
  Height = 10
  Length = 12
  Placement = pos=(-10,-69,-16) rot=(0,0,1;0rad)
  Width = 6
FEATURE [Part::Box] Box1042  label="Krychle1041"
  AttacherType = Attacher::AttachEngine3D
  Height = 10
  Length = 12
  Placement = pos=(-10,-73,-16) rot=(0,0,1;0rad)
  Width = 4
FEATURE [Part::Box] Box1043  label="Krychle1042"
  AttacherType = Attacher::AttachEngine3D
  Height = 10
  Length = 12
  Placement = pos=(-10,-69,-16) rot=(0,0,1;0rad)
  Width = 6
FEATURE [Part::Box] Box1044  label="Krychle1043"
  AttacherType = Attacher::AttachEngine3D
  Height = 10
  Length = 12
  Placement = pos=(-10,-73,26) rot=(0,0,1;0rad)
  Width = 4
FEATURE [Part::Box] Box1045  label="Krychle1044"
  AttacherType = Attacher::AttachEngine3D
  Height = 10
  Length = 12
  Placement = pos=(-10,-69,26) rot=(0,0,1;0rad)
  Width = 6
FEATURE [Part::Box] Box1046  label="Krychle1045"
  AttacherType = Attacher::AttachEngine3D
  Height = 10
  Length = 12
  Placement = pos=(-10,-69,26) rot=(0,0,1;0rad)
  Width = 6
FEATURE [Part::Box] Box1047  label="Krychle1046"
  AttacherType = Attacher::AttachEngine3D
  Height = 10
  Length = 12
  Placement = pos=(-10,-73,26) rot=(0,0,1;0rad)
  Width = 4
FEATURE [Part::Cylinder] Cylinder2907  label="Válec2877"
  Angle = 360
  AttacherType = Attacher::AttachEngine3D
  Height = 10
  Placement = pos=(21,23,-28) rot=(0,0,1;0rad)
  Radius = 1.5
FEATURE [Part::Cylinder] Cylinder2908  label="Válec2878"
  Angle = 360
  AttacherType = Attacher::AttachEngine3D
  Height = 10
  Placement = pos=(-21,23,-28) rot=(0,0,1;0rad)
  Radius = 1.5
FEATURE [Part::Cylinder] Cylinder2909  label="Válec2879"
  Angle = 360
  AttacherType = Attacher::AttachEngine3D
  Height = 10
  Placement = pos=(21,-23,-28) rot=(0,0,1;0rad)
  Radius = 1.5
FEATURE [Part::Cylinder] Cylinder2910  label="Válec2880"
  Angle = 360
  AttacherType = Attacher::AttachEngine3D
  Height = 10
  Placement = pos=(-21,-23,-28) rot=(0,0,1;0rad)
  Radius = 1.5
FEATURE [Part::Cylinder] Cylinder2911  label="Válec2881"
  Angle = 360
  AttacherType = Attacher::AttachEngine3D
  Height = 3
  Placement = pos=(38,-32,-7) rot=(1,0,0;1.5708rad)
  Radius = 3
FEATURE [Part::Cylinder] Cylinder2912  label="Válec2882"
  Angle = 360
  AttacherType = Attacher::AttachEngine3D
  Height = 3
  Placement = pos=(38,-32,27) rot=(1,0,0;1.5708rad)
  Radius = 3
FEATURE [Part::Cylinder] Cylinder2913  label="Válec2883"
  Angle = 360
  AttacherType = Attacher::AttachEngine3D
  Height = 3
  Placement = pos=(-4,-32,27) rot=(1,0,0;1.5708rad)
  Radius = 3
FEATURE [Part::Cylinder] Cylinder2914  label="Válec2884"
  Angle = 360
  AttacherType = Attacher::AttachEngine3D
  Height = 3
  Placement = pos=(-4,-32,-7) rot=(1,0,0;1.5708rad)
  Radius = 3
FEATURE [Part::Cylinder] Cylinder2915  label="Válec2885"
  Angle = 360
  AttacherType = Attacher::AttachEngine3D
  Height = 32
  Placement = pos=(7,-10,-6) rot=(0,0,1;0rad)
  Radius = 8
FEATURE [Part::Cylinder] Cylinder2916  label="Válec2886"
  Angle = 360
  AttacherType = Attacher::AttachEngine3D
  Height = 32
  Placement = pos=(27,-10,-6) rot=(0,0,1;0rad)
  Radius = 8
FEATURE [Part::Cylinder] Cylinder2917  label="Válec2887"
  Angle = 360
  AttacherType = Attacher::AttachEngine3D
  Height = 20
  Placement = pos=(31,-10,10) rot=(1,0,0;1.5708rad)
  Radius = 1
FEATURE [Part::Box] Box1048  label="Krychle1047"
  AttacherType = Attacher::AttachEngine3D
  Height = 8
  Length = 54
  Placement = pos=(-10,-21,6) rot=(0,0,1;0rad)
  Width = 6
FEATURE [Part::Cylinder] Cylinder2918  label="Válec2888"
  Angle = 360
  AttacherType = Attacher::AttachEngine3D
  Height = 20
  Placement = pos=(3,-10,10) rot=(1,0,0;1.5708rad)
  Radius = 1
FEATURE [Part::Cylinder] Cylinder2919  label="Válec2889"
  Angle = 360
  AttacherType = Attacher::AttachEngine3D
  Height = 20
  Placement = pos=(17,-10,8) rot=(1,0,0;1.5708rad)
  Radius = 1
FEATURE [Part::Cylinder] Cylinder2920  label="Válec2890"
  Angle = 360
  AttacherType = Attacher::AttachEngine3D
  Height = 20
  Placement = pos=(17,-10,12) rot=(1,0,0;1.5708rad)
  Radius = 1
FEATURE [Part::Cylinder] Cylinder2921  label="Válec2891"
  Angle = 360
  AttacherType = Attacher::AttachEngine3D
  Height = 2
  Placement = pos=(31,-10,10) rot=(1,0,0;1.5708rad)
  Radius = 2
FEATURE [Part::Cylinder] Cylinder2922  label="Válec2892"
  Angle = 360
  AttacherType = Attacher::AttachEngine3D
  Height = 2
  Placement = pos=(17,-10,12) rot=(1,0,0;1.5708rad)
  Radius = 2
FEATURE [Part::Cylinder] Cylinder2923  label="Válec2893"
  Angle = 360
  AttacherType = Attacher::AttachEngine3D
  Height = 2
  Placement = pos=(3,-10,10) rot=(1,0,0;1.5708rad)
  Radius = 2
FEATURE [Part::Cylinder] Cylinder2924  label="Válec2894"
  Angle = 360
  AttacherType = Attacher::AttachEngine3D
  Height = 2
  Placement = pos=(17,-10,8) rot=(1,0,0;1.5708rad)
  Radius = 2
FEATURE [Part::Cylinder] Cylinder2925  label="Válec2895"
  Angle = 360
  AttacherType = Attacher::AttachEngine3D
  Height = 20
  Placement = pos=(-5,-17,10) rot=(1,0,0;1.5708rad)
  Radius = 2.65
FEATURE [Part::Cylinder] Cylinder2926  label="Válec2896"
  Angle = 360
  AttacherType = Attacher::AttachEngine3D
  Height = 20
  Placement = pos=(39,-17,10) rot=(1,0,0;1.5708rad)
  Radius = 2.65
FEATURE [Part::Box] Box1049  label="Krychle1048"
  AttacherType = Attacher::AttachEngine3D
  Height = 10
  Length = 54
  Placement = pos=(-10,-21,14) rot=(0,0,1;0rad)
  Width = 6
FEATURE [Part::Cylinder] Cylinder2927  label="Válec2897"
  Angle = 360
  AttacherType = Attacher::AttachEngine3D
  Height = 10
  Placement = pos=(27,-10,-4) rot=(0,0,1;0rad)
  Radius = 8
FEATURE [Part::Cylinder] Cylinder2928  label="Válec2898"
  Angle = 360
  AttacherType = Attacher::AttachEngine3D
  Height = 10
  Placement = pos=(7,-10,14) rot=(0,0,1;0rad)
  Radius = 8
FEATURE [Part::Cylinder] Cylinder2929  label="Válec2899"
  Angle = 360
  AttacherType = Attacher::AttachEngine3D
  Height = 10
  Placement = pos=(7,-10,-4) rot=(0,0,1;0rad)
  Radius = 8
FEATURE [Part::Cylinder] Cylinder2930  label="Válec2900"
  Angle = 360
  AttacherType = Attacher::AttachEngine3D
  Height = 10
  Placement = pos=(27,-10,14) rot=(0,0,1;0rad)
  Radius = 8
FEATURE [Part::Box] Box1050  label="Krychle1049"
  AttacherType = Attacher::AttachEngine3D
  Height = 10
  Length = 54
  Placement = pos=(-10,-21,-4) rot=(0,0,1;0rad)
  Width = 6
FEATURE [Part::Cylinder] Cylinder2931  label="Válec2901"
  Angle = 360
  AttacherType = Attacher::AttachEngine3D
  Height = 50
  Placement = pos=(-5,-32,-7) rot=(1,0,0;1.5708rad)
  Radius = 1.5
FEATURE [Part::Cylinder] Cylinder2932  label="Válec2902"
  Angle = 360
  AttacherType = Attacher::AttachEngine3D
  Height = 3
  Placement = pos=(-5,-32,27) rot=(1,0,0;1.5708rad)
  Radius = 3
FEATURE [Part::Cylinder] Cylinder2933  label="Válec2903"
  Angle = 360
  AttacherType = Attacher::AttachEngine3D
  Height = 50
  Placement = pos=(39,-32,27) rot=(1,0,0;1.5708rad)
  Radius = 1.5
FEATURE [Part::Cylinder] Cylinder2934  label="Válec2904"
  Angle = 360
  AttacherType = Attacher::AttachEngine3D
  Height = 3
  Placement = pos=(-5,-32,-7) rot=(1,0,0;1.5708rad)
  Radius = 3
FEATURE [Part::Cylinder] Cylinder2935  label="Válec2905"
  Angle = 360
  AttacherType = Attacher::AttachEngine3D
  Height = 50
  Placement = pos=(39,-32,-7) rot=(1,0,0;1.5708rad)
  Radius = 1.5
FEATURE [Part::Cylinder] Cylinder2936  label="Válec2906"
  Angle = 360
  AttacherType = Attacher::AttachEngine3D
  Height = 3
  Placement = pos=(39,-32,27) rot=(1,0,0;1.5708rad)
  Radius = 3
FEATURE [Part::Cylinder] Cylinder2937  label="Válec2907"
  Angle = 360
  AttacherType = Attacher::AttachEngine3D
  Height = 3
  Placement = pos=(39,-32,-7) rot=(1,0,0;1.5708rad)
  Radius = 3
FEATURE [Part::Cylinder] Cylinder2938  label="Válec2908"
  Angle = 360
  AttacherType = Attacher::AttachEngine3D
  Height = 50
  Placement = pos=(-5,-32,27) rot=(1,0,0;1.5708rad)
  Radius = 1.5
FEATURE [Part::Cylinder] Cylinder2939  label="Válec2909"
  Angle = 360
  AttacherType = Attacher::AttachEngine3D
  Height = 80
  Placement = pos=(-4,-32,-7) rot=(1,0,0;1.5708rad)
  Radius = 1.5
FEATURE [Part::Cylinder] Cylinder2940  label="Válec2910"
  Angle = 360
  AttacherType = Attacher::AttachEngine3D
  Height = 80
  Placement = pos=(38,-32,27) rot=(1,0,0;1.5708rad)
  Radius = 1.5
FEATURE [Part::Cylinder] Cylinder2941  label="Válec2911"
  Angle = 360
  AttacherType = Attacher::AttachEngine3D
  Height = 3
  Placement = pos=(-4,-70,27) rot=(1,0,0;1.5708rad)
  Radius = 3
FEATURE [Part::Cylinder] Cylinder2942  label="Válec2912"
  Angle = 360
  AttacherType = Attacher::AttachEngine3D
  Height = 3
  Placement = pos=(-4,-70,-7) rot=(1,0,0;1.5708rad)
  Radius = 3
FEATURE [Part::Cylinder] Cylinder2943  label="Válec2913"
  Angle = 360
  AttacherType = Attacher::AttachEngine3D
  Height = 80
  Placement = pos=(38,-32,-7) rot=(1,0,0;1.5708rad)
  Radius = 1.5
FEATURE [Part::Cylinder] Cylinder2944  label="Válec2914"
  Angle = 360
  AttacherType = Attacher::AttachEngine3D
  Height = 80
  Placement = pos=(-4,-32,27) rot=(1,0,0;1.5708rad)
  Radius = 1.5
FEATURE [Part::Cylinder] Cylinder2945  label="Válec2915"
  Angle = 360
  AttacherType = Attacher::AttachEngine3D
  Height = 3
  Placement = pos=(38,-70,-7) rot=(1,0,0;1.5708rad)
  Radius = 3
FEATURE [Part::Cylinder] Cylinder2946  label="Válec2916"
  Angle = 360
  AttacherType = Attacher::AttachEngine3D
  Height = 3
  Placement = pos=(38,-70,27) rot=(1,0,0;1.5708rad)
  Radius = 3
FEATURE [Part::Compound] Compound1289
  Links = -> [Box1030,Box1031]
FEATURE [Part::Compound] Compound1290
  Links = -> [Box1033,Box1032]
  Placement = pos=(37,0,0) rot=(0,0,1;0rad)
FEATURE [Part::Compound] Compound1291
  Links = -> [Compound1289,Compound1290]
FEATURE [Part::Compound] Compound1292
  Links = -> [Box1034,Box1035,Box1036,Box1037]
  Placement = pos=(0,-200,0) rot=(0,0,1;0rad)
FEATURE [Part::Compound] Compound1293
  Links = -> [Cylinder2886,Cylinder2885,Cylinder2884,Cylinder2883]
  Placement = pos=(0,17,0) rot=(0,0,1;0rad)
FEATURE [Part::Compound] Compound1294
  Links = -> [Cylinder2887,Cylinder2888,Cylinder2889,Cylinder2890]
  Placement = pos=(0,20,0) rot=(0,0,1;0rad)
FEATURE [Part::Cut] Cut1096
  Base = -> Compound1291
  Tool = -> Compound1294
FEATURE [Part::Compound] Compound1295
  Links = -> [Cylinder2892,Cylinder2893,Cylinder2894,Cylinder2891]
  Placement = pos=(0,20,0) rot=(0,0,1;0rad)
FEATURE [Part::Compound] Compound1296
  Links = -> [Cylinder2897,Cylinder2896,Cylinder2895,Cylinder2898]
  Placement = pos=(0,17,0) rot=(0,0,1;0rad)
FEATURE [Part::Compound] Compound1297
  Links = -> [Cylinder2900,Cylinder2901,Cylinder2902,Cylinder2899]
  Placement = pos=(0,20,0) rot=(0,0,1;0rad)
FEATURE [Part::Compound] Compound1298
  Links = -> [Box1038,Box1039]
FEATURE [Part::Cut] Cut1097
  Base = -> Compound1298
  Tool = -> Compound1297
FEATURE [Part::Compound] Compound1299
  Links = -> [Cylinder2906,Cylinder2903,Cylinder2904,Cylinder2905]
  Placement = pos=(17,-91,10) rot=(1,0,0;1.5708rad)
FEATURE [Part::Chamfer] Chamfer171
  Base = -> Box1041
  Edges = 1 edges r=5.6: [Edge11]
FEATURE [Part::Compound] Compound1300
  Links = -> [Box1040,Chamfer171]
FEATURE [Part::Chamfer] Chamfer172
  Base = -> Box1043
  Edges = 1 edges r=5.6: [Edge11]
FEATURE [Part::Compound] Compound1301
  Links = -> [Box1042,Chamfer172]
  Placement = pos=(42,0,0) rot=(0,0,1;0rad)
FEATURE [Part::Chamfer] Chamfer173
  Base = -> Box1045
  Edges = 1 edges r=5.6: [Edge12]
FEATURE [Part::Compound] Compound1302
  Links = -> [Box1044,Chamfer173]
FEATURE [Part::Chamfer] Chamfer174
  Base = -> Box1046
  Edges = 1 edges r=5.6: [Edge12]
FEATURE [Part::Compound] Compound1303
  Links = -> [Box1047,Chamfer174]
  Placement = pos=(42,0,0) rot=(0,0,1;0rad)
FEATURE [Part::Compound] Compound1304
  Links = -> [Compound1300,Compound1303,Compound1302,Compound1301]
FEATURE [Part::Cut] Cut1094
  Base = -> Compound1304
  Tool = -> Compound1299
FEATURE [Part::Compound] Compound1305
  Links = -> [Cylinder2910,Cylinder2907,Cylinder2908,Cylinder2909]
  Placement = pos=(17,-95,10) rot=(1,0,0;1.5708rad)
FEATURE [Part::Compound] Compound1306
  Links = -> [Cylinder2913,Cylinder2914,Cylinder2912,Cylinder2911]
  Placement = pos=(0,-38,0) rot=(0,0,1;0rad)
FEATURE [Part::Compound] Compound1307
  Links = -> [Cylinder2915,Cylinder2916]
FEATURE [Part::Compound] Compound1308
  Links = -> [Cylinder2923,Cylinder2921,Cylinder2924,Cylinder2922]
  Placement = pos=(0,-9,0) rot=(0,0,1;0rad)
FEATURE [Part::Cut] Cut1099
  Base = -> Box1048
  Tool = -> Compound1308
FEATURE [Part::Compound] Compound1309
  Links = -> [Cylinder2918,Cylinder2917,Cylinder2919,Cylinder2920]
FEATURE [Part::Compound] Compound1310
  Links = -> [Cylinder2925,Cylinder2926]
FEATURE [Part::Compound] Compound1311
  Links = -> [Cylinder2938,Cylinder2931,Cylinder2933,Cylinder2935]
  Placement = pos=(0,20,0) rot=(0,0,1;0rad)
FEATURE [Part::Compound] Compound1312
  Links = -> [Cylinder2932,Cylinder2934,Cylinder2936,Cylinder2937]
  Placement = pos=(0,17,0) rot=(0,0,1;0rad)
FEATURE [Part::Cut] Cut1102
  Base = -> Cut1096
  Tool = -> Compound1292
FEATURE [Part::Cut] Cut1103
  Base = -> Cut1102
  Tool = -> Compound1293
FEATURE [Part::Cut] Cut1095
  Base = -> Cut1103
  Tool = -> Compound1295
FEATURE [Part::Cut] Cut1104
  Base = -> Cut1097
  Tool = -> Compound1296
FEATURE [Part::Chamfer] Chamfer169
  Base = -> Cut1104
  Edges = 2 edges r=3: [Edge3,Edge43]
FEATURE [Part::Chamfer] Chamfer170
  Base = -> Chamfer169
  Edges = 2 edges r=3: [Edge28,Edge73]
FEATURE [Part::Cut] Cut1098
  Base = -> Chamfer170
  Tool = -> Compound1307
FEATURE [Part::Cut] Cut1105
  Base = -> Cut1094
  Tool = -> Compound1305
FEATURE [Part::Cut] Cut1106
  Base = -> Cut1095
  Tool = -> Compound1306
FEATURE [Part::Cut] Cut1107
  Base = -> Cut1099
  Tool = -> Compound1309
FEATURE [Part::Cut] Cut1108
  Base = -> Cut1107
  Tool = -> Compound1310
FEATURE [Part::Chamfer] Chamfer175
  Base = -> Cut1108
  Edges = 1 edges r=2: [Edge22]
FEATURE [Part::Chamfer] Chamfer177
  Base = -> Chamfer175
  Edges = 1 edges r=2: [Edge9]
FEATURE [Part::Cut] Cut1111
  Base = -> Box1050
  Tool = -> Cylinder2929
FEATURE [Part::Cut] Cut1109
  Base = -> Cut1111
  Tool = -> Cylinder2927
FEATURE [Part::Cut] Cut1112
  Base = -> Box1049
  Tool = -> Cylinder2928
FEATURE [Part::Cut] Cut1110
  Base = -> Cut1112
  Tool = -> Cylinder2930
FEATURE [Part::Compound] Compound1313
  Links = -> [Cut1110,Cut1109]
FEATURE [Part::Cut] Cut1114
  Base = -> Compound1313
  Tool = -> Compound1311
FEATURE [Part::Cut] Cut1113
  Base = -> Cut1114
  Tool = -> Compound1312
FEATURE [Part::Chamfer] Chamfer176
  Base = -> Cut1113
  Edges = 2 edges r=2: [Edge25,Edge53]
FEATURE [Part::Chamfer] Chamfer178
  Base = -> Chamfer176
  Edges = 2 edges r=2: [Edge23,Edge57]
FEATURE [Part::Compound] Compound1314
  Links = -> [Cylinder2945,Cylinder2946,Cylinder2941,Cylinder2942]
FEATURE [Part::Cut] Cut1100
  Base = -> Cut1105
  Tool = -> Compound1314
FEATURE [Part::Chamfer] Chamfer179
  Base = -> Cut1098
  Edges = 2 edges r=2: [Edge1,Edge77]
FEATURE [Part::Chamfer] Chamfer180
  Base = -> Cut1106
  Edges = 2 edges r=2: [Edge56,Edge82]
FEATURE [Part::Chamfer] Chamfer044
  Base = -> Chamfer180
  Edges = 2 edges r=2: [Edge52,Edge76]
FEATURE [Part::Chamfer] Chamfer045
  Base = -> Chamfer179
  Edges = 2 edges r=2: [Edge6,Edge96]
FEATURE [Part::Compound] Compound1315
  Links = -> [Cylinder2944,Cylinder2939,Cylinder2940,Cylinder2943]
  Placement = pos=(0,20,0) rot=(0,0,1;0rad)
FEATURE [Part::Cut] Cut1101
  Base = -> Cut1100
  Tool = -> Compound1315
FEATURE [Part::Chamfer] Chamfer046
  Base = -> Cut1101
  Edges = 1 edges r=2: [Edge37]
FEATURE [Part::Chamfer] Chamfer047
  Base = -> Chamfer046
  Edges = 1 edges r=2: [Edge177]
FEATURE [Part::Chamfer] Chamfer181
  Base = -> Chamfer047
  Edges = 2 edges r=2: [Edge164,Edge249]
FEATURE [Part::Compound] Compound1316  label="Wrist_tabular-nuovo"
  Links = -> [Chamfer177,Chamfer178,Chamfer044,Chamfer045,Chamfer181]
  Placement = pos=(-10,-170,20) rot=(0.707107,0,0.707107;3.14159rad)
FEATURE [Mesh::Feature] Mesh006  label="Wrist_tabular-nuovo (Meshed)"
FEATURE [Mesh::Feature] Mesh007  label="G-mini_moto-holder-B-nuovo (Meshed)"
FEATURE [Mesh::Feature] Mesh008  label="Wrist_outer-halo (Meshed)"
FEATURE [Mesh::Feature] Mesh009  label="J-mini_encoder-belt-ring_front (Meshed)"
FEATURE [Mesh::Feature] Mesh010  label="Wrist_actuator-ring (Meshed)"
FEATURE [Mesh::Feature] Mesh011  label="Wrist_moto-hold (Meshed)"
FEATURE [Mesh::Feature] Mesh012  label="Wrist_halo-cover (Meshed)"
FEATURE [Mesh::Feature] Mesh013  label="G-mini_bearing-ring (Meshed)"
FEATURE [Mesh::Feature] Mesh014  label="G-mini_monoblock (Meshed)"
FEATURE [Mesh::Feature] Mesh015  label="G-mini_moto-holder-A (Meshed)001"
FEATURE [Mesh::Feature] Mesh016  label="G-mini_moto-holder-B (Meshed)"
FEATURE [Mesh::Feature] Mesh017  label="Wrist_outer-halo-ring (Meshed)"
FEATURE [Mesh::Feature] Mesh018  label="G-mini_underfix (Meshed)"
FEATURE [Mesh::Feature] Mesh019  label="G-mini_encoder_front-holder (Meshed)"
FEATURE [Mesh::Feature] Mesh020  label="Wrist_side-actuator (Meshed)"
FEATURE [Mesh::Feature] Mesh021  label="Wrist_outer-halo-encoder (Meshed)"
FEATURE [Mesh::Feature] Mesh022  label="G-mini_encoder-belt-ring (Meshed)001"
FEATURE [Mesh::Feature] Mesh023  label="Wrist_inner-halo (Meshed)001"
FEATURE [Mesh::Feature] Mesh024  label="G-mini_actuator-drum (Meshed)001"
FEATURE [Mesh::Feature] Mesh025  label="G-mini_moto-holder-B-nuovo (Meshed)001"
FEATURE [Mesh::Feature] Mesh026  label="Wrist_moto-hold-nuovo (Meshed)002"
FEATURE [Mesh::Feature] Mesh027  label="Wrist_tabular-nuovo (Meshed)001"
